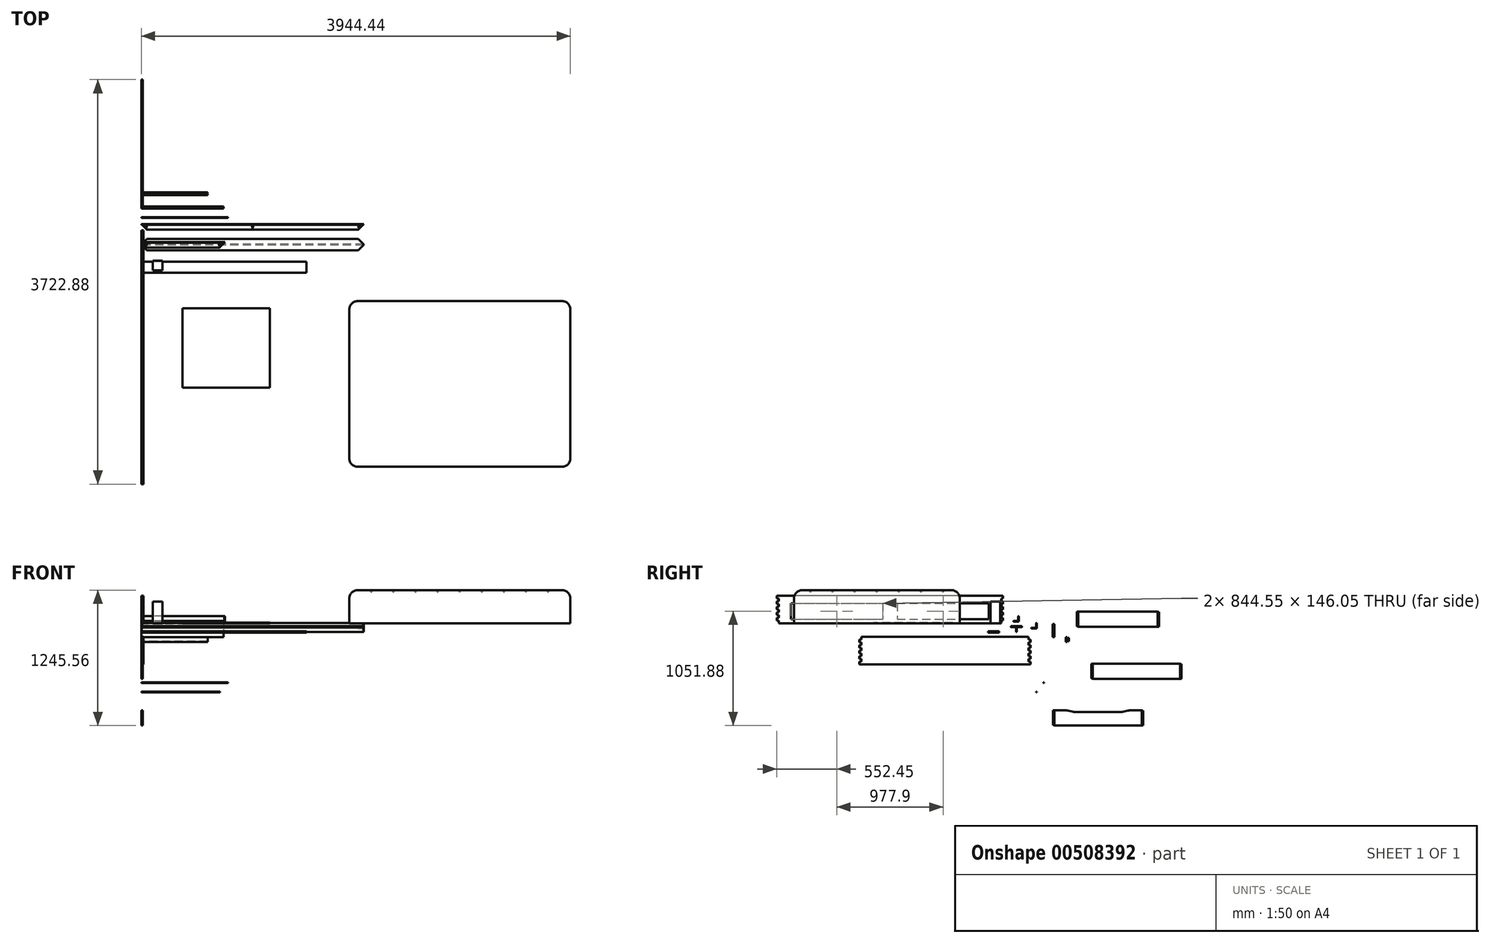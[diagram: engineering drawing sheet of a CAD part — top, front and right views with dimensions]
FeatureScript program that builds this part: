
annotation { "Feature Type Name" : "Feature", "Feature Type Description" : "" }
export const myFeature = defineFeature(function(context is Context, id is Id, definition is map)
    precondition{}
    {
        {
            var Q0;
            Q0=qCreatedBy(makeId("Right.planeOp"),FACE);
            var sketch = newSketch(context, id + "F0", { "sketchPlane" : qUnion([Q0])});
            skLineSegment(sketch, "E0.bottom", {"start": v(0, 0) * mm, "end": v(-2082.8, 0) * mm});
            skLineSegment(sketch, "E0.top", {"start": v(12.7, 254) * mm, "end": v(-2070.1, 254) * mm});
            skLineSegment(sketch, "E1", {"start": v(-2070.1, 254) * mm, "end": v(-2070.1, 228.6) * mm});
            skLineSegment(sketch, "E2", {"start": v(-2070.1, 228.6) * mm, "end": v(-2051.05, 228.6) * mm});
            skLineSegment(sketch, "E3", {"start": v(-2051.05, 228.6) * mm, "end": v(-2051.05, 203.2) * mm});
            skLineSegment(sketch, "E4", {"start": v(-2070.1, 254) * mm, "end": v(-2051.05, 254) * mm});
            skLineSegment(sketch, "E5.0.1.0", {"start": v(-2070.1, 203.2) * mm, "end": v(-2051.05, 203.2) * mm});
            skLineSegment(sketch, "E5.0.1.1", {"start": v(-2051.05, 177.8) * mm, "end": v(-2051.05, 152.4) * mm});
            skLineSegment(sketch, "E5.0.1.2", {"start": v(-2070.1, 177.8) * mm, "end": v(-2051.05, 177.8) * mm});
            skLineSegment(sketch, "E5.0.1.3", {"start": v(-2070.1, 203.2) * mm, "end": v(-2070.1, 177.8) * mm});
            skLineSegment(sketch, "E5.0.2.0", {"start": v(-2070.1, 152.4) * mm, "end": v(-2051.05, 152.4) * mm});
            skLineSegment(sketch, "E5.0.2.1", {"start": v(-2051.05, 127) * mm, "end": v(-2051.05, 101.6) * mm});
            skLineSegment(sketch, "E5.0.2.2", {"start": v(-2070.1, 127) * mm, "end": v(-2051.05, 127) * mm});
            skLineSegment(sketch, "E5.0.2.3", {"start": v(-2070.1, 152.4) * mm, "end": v(-2070.1, 127) * mm});
            skLineSegment(sketch, "E5.0.3.0", {"start": v(-2070.1, 101.6) * mm, "end": v(-2051.05, 101.6) * mm});
            skLineSegment(sketch, "E5.0.3.1", {"start": v(-2051.05, 76.2) * mm, "end": v(-2051.05, 50.8) * mm});
            skLineSegment(sketch, "E5.0.3.2", {"start": v(-2070.1, 76.2) * mm, "end": v(-2051.05, 76.2) * mm});
            skLineSegment(sketch, "E5.0.3.3", {"start": v(-2070.1, 101.6) * mm, "end": v(-2070.1, 76.2) * mm});
            skLineSegment(sketch, "E5.direction1", {"start": v(-2051.05, 203.2) * mm, "end": v(-1784.35, 203.2) * mm, "construction": true});
            skLineSegment(sketch, "E5.direction2", {"start": v(-2051.05, 203.2) * mm, "end": v(-2051.05, 152.4) * mm, "construction": true});
            skLineSegment(sketch, "E6.bottom", {"start": v(-1939.93, 184.15) * mm, "end": v(-1095.38, 184.15) * mm});
            skLineSegment(sketch, "E6.top", {"start": v(-1939.93, 38.1) * mm, "end": v(-1095.38, 38.1) * mm});
            skLineSegment(sketch, "E6.left", {"start": v(-1939.93, 184.15) * mm, "end": v(-1939.93, 38.1) * mm});
            skLineSegment(sketch, "E6.right", {"start": v(-1095.38, 184.15) * mm, "end": v(-1095.38, 38.1) * mm});
            skLineSegment(sketch, "E7.bottom", {"start": v(-962.02, 184.15) * mm, "end": v(-117.47, 184.15) * mm});
            skLineSegment(sketch, "E7.top", {"start": v(-962.02, 38.1) * mm, "end": v(-117.47, 38.1) * mm});
            skLineSegment(sketch, "E7.left", {"start": v(-962.02, 184.15) * mm, "end": v(-962.02, 38.1) * mm});
            skLineSegment(sketch, "E7.right", {"start": v(-117.47, 184.15) * mm, "end": v(-117.47, 38.1) * mm});
            skLineSegment(sketch, "E8.0.0.4", {"start": v(-2070.1, 50.8) * mm, "end": v(-2051.05, 50.8) * mm});
            skLineSegment(sketch, "E8.3.0.4", {"start": v(-2051.05, 25.4) * mm, "end": v(-2051.05, 0) * mm});
            skLineSegment(sketch, "E8.6.0.4", {"start": v(-2070.1, 25.4) * mm, "end": v(-2051.05, 25.4) * mm});
            skLineSegment(sketch, "E8.9.0.4", {"start": v(-2070.1, 50.8) * mm, "end": v(-2070.1, 25.4) * mm});
            skLineSegment(sketch, "E9", {"start": v(-6.35, 254) * mm, "end": v(12.7, 254) * mm});
            skLineSegment(sketch, "E10", {"start": v(12.7, 254) * mm, "end": v(12.7, 228.6) * mm});
            skLineSegment(sketch, "E11", {"start": v(12.7, 228.6) * mm, "end": v(-6.35, 228.6) * mm});
            skLineSegment(sketch, "E12", {"start": v(-6.35, 228.6) * mm, "end": v(-6.35, 203.2) * mm});
            skLineSegment(sketch, "E13.0.1.0", {"start": v(12.7, 177.8) * mm, "end": v(-6.35, 177.8) * mm});
            skLineSegment(sketch, "E13.0.1.1", {"start": v(-6.35, 177.8) * mm, "end": v(-6.35, 152.4) * mm});
            skLineSegment(sketch, "E13.0.1.2", {"start": v(12.7, 203.2) * mm, "end": v(12.7, 177.8) * mm});
            skLineSegment(sketch, "E13.0.1.3", {"start": v(-6.35, 203.2) * mm, "end": v(12.7, 203.2) * mm});
            skLineSegment(sketch, "E13.0.2.0", {"start": v(12.7, 127) * mm, "end": v(-6.35, 127) * mm});
            skLineSegment(sketch, "E13.0.2.1", {"start": v(-6.35, 127) * mm, "end": v(-6.35, 101.6) * mm});
            skLineSegment(sketch, "E13.0.2.2", {"start": v(12.7, 152.4) * mm, "end": v(12.7, 127) * mm});
            skLineSegment(sketch, "E13.0.2.3", {"start": v(-6.35, 152.4) * mm, "end": v(12.7, 152.4) * mm});
            skLineSegment(sketch, "E13.0.3.0", {"start": v(12.7, 76.2) * mm, "end": v(-6.35, 76.2) * mm});
            skLineSegment(sketch, "E13.0.3.1", {"start": v(-6.35, 76.2) * mm, "end": v(-6.35, 50.8) * mm});
            skLineSegment(sketch, "E13.0.3.2", {"start": v(12.7, 101.6) * mm, "end": v(12.7, 76.2) * mm});
            skLineSegment(sketch, "E13.0.3.3", {"start": v(-6.35, 101.6) * mm, "end": v(12.7, 101.6) * mm});
            skLineSegment(sketch, "E13.0.4.0", {"start": v(12.7, 25.4) * mm, "end": v(-6.35, 25.4) * mm});
            skLineSegment(sketch, "E13.0.4.1", {"start": v(-6.35, 25.4) * mm, "end": v(-6.35, 0) * mm});
            skLineSegment(sketch, "E13.0.4.2", {"start": v(12.7, 50.8) * mm, "end": v(12.7, 25.4) * mm});
            skLineSegment(sketch, "E13.0.4.3", {"start": v(-6.35, 50.8) * mm, "end": v(12.7, 50.8) * mm});
            skLineSegment(sketch, "E13.direction1", {"start": v(-6.35, 203.2) * mm, "end": v(6.35, 203.2) * mm, "construction": true});
            skLineSegment(sketch, "E13.direction2", {"start": v(-6.35, 203.2) * mm, "end": v(-6.35, 152.4) * mm, "construction": true});
            skSolve(sketch);
        }
        {
            var Q0;
            Q0 = qSketchRegion(id + "F0", true);
            extrude(context, id + "F1", {"entities" : qUnion([Q0]), "depth" : 19.05 * mm});
        }
        {
            var Q0;
            Q0=qCreatedBy(makeId("Right.planeOp"),FACE);
            var sketch = newSketch(context, id + "F2", { "sketchPlane" : qUnion([Q0])});
            skLineSegment(sketch, "E14.top", {"start": v(264.4, -378.2) * mm, "end": v(-1310.4, -378.2) * mm});
            skLineSegment(sketch, "E15", {"start": v(-1291.36, -378.2) * mm, "end": v(-1310.4, -378.2) * mm});
            skLineSegment(sketch, "E16", {"start": v(-1310.4, -352.8) * mm, "end": v(-1291.36, -352.8) * mm});
            skLineSegment(sketch, "E17", {"start": v(-1291.36, -352.8) * mm, "end": v(-1291.36, -327.4) * mm});
            skLineSegment(sketch, "E18", {"start": v(-1310.4, -378.2) * mm, "end": v(-1310.4, -352.8) * mm});
            skLineSegment(sketch, "E19.0.1.0", {"start": v(-1310.4, -302) * mm, "end": v(-1291.36, -302) * mm});
            skLineSegment(sketch, "E19.0.1.1", {"start": v(-1310.4, -327.4) * mm, "end": v(-1310.4, -302) * mm});
            skLineSegment(sketch, "E19.0.1.2", {"start": v(-1291.36, -327.4) * mm, "end": v(-1310.4, -327.4) * mm});
            skLineSegment(sketch, "E19.0.1.3", {"start": v(-1291.36, -302) * mm, "end": v(-1291.36, -276.6) * mm});
            skLineSegment(sketch, "E19.0.2.0", {"start": v(-1310.4, -251.2) * mm, "end": v(-1291.36, -251.2) * mm});
            skLineSegment(sketch, "E19.0.2.1", {"start": v(-1310.4, -276.6) * mm, "end": v(-1310.4, -251.2) * mm});
            skLineSegment(sketch, "E19.0.2.2", {"start": v(-1291.36, -276.6) * mm, "end": v(-1310.4, -276.6) * mm});
            skLineSegment(sketch, "E19.0.2.3", {"start": v(-1291.36, -251.2) * mm, "end": v(-1291.36, -225.8) * mm});
            skLineSegment(sketch, "E19.0.3.0", {"start": v(-1310.4, -200.4) * mm, "end": v(-1291.36, -200.4) * mm});
            skLineSegment(sketch, "E19.0.3.1", {"start": v(-1310.4, -225.8) * mm, "end": v(-1310.4, -200.4) * mm});
            skLineSegment(sketch, "E19.0.3.2", {"start": v(-1291.36, -225.8) * mm, "end": v(-1310.4, -225.8) * mm});
            skLineSegment(sketch, "E19.0.3.3", {"start": v(-1291.36, -200.4) * mm, "end": v(-1291.36, -175) * mm});
            skLineSegment(sketch, "E19.direction1", {"start": v(-1310.4, -378.2) * mm, "end": v(-1285, -378.2) * mm, "construction": true});
            skLineSegment(sketch, "E19.direction2", {"start": v(-1310.4, -378.2) * mm, "end": v(-1310.4, -327.4) * mm, "construction": true});
            skLineSegment(sketch, "E20", {"start": v(245.34, -378.2) * mm, "end": v(264.4, -378.2) * mm});
            skLineSegment(sketch, "E21", {"start": v(264.4, -352.8) * mm, "end": v(245.34, -352.8) * mm});
            skLineSegment(sketch, "E22", {"start": v(245.34, -352.8) * mm, "end": v(245.34, -327.4) * mm});
            skLineSegment(sketch, "E23", {"start": v(264.4, -352.8) * mm, "end": v(264.4, -378.2) * mm});
            skLineSegment(sketch, "E24.0.1.0", {"start": v(264.4, -302) * mm, "end": v(245.34, -302) * mm});
            skLineSegment(sketch, "E24.0.1.1", {"start": v(245.34, -302) * mm, "end": v(245.34, -276.6) * mm});
            skLineSegment(sketch, "E24.0.1.2", {"start": v(264.4, -302) * mm, "end": v(264.4, -327.4) * mm});
            skLineSegment(sketch, "E24.0.1.3", {"start": v(245.34, -327.4) * mm, "end": v(264.4, -327.4) * mm});
            skLineSegment(sketch, "E24.0.2.0", {"start": v(264.4, -251.2) * mm, "end": v(245.34, -251.2) * mm});
            skLineSegment(sketch, "E24.0.2.1", {"start": v(245.34, -251.2) * mm, "end": v(245.34, -225.8) * mm});
            skLineSegment(sketch, "E24.0.2.2", {"start": v(264.4, -251.2) * mm, "end": v(264.4, -276.6) * mm});
            skLineSegment(sketch, "E24.0.2.3", {"start": v(245.34, -276.6) * mm, "end": v(264.4, -276.6) * mm});
            skLineSegment(sketch, "E24.0.3.0", {"start": v(264.4, -200.4) * mm, "end": v(245.34, -200.4) * mm});
            skLineSegment(sketch, "E24.0.3.1", {"start": v(245.34, -200.4) * mm, "end": v(245.34, -175) * mm});
            skLineSegment(sketch, "E24.0.3.2", {"start": v(264.4, -200.4) * mm, "end": v(264.4, -225.8) * mm});
            skLineSegment(sketch, "E24.0.3.3", {"start": v(245.34, -225.8) * mm, "end": v(264.4, -225.8) * mm});
            skLineSegment(sketch, "E24.direction1", {"start": v(219.94, -378.2) * mm, "end": v(245.34, -378.2) * mm, "construction": true});
            skLineSegment(sketch, "E24.direction2", {"start": v(245.34, -378.2) * mm, "end": v(245.34, -327.4) * mm, "construction": true});
            skLineSegment(sketch, "E25.0.0.4", {"start": v(-1310.4, -149.6) * mm, "end": v(-1291.36, -149.6) * mm});
            skLineSegment(sketch, "E25.3.0.4", {"start": v(-1310.4, -175) * mm, "end": v(-1310.4, -149.6) * mm});
            skLineSegment(sketch, "E25.6.0.4", {"start": v(-1291.36, -175) * mm, "end": v(-1310.4, -175) * mm});
            skLineSegment(sketch, "E25.9.0.4", {"start": v(-1291.36, -149.6) * mm, "end": v(-1291.36, -124.2) * mm});
            skLineSegment(sketch, "E26.0.0.4", {"start": v(264.4, -149.6) * mm, "end": v(245.34, -149.6) * mm});
            skLineSegment(sketch, "E26.3.0.4", {"start": v(245.34, -149.6) * mm, "end": v(245.34, -124.2) * mm});
            skLineSegment(sketch, "E26.6.0.4", {"start": v(264.4, -149.6) * mm, "end": v(264.4, -175) * mm});
            skLineSegment(sketch, "E26.9.0.4", {"start": v(245.34, -175) * mm, "end": v(264.4, -175) * mm});
            skLineSegment(sketch, "E27", {"start": v(245.34, -124.2) * mm, "end": v(-1291.36, -124.2) * mm});
            skSolve(sketch);
        }
        {
            var Q0;
            Q0 = qSketchRegion(id + "F2", true);
            extrude(context, id + "F3", {"entities" : qUnion([Q0]), "depth" : 19.05 * mm});
        }
        {
            var Q0;
            Q0=qCreatedBy(makeId("Right.planeOp"),FACE);
            var sketch = newSketch(context, id + "F4", { "sketchPlane" : qUnion([Q0])});
            skLineSegment(sketch, "E28.bottom", {"start": v(702.37, 107.96) * mm, "end": v(1432.62, 107.96) * mm});
            skLineSegment(sketch, "E28.top", {"start": v(702.37, -31.74) * mm, "end": v(1445.32, -31.74) * mm});
            skLineSegment(sketch, "E29", {"start": v(1432.62, 104.78) * mm, "end": v(1445.32, 104.78) * mm});
            skLineSegment(sketch, "E30", {"start": v(1445.32, 101.6) * mm, "end": v(1432.62, 101.6) * mm});
            skLineSegment(sketch, "E31", {"start": v(1432.62, 101.6) * mm, "end": v(1432.62, 98.43) * mm});
            skLineSegment(sketch, "E32", {"start": v(1445.32, 104.78) * mm, "end": v(1445.32, 101.6) * mm});
            skLineSegment(sketch, "E33.0.1.0", {"start": v(1432.62, 98.43) * mm, "end": v(1445.32, 98.43) * mm});
            skLineSegment(sketch, "E33.0.1.1", {"start": v(1445.32, 95.26) * mm, "end": v(1432.62, 95.26) * mm});
            skLineSegment(sketch, "E33.0.1.2", {"start": v(1432.62, 95.26) * mm, "end": v(1432.62, 92.08) * mm});
            skLineSegment(sketch, "E33.0.1.3", {"start": v(1445.32, 98.43) * mm, "end": v(1445.32, 95.26) * mm});
            skLineSegment(sketch, "E33.0.2.0", {"start": v(1432.62, 92.08) * mm, "end": v(1445.32, 92.08) * mm});
            skLineSegment(sketch, "E33.0.2.1", {"start": v(1445.32, 88.9) * mm, "end": v(1432.62, 88.9) * mm});
            skLineSegment(sketch, "E33.0.2.2", {"start": v(1432.62, 88.9) * mm, "end": v(1432.62, 85.73) * mm});
            skLineSegment(sketch, "E33.0.2.3", {"start": v(1445.32, 92.08) * mm, "end": v(1445.32, 88.9) * mm});
            skLineSegment(sketch, "E33.0.3.0", {"start": v(1432.62, 85.73) * mm, "end": v(1445.32, 85.73) * mm});
            skLineSegment(sketch, "E33.0.3.1", {"start": v(1445.32, 82.56) * mm, "end": v(1432.62, 82.56) * mm});
            skLineSegment(sketch, "E33.0.3.2", {"start": v(1432.62, 82.56) * mm, "end": v(1432.62, 79.38) * mm});
            skLineSegment(sketch, "E33.0.3.3", {"start": v(1445.32, 85.73) * mm, "end": v(1445.32, 82.56) * mm});
            skLineSegment(sketch, "E33.0.4.0", {"start": v(1432.62, 79.38) * mm, "end": v(1445.32, 79.38) * mm});
            skLineSegment(sketch, "E33.0.4.1", {"start": v(1445.32, 76.2) * mm, "end": v(1432.62, 76.2) * mm});
            skLineSegment(sketch, "E33.0.4.2", {"start": v(1432.62, 76.2) * mm, "end": v(1432.62, 73.03) * mm});
            skLineSegment(sketch, "E33.0.4.3", {"start": v(1445.32, 79.38) * mm, "end": v(1445.32, 76.2) * mm});
            skLineSegment(sketch, "E33.0.5.0", {"start": v(1432.62, 73.03) * mm, "end": v(1445.32, 73.03) * mm});
            skLineSegment(sketch, "E33.0.5.1", {"start": v(1445.32, 69.86) * mm, "end": v(1432.62, 69.86) * mm});
            skLineSegment(sketch, "E33.0.5.2", {"start": v(1432.62, 69.86) * mm, "end": v(1432.62, 66.68) * mm});
            skLineSegment(sketch, "E33.0.5.3", {"start": v(1445.32, 73.03) * mm, "end": v(1445.32, 69.86) * mm});
            skLineSegment(sketch, "E33.0.6.0", {"start": v(1432.62, 66.68) * mm, "end": v(1445.32, 66.68) * mm});
            skLineSegment(sketch, "E33.0.6.1", {"start": v(1445.32, 63.5) * mm, "end": v(1432.62, 63.5) * mm});
            skLineSegment(sketch, "E33.0.6.2", {"start": v(1432.62, 63.5) * mm, "end": v(1432.62, 60.33) * mm});
            skLineSegment(sketch, "E33.0.6.3", {"start": v(1445.32, 66.68) * mm, "end": v(1445.32, 63.5) * mm});
            skLineSegment(sketch, "E33.0.7.0", {"start": v(1432.62, 60.33) * mm, "end": v(1445.32, 60.33) * mm});
            skLineSegment(sketch, "E33.0.7.1", {"start": v(1445.32, 57.16) * mm, "end": v(1432.62, 57.16) * mm});
            skLineSegment(sketch, "E33.0.7.2", {"start": v(1432.62, 57.16) * mm, "end": v(1432.62, 53.98) * mm});
            skLineSegment(sketch, "E33.0.7.3", {"start": v(1445.32, 60.33) * mm, "end": v(1445.32, 57.16) * mm});
            skLineSegment(sketch, "E33.0.8.0", {"start": v(1432.62, 53.98) * mm, "end": v(1445.32, 53.98) * mm});
            skLineSegment(sketch, "E33.0.8.1", {"start": v(1445.32, 50.8) * mm, "end": v(1432.62, 50.8) * mm});
            skLineSegment(sketch, "E33.0.8.2", {"start": v(1432.62, 50.8) * mm, "end": v(1432.62, 47.63) * mm});
            skLineSegment(sketch, "E33.0.8.3", {"start": v(1445.32, 53.98) * mm, "end": v(1445.32, 50.8) * mm});
            skLineSegment(sketch, "E33.0.9.0", {"start": v(1432.62, 47.63) * mm, "end": v(1445.32, 47.63) * mm});
            skLineSegment(sketch, "E33.0.9.1", {"start": v(1445.32, 44.46) * mm, "end": v(1432.62, 44.46) * mm});
            skLineSegment(sketch, "E33.0.9.2", {"start": v(1432.62, 44.46) * mm, "end": v(1432.62, 41.28) * mm});
            skLineSegment(sketch, "E33.0.9.3", {"start": v(1445.32, 47.63) * mm, "end": v(1445.32, 44.46) * mm});
            skLineSegment(sketch, "E33.0.10.0", {"start": v(1432.62, 41.28) * mm, "end": v(1445.32, 41.28) * mm});
            skLineSegment(sketch, "E33.0.10.1", {"start": v(1445.32, 38.1) * mm, "end": v(1432.62, 38.1) * mm});
            skLineSegment(sketch, "E33.0.10.2", {"start": v(1432.62, 38.1) * mm, "end": v(1432.62, 34.93) * mm});
            skLineSegment(sketch, "E33.0.10.3", {"start": v(1445.32, 41.28) * mm, "end": v(1445.32, 38.1) * mm});
            skLineSegment(sketch, "E33.0.11.0", {"start": v(1432.62, 34.93) * mm, "end": v(1445.32, 34.93) * mm});
            skLineSegment(sketch, "E33.0.11.1", {"start": v(1445.32, 31.76) * mm, "end": v(1432.62, 31.76) * mm});
            skLineSegment(sketch, "E33.0.11.2", {"start": v(1432.62, 31.76) * mm, "end": v(1432.62, 28.58) * mm});
            skLineSegment(sketch, "E33.0.11.3", {"start": v(1445.32, 34.93) * mm, "end": v(1445.32, 31.76) * mm});
            skLineSegment(sketch, "E33.0.12.0", {"start": v(1432.62, 28.58) * mm, "end": v(1445.32, 28.58) * mm});
            skLineSegment(sketch, "E33.0.12.1", {"start": v(1445.32, 25.4) * mm, "end": v(1432.62, 25.4) * mm});
            skLineSegment(sketch, "E33.0.12.2", {"start": v(1432.62, 25.4) * mm, "end": v(1432.62, 22.23) * mm});
            skLineSegment(sketch, "E33.0.12.3", {"start": v(1445.32, 28.58) * mm, "end": v(1445.32, 25.4) * mm});
            skLineSegment(sketch, "E33.0.13.0", {"start": v(1432.62, 22.23) * mm, "end": v(1445.32, 22.23) * mm});
            skLineSegment(sketch, "E33.0.13.1", {"start": v(1445.32, 19.06) * mm, "end": v(1432.62, 19.06) * mm});
            skLineSegment(sketch, "E33.0.13.2", {"start": v(1432.62, 19.06) * mm, "end": v(1432.62, 15.88) * mm});
            skLineSegment(sketch, "E33.0.13.3", {"start": v(1445.32, 22.23) * mm, "end": v(1445.32, 19.06) * mm});
            skLineSegment(sketch, "E33.0.14.0", {"start": v(1432.62, 15.88) * mm, "end": v(1445.32, 15.88) * mm});
            skLineSegment(sketch, "E33.0.14.1", {"start": v(1445.32, 12.7) * mm, "end": v(1432.62, 12.7) * mm});
            skLineSegment(sketch, "E33.0.14.2", {"start": v(1432.62, 12.7) * mm, "end": v(1432.62, 9.53) * mm});
            skLineSegment(sketch, "E33.0.14.3", {"start": v(1445.32, 15.88) * mm, "end": v(1445.32, 12.7) * mm});
            skLineSegment(sketch, "E33.0.15.0", {"start": v(1432.62, 9.53) * mm, "end": v(1445.32, 9.53) * mm});
            skLineSegment(sketch, "E33.0.15.1", {"start": v(1445.32, 6.36) * mm, "end": v(1432.62, 6.36) * mm});
            skLineSegment(sketch, "E33.0.15.2", {"start": v(1432.62, 6.36) * mm, "end": v(1432.62, 3.18) * mm});
            skLineSegment(sketch, "E33.0.15.3", {"start": v(1445.32, 9.53) * mm, "end": v(1445.32, 6.36) * mm});
            skLineSegment(sketch, "E33.0.16.0", {"start": v(1432.62, 3.18) * mm, "end": v(1445.32, 3.18) * mm});
            skLineSegment(sketch, "E33.0.16.1", {"start": v(1445.32, 0) * mm, "end": v(1432.62, 0) * mm});
            skLineSegment(sketch, "E33.0.16.2", {"start": v(1432.62, 0) * mm, "end": v(1432.62, -3.17) * mm});
            skLineSegment(sketch, "E33.0.16.3", {"start": v(1445.32, 3.18) * mm, "end": v(1445.32, 0) * mm});
            skLineSegment(sketch, "E33.0.17.0", {"start": v(1432.62, -3.17) * mm, "end": v(1445.32, -3.17) * mm});
            skLineSegment(sketch, "E33.0.17.1", {"start": v(1445.32, -6.34) * mm, "end": v(1432.62, -6.34) * mm});
            skLineSegment(sketch, "E33.0.17.2", {"start": v(1432.62, -6.34) * mm, "end": v(1432.62, -9.52) * mm});
            skLineSegment(sketch, "E33.0.17.3", {"start": v(1445.32, -3.17) * mm, "end": v(1445.32, -6.34) * mm});
            skLineSegment(sketch, "E33.0.18.0", {"start": v(1432.62, -9.52) * mm, "end": v(1445.32, -9.52) * mm});
            skLineSegment(sketch, "E33.0.18.1", {"start": v(1445.32, -12.7) * mm, "end": v(1432.62, -12.7) * mm});
            skLineSegment(sketch, "E33.0.18.2", {"start": v(1432.62, -12.7) * mm, "end": v(1432.62, -15.87) * mm});
            skLineSegment(sketch, "E33.0.18.3", {"start": v(1445.32, -9.52) * mm, "end": v(1445.32, -12.7) * mm});
            skLineSegment(sketch, "E33.0.19.0", {"start": v(1432.62, -15.87) * mm, "end": v(1445.32, -15.87) * mm});
            skLineSegment(sketch, "E33.0.19.1", {"start": v(1445.32, -19.04) * mm, "end": v(1432.62, -19.04) * mm});
            skLineSegment(sketch, "E33.0.19.2", {"start": v(1432.62, -19.04) * mm, "end": v(1432.62, -22.22) * mm});
            skLineSegment(sketch, "E33.0.19.3", {"start": v(1445.32, -15.87) * mm, "end": v(1445.32, -19.04) * mm});
            skLineSegment(sketch, "E33.0.20.0", {"start": v(1432.62, -22.22) * mm, "end": v(1445.32, -22.22) * mm});
            skLineSegment(sketch, "E33.0.20.1", {"start": v(1445.32, -25.4) * mm, "end": v(1432.62, -25.4) * mm});
            skLineSegment(sketch, "E33.0.20.2", {"start": v(1432.62, -25.4) * mm, "end": v(1432.62, -28.57) * mm});
            skLineSegment(sketch, "E33.0.20.3", {"start": v(1445.32, -22.22) * mm, "end": v(1445.32, -25.4) * mm});
            skLineSegment(sketch, "E33.0.21.0", {"start": v(1432.62, -28.57) * mm, "end": v(1445.32, -28.57) * mm});
            skLineSegment(sketch, "E33.0.21.1", {"start": v(1445.32, -31.74) * mm, "end": v(1432.62, -31.74) * mm});
            skLineSegment(sketch, "E33.0.21.3", {"start": v(1445.32, -28.57) * mm, "end": v(1445.32, -31.74) * mm});
            skLineSegment(sketch, "E33.direction1", {"start": v(1432.62, 98.43) * mm, "end": v(1458.02, 98.43) * mm, "construction": true});
            skLineSegment(sketch, "E33.direction2", {"start": v(1432.62, 98.43) * mm, "end": v(1432.62, 92.08) * mm, "construction": true});
            skLineSegment(sketch, "E34", {"start": v(1432.62, 104.78) * mm, "end": v(1432.62, 107.96) * mm});
            skLineSegment(sketch, "E35", {"start": v(702.37, -31.74) * mm, "end": v(702.37, -28.57) * mm});
            skLineSegment(sketch, "E36", {"start": v(702.37, -28.57) * mm, "end": v(689.67, -28.57) * mm});
            skLineSegment(sketch, "E37", {"start": v(689.67, -28.57) * mm, "end": v(689.67, -25.4) * mm});
            skLineSegment(sketch, "E38", {"start": v(689.67, -25.4) * mm, "end": v(702.37, -25.4) * mm});
            skLineSegment(sketch, "E39.0.1.0", {"start": v(702.37, -22.22) * mm, "end": v(689.67, -22.22) * mm});
            skLineSegment(sketch, "E39.0.1.1", {"start": v(689.67, -19.04) * mm, "end": v(702.37, -19.04) * mm});
            skLineSegment(sketch, "E39.0.1.2", {"start": v(702.37, -25.4) * mm, "end": v(702.37, -22.22) * mm});
            skLineSegment(sketch, "E39.0.1.3", {"start": v(689.67, -22.22) * mm, "end": v(689.67, -19.04) * mm});
            skLineSegment(sketch, "E39.0.2.0", {"start": v(702.37, -15.87) * mm, "end": v(689.67, -15.87) * mm});
            skLineSegment(sketch, "E39.0.2.1", {"start": v(689.67, -12.7) * mm, "end": v(702.37, -12.7) * mm});
            skLineSegment(sketch, "E39.0.2.2", {"start": v(702.37, -19.04) * mm, "end": v(702.37, -15.87) * mm});
            skLineSegment(sketch, "E39.0.2.3", {"start": v(689.67, -15.87) * mm, "end": v(689.67, -12.7) * mm});
            skLineSegment(sketch, "E39.0.3.0", {"start": v(702.37, -9.52) * mm, "end": v(689.67, -9.52) * mm});
            skLineSegment(sketch, "E39.0.3.1", {"start": v(689.67, -6.34) * mm, "end": v(702.37, -6.34) * mm});
            skLineSegment(sketch, "E39.0.3.2", {"start": v(702.37, -12.7) * mm, "end": v(702.37, -9.52) * mm});
            skLineSegment(sketch, "E39.0.3.3", {"start": v(689.67, -9.52) * mm, "end": v(689.67, -6.34) * mm});
            skLineSegment(sketch, "E39.0.4.0", {"start": v(702.37, -3.17) * mm, "end": v(689.67, -3.17) * mm});
            skLineSegment(sketch, "E39.0.4.1", {"start": v(689.67, 0) * mm, "end": v(702.37, 0) * mm});
            skLineSegment(sketch, "E39.0.4.2", {"start": v(702.37, -6.34) * mm, "end": v(702.37, -3.17) * mm});
            skLineSegment(sketch, "E39.0.4.3", {"start": v(689.67, -3.17) * mm, "end": v(689.67, 0) * mm});
            skLineSegment(sketch, "E39.0.5.0", {"start": v(702.37, 3.18) * mm, "end": v(689.67, 3.18) * mm});
            skLineSegment(sketch, "E39.0.5.1", {"start": v(689.67, 6.36) * mm, "end": v(702.37, 6.36) * mm});
            skLineSegment(sketch, "E39.0.5.2", {"start": v(702.37, 0) * mm, "end": v(702.37, 3.18) * mm});
            skLineSegment(sketch, "E39.0.5.3", {"start": v(689.67, 3.18) * mm, "end": v(689.67, 6.36) * mm});
            skLineSegment(sketch, "E39.0.6.0", {"start": v(702.37, 9.53) * mm, "end": v(689.67, 9.53) * mm});
            skLineSegment(sketch, "E39.0.6.1", {"start": v(689.67, 12.7) * mm, "end": v(702.37, 12.7) * mm});
            skLineSegment(sketch, "E39.0.6.2", {"start": v(702.37, 6.36) * mm, "end": v(702.37, 9.53) * mm});
            skLineSegment(sketch, "E39.0.6.3", {"start": v(689.67, 9.53) * mm, "end": v(689.67, 12.7) * mm});
            skLineSegment(sketch, "E39.0.7.0", {"start": v(702.37, 15.88) * mm, "end": v(689.67, 15.88) * mm});
            skLineSegment(sketch, "E39.0.7.1", {"start": v(689.67, 19.06) * mm, "end": v(702.37, 19.06) * mm});
            skLineSegment(sketch, "E39.0.7.2", {"start": v(702.37, 12.7) * mm, "end": v(702.37, 15.88) * mm});
            skLineSegment(sketch, "E39.0.7.3", {"start": v(689.67, 15.88) * mm, "end": v(689.67, 19.06) * mm});
            skLineSegment(sketch, "E39.0.8.0", {"start": v(702.37, 22.23) * mm, "end": v(689.67, 22.23) * mm});
            skLineSegment(sketch, "E39.0.8.1", {"start": v(689.67, 25.4) * mm, "end": v(702.37, 25.4) * mm});
            skLineSegment(sketch, "E39.0.8.2", {"start": v(702.37, 19.06) * mm, "end": v(702.37, 22.23) * mm});
            skLineSegment(sketch, "E39.0.8.3", {"start": v(689.67, 22.23) * mm, "end": v(689.67, 25.4) * mm});
            skLineSegment(sketch, "E39.0.9.0", {"start": v(702.37, 28.58) * mm, "end": v(689.67, 28.58) * mm});
            skLineSegment(sketch, "E39.0.9.1", {"start": v(689.67, 31.76) * mm, "end": v(702.37, 31.76) * mm});
            skLineSegment(sketch, "E39.0.9.2", {"start": v(702.37, 25.4) * mm, "end": v(702.37, 28.58) * mm});
            skLineSegment(sketch, "E39.0.9.3", {"start": v(689.67, 28.58) * mm, "end": v(689.67, 31.76) * mm});
            skLineSegment(sketch, "E39.0.10.0", {"start": v(702.37, 34.93) * mm, "end": v(689.67, 34.93) * mm});
            skLineSegment(sketch, "E39.0.10.1", {"start": v(689.67, 38.1) * mm, "end": v(702.37, 38.1) * mm});
            skLineSegment(sketch, "E39.0.10.2", {"start": v(702.37, 31.76) * mm, "end": v(702.37, 34.93) * mm});
            skLineSegment(sketch, "E39.0.10.3", {"start": v(689.67, 34.93) * mm, "end": v(689.67, 38.1) * mm});
            skLineSegment(sketch, "E39.0.11.0", {"start": v(702.37, 41.28) * mm, "end": v(689.67, 41.28) * mm});
            skLineSegment(sketch, "E39.0.11.1", {"start": v(689.67, 44.46) * mm, "end": v(702.37, 44.46) * mm});
            skLineSegment(sketch, "E39.0.11.2", {"start": v(702.37, 38.1) * mm, "end": v(702.37, 41.28) * mm});
            skLineSegment(sketch, "E39.0.11.3", {"start": v(689.67, 41.28) * mm, "end": v(689.67, 44.46) * mm});
            skLineSegment(sketch, "E39.0.12.0", {"start": v(702.37, 47.63) * mm, "end": v(689.67, 47.63) * mm});
            skLineSegment(sketch, "E39.0.12.1", {"start": v(689.67, 50.8) * mm, "end": v(702.37, 50.8) * mm});
            skLineSegment(sketch, "E39.0.12.2", {"start": v(702.37, 44.46) * mm, "end": v(702.37, 47.63) * mm});
            skLineSegment(sketch, "E39.0.12.3", {"start": v(689.67, 47.63) * mm, "end": v(689.67, 50.8) * mm});
            skLineSegment(sketch, "E39.0.13.0", {"start": v(702.37, 53.98) * mm, "end": v(689.67, 53.98) * mm});
            skLineSegment(sketch, "E39.0.13.1", {"start": v(689.67, 57.16) * mm, "end": v(702.37, 57.16) * mm});
            skLineSegment(sketch, "E39.0.13.2", {"start": v(702.37, 50.8) * mm, "end": v(702.37, 53.98) * mm});
            skLineSegment(sketch, "E39.0.13.3", {"start": v(689.67, 53.98) * mm, "end": v(689.67, 57.16) * mm});
            skLineSegment(sketch, "E39.0.14.0", {"start": v(702.37, 60.33) * mm, "end": v(689.67, 60.33) * mm});
            skLineSegment(sketch, "E39.0.14.1", {"start": v(689.67, 63.5) * mm, "end": v(702.37, 63.5) * mm});
            skLineSegment(sketch, "E39.0.14.2", {"start": v(702.37, 57.16) * mm, "end": v(702.37, 60.33) * mm});
            skLineSegment(sketch, "E39.0.14.3", {"start": v(689.67, 60.33) * mm, "end": v(689.67, 63.5) * mm});
            skLineSegment(sketch, "E39.0.15.0", {"start": v(702.37, 66.68) * mm, "end": v(689.67, 66.68) * mm});
            skLineSegment(sketch, "E39.0.15.1", {"start": v(689.67, 69.86) * mm, "end": v(702.37, 69.86) * mm});
            skLineSegment(sketch, "E39.0.15.2", {"start": v(702.37, 63.5) * mm, "end": v(702.37, 66.68) * mm});
            skLineSegment(sketch, "E39.0.15.3", {"start": v(689.67, 66.68) * mm, "end": v(689.67, 69.86) * mm});
            skLineSegment(sketch, "E39.0.16.0", {"start": v(702.37, 73.03) * mm, "end": v(689.67, 73.03) * mm});
            skLineSegment(sketch, "E39.0.16.1", {"start": v(689.67, 76.2) * mm, "end": v(702.37, 76.2) * mm});
            skLineSegment(sketch, "E39.0.16.2", {"start": v(702.37, 69.86) * mm, "end": v(702.37, 73.03) * mm});
            skLineSegment(sketch, "E39.0.16.3", {"start": v(689.67, 73.03) * mm, "end": v(689.67, 76.2) * mm});
            skLineSegment(sketch, "E39.0.17.0", {"start": v(702.37, 79.38) * mm, "end": v(689.67, 79.38) * mm});
            skLineSegment(sketch, "E39.0.17.1", {"start": v(689.67, 82.56) * mm, "end": v(702.37, 82.56) * mm});
            skLineSegment(sketch, "E39.0.17.2", {"start": v(702.37, 76.2) * mm, "end": v(702.37, 79.38) * mm});
            skLineSegment(sketch, "E39.0.17.3", {"start": v(689.67, 79.38) * mm, "end": v(689.67, 82.56) * mm});
            skLineSegment(sketch, "E39.0.18.0", {"start": v(702.37, 85.73) * mm, "end": v(689.67, 85.73) * mm});
            skLineSegment(sketch, "E39.0.18.1", {"start": v(689.67, 88.9) * mm, "end": v(702.37, 88.9) * mm});
            skLineSegment(sketch, "E39.0.18.2", {"start": v(702.37, 82.56) * mm, "end": v(702.37, 85.73) * mm});
            skLineSegment(sketch, "E39.0.18.3", {"start": v(689.67, 85.73) * mm, "end": v(689.67, 88.9) * mm});
            skLineSegment(sketch, "E39.0.19.0", {"start": v(702.37, 92.08) * mm, "end": v(689.67, 92.08) * mm});
            skLineSegment(sketch, "E39.0.19.1", {"start": v(689.67, 95.26) * mm, "end": v(702.37, 95.26) * mm});
            skLineSegment(sketch, "E39.0.19.2", {"start": v(702.37, 88.9) * mm, "end": v(702.37, 92.08) * mm});
            skLineSegment(sketch, "E39.0.19.3", {"start": v(689.67, 92.08) * mm, "end": v(689.67, 95.26) * mm});
            skLineSegment(sketch, "E39.0.20.0", {"start": v(702.37, 98.43) * mm, "end": v(689.67, 98.43) * mm});
            skLineSegment(sketch, "E39.0.20.1", {"start": v(689.67, 101.6) * mm, "end": v(702.37, 101.6) * mm});
            skLineSegment(sketch, "E39.0.20.2", {"start": v(702.37, 95.26) * mm, "end": v(702.37, 98.43) * mm});
            skLineSegment(sketch, "E39.0.20.3", {"start": v(689.67, 98.43) * mm, "end": v(689.67, 101.6) * mm});
            skLineSegment(sketch, "E39.0.21.0", {"start": v(702.37, 104.78) * mm, "end": v(689.67, 104.78) * mm});
            skLineSegment(sketch, "E39.0.21.1", {"start": v(689.67, 107.96) * mm, "end": v(702.37, 107.96) * mm});
            skLineSegment(sketch, "E39.0.21.2", {"start": v(702.37, 101.6) * mm, "end": v(702.37, 104.78) * mm});
            skLineSegment(sketch, "E39.0.21.3", {"start": v(689.67, 104.78) * mm, "end": v(689.67, 107.96) * mm});
            skLineSegment(sketch, "E39.direction1", {"start": v(689.67, -28.57) * mm, "end": v(715.07, -28.57) * mm, "construction": true});
            skLineSegment(sketch, "E39.direction2", {"start": v(689.67, -28.57) * mm, "end": v(689.67, -22.22) * mm, "construction": true});
            skSolve(sketch);
        }
        {
            var Q0;
            Q0=makeQuery(id+"F4.imprint","IMPRINT",FACE,{"disambiguationData":[TD([[makeQuery(id+"F4.imprint","IMPRINT",EDGE,{"derivedFrom":sQuery(id+"F4.wireOp",EDGE,"E28.bottom")}),-1.0]])]});
            extrude(context, id + "F5", {"entities" : qUnion([Q0]), "depth" : 12.7 * mm});
        }
        {
            var Q0;
            Q0=qCreatedBy(makeId("Right.planeOp"),FACE);
            var sketch = newSketch(context, id + "F6", { "sketchPlane" : qUnion([Q0])});
            skLineSegment(sketch, "E40.bottom", {"start": v(836.8, -371.44) * mm, "end": v(1640.08, -371.44) * mm});
            skLineSegment(sketch, "E40.top", {"start": v(836.8, -511.14) * mm, "end": v(1640.08, -511.14) * mm});
            skLineSegment(sketch, "E40.left", {"start": v(836.8, -371.44) * mm, "end": v(836.8, -511.14) * mm});
            skLineSegment(sketch, "E40.right", {"start": v(1640.08, -371.44) * mm, "end": v(1640.08, -511.14) * mm});
            skLineSegment(sketch, "E41", {"start": v(836.8, -371.44) * mm, "end": v(824.1, -371.44) * mm});
            skLineSegment(sketch, "E42", {"start": v(824.1, -371.44) * mm, "end": v(824.1, -374.62) * mm});
            skLineSegment(sketch, "E43", {"start": v(824.1, -374.62) * mm, "end": v(836.8, -374.62) * mm});
            skLineSegment(sketch, "E44", {"start": v(836.8, -374.62) * mm, "end": v(836.8, -377.8) * mm});
            skLineSegment(sketch, "E45", {"start": v(1640.08, -511.14) * mm, "end": v(1652.78, -511.14) * mm});
            skLineSegment(sketch, "E46", {"start": v(1652.78, -511.14) * mm, "end": v(1652.78, -507.97) * mm});
            skLineSegment(sketch, "E47", {"start": v(1652.78, -507.97) * mm, "end": v(1640.08, -507.97) * mm});
            skLineSegment(sketch, "E48", {"start": v(1640.08, -507.97) * mm, "end": v(1640.08, -504.8) * mm});
            skLineSegment(sketch, "E49.0.1.0", {"start": v(1652.78, -501.62) * mm, "end": v(1640.08, -501.62) * mm});
            skLineSegment(sketch, "E49.0.1.1", {"start": v(1640.08, -504.8) * mm, "end": v(1652.78, -504.8) * mm});
            skLineSegment(sketch, "E49.0.1.2", {"start": v(1652.78, -504.8) * mm, "end": v(1652.78, -501.62) * mm});
            skLineSegment(sketch, "E49.0.1.3", {"start": v(1640.08, -501.62) * mm, "end": v(1640.08, -498.44) * mm});
            skLineSegment(sketch, "E49.0.2.0", {"start": v(1652.78, -495.27) * mm, "end": v(1640.08, -495.27) * mm});
            skLineSegment(sketch, "E49.0.2.1", {"start": v(1640.08, -498.44) * mm, "end": v(1652.78, -498.44) * mm});
            skLineSegment(sketch, "E49.0.2.2", {"start": v(1652.78, -498.44) * mm, "end": v(1652.78, -495.27) * mm});
            skLineSegment(sketch, "E49.0.2.3", {"start": v(1640.08, -495.27) * mm, "end": v(1640.08, -492.1) * mm});
            skLineSegment(sketch, "E49.0.3.0", {"start": v(1652.78, -488.92) * mm, "end": v(1640.08, -488.92) * mm});
            skLineSegment(sketch, "E49.0.3.1", {"start": v(1640.08, -492.1) * mm, "end": v(1652.78, -492.1) * mm});
            skLineSegment(sketch, "E49.0.3.2", {"start": v(1652.78, -492.1) * mm, "end": v(1652.78, -488.92) * mm});
            skLineSegment(sketch, "E49.0.3.3", {"start": v(1640.08, -488.92) * mm, "end": v(1640.08, -485.74) * mm});
            skLineSegment(sketch, "E49.0.4.0", {"start": v(1652.78, -482.57) * mm, "end": v(1640.08, -482.57) * mm});
            skLineSegment(sketch, "E49.0.4.1", {"start": v(1640.08, -485.74) * mm, "end": v(1652.78, -485.74) * mm});
            skLineSegment(sketch, "E49.0.4.2", {"start": v(1652.78, -485.74) * mm, "end": v(1652.78, -482.57) * mm});
            skLineSegment(sketch, "E49.0.4.3", {"start": v(1640.08, -482.57) * mm, "end": v(1640.08, -479.4) * mm});
            skLineSegment(sketch, "E49.0.5.0", {"start": v(1652.78, -476.22) * mm, "end": v(1640.08, -476.22) * mm});
            skLineSegment(sketch, "E49.0.5.1", {"start": v(1640.08, -479.4) * mm, "end": v(1652.78, -479.4) * mm});
            skLineSegment(sketch, "E49.0.5.2", {"start": v(1652.78, -479.4) * mm, "end": v(1652.78, -476.22) * mm});
            skLineSegment(sketch, "E49.0.5.3", {"start": v(1640.08, -476.22) * mm, "end": v(1640.08, -473.04) * mm});
            skLineSegment(sketch, "E49.0.6.0", {"start": v(1652.78, -469.87) * mm, "end": v(1640.08, -469.87) * mm});
            skLineSegment(sketch, "E49.0.6.1", {"start": v(1640.08, -473.04) * mm, "end": v(1652.78, -473.04) * mm});
            skLineSegment(sketch, "E49.0.6.2", {"start": v(1652.78, -473.04) * mm, "end": v(1652.78, -469.87) * mm});
            skLineSegment(sketch, "E49.0.6.3", {"start": v(1640.08, -469.87) * mm, "end": v(1640.08, -466.7) * mm});
            skLineSegment(sketch, "E49.0.7.0", {"start": v(1652.78, -463.52) * mm, "end": v(1640.08, -463.52) * mm});
            skLineSegment(sketch, "E49.0.7.1", {"start": v(1640.08, -466.7) * mm, "end": v(1652.78, -466.7) * mm});
            skLineSegment(sketch, "E49.0.7.2", {"start": v(1652.78, -466.7) * mm, "end": v(1652.78, -463.52) * mm});
            skLineSegment(sketch, "E49.0.7.3", {"start": v(1640.08, -463.52) * mm, "end": v(1640.08, -460.34) * mm});
            skLineSegment(sketch, "E49.0.8.0", {"start": v(1652.78, -457.17) * mm, "end": v(1640.08, -457.17) * mm});
            skLineSegment(sketch, "E49.0.8.1", {"start": v(1640.08, -460.34) * mm, "end": v(1652.78, -460.34) * mm});
            skLineSegment(sketch, "E49.0.8.2", {"start": v(1652.78, -460.34) * mm, "end": v(1652.78, -457.17) * mm});
            skLineSegment(sketch, "E49.0.8.3", {"start": v(1640.08, -457.17) * mm, "end": v(1640.08, -454) * mm});
            skLineSegment(sketch, "E49.0.9.0", {"start": v(1652.78, -450.82) * mm, "end": v(1640.08, -450.82) * mm});
            skLineSegment(sketch, "E49.0.9.1", {"start": v(1640.08, -454) * mm, "end": v(1652.78, -454) * mm});
            skLineSegment(sketch, "E49.0.9.2", {"start": v(1652.78, -454) * mm, "end": v(1652.78, -450.82) * mm});
            skLineSegment(sketch, "E49.0.9.3", {"start": v(1640.08, -450.82) * mm, "end": v(1640.08, -447.64) * mm});
            skLineSegment(sketch, "E49.0.10.0", {"start": v(1652.78, -444.47) * mm, "end": v(1640.08, -444.47) * mm});
            skLineSegment(sketch, "E49.0.10.1", {"start": v(1640.08, -447.64) * mm, "end": v(1652.78, -447.64) * mm});
            skLineSegment(sketch, "E49.0.10.2", {"start": v(1652.78, -447.64) * mm, "end": v(1652.78, -444.47) * mm});
            skLineSegment(sketch, "E49.0.10.3", {"start": v(1640.08, -444.47) * mm, "end": v(1640.08, -441.3) * mm});
            skLineSegment(sketch, "E49.0.11.0", {"start": v(1652.78, -438.12) * mm, "end": v(1640.08, -438.12) * mm});
            skLineSegment(sketch, "E49.0.11.1", {"start": v(1640.08, -441.3) * mm, "end": v(1652.78, -441.3) * mm});
            skLineSegment(sketch, "E49.0.11.2", {"start": v(1652.78, -441.3) * mm, "end": v(1652.78, -438.12) * mm});
            skLineSegment(sketch, "E49.0.11.3", {"start": v(1640.08, -438.12) * mm, "end": v(1640.08, -434.94) * mm});
            skLineSegment(sketch, "E49.0.12.0", {"start": v(1652.78, -431.77) * mm, "end": v(1640.08, -431.77) * mm});
            skLineSegment(sketch, "E49.0.12.1", {"start": v(1640.08, -434.94) * mm, "end": v(1652.78, -434.94) * mm});
            skLineSegment(sketch, "E49.0.12.2", {"start": v(1652.78, -434.94) * mm, "end": v(1652.78, -431.77) * mm});
            skLineSegment(sketch, "E49.0.12.3", {"start": v(1640.08, -431.77) * mm, "end": v(1640.08, -428.6) * mm});
            skLineSegment(sketch, "E49.0.13.0", {"start": v(1652.78, -425.42) * mm, "end": v(1640.08, -425.42) * mm});
            skLineSegment(sketch, "E49.0.13.1", {"start": v(1640.08, -428.6) * mm, "end": v(1652.78, -428.6) * mm});
            skLineSegment(sketch, "E49.0.13.2", {"start": v(1652.78, -428.6) * mm, "end": v(1652.78, -425.42) * mm});
            skLineSegment(sketch, "E49.0.13.3", {"start": v(1640.08, -425.42) * mm, "end": v(1640.08, -422.24) * mm});
            skLineSegment(sketch, "E49.0.14.0", {"start": v(1652.78, -419.07) * mm, "end": v(1640.08, -419.07) * mm});
            skLineSegment(sketch, "E49.0.14.1", {"start": v(1640.08, -422.24) * mm, "end": v(1652.78, -422.24) * mm});
            skLineSegment(sketch, "E49.0.14.2", {"start": v(1652.78, -422.24) * mm, "end": v(1652.78, -419.07) * mm});
            skLineSegment(sketch, "E49.0.14.3", {"start": v(1640.08, -419.07) * mm, "end": v(1640.08, -415.9) * mm});
            skLineSegment(sketch, "E49.0.15.0", {"start": v(1652.78, -412.72) * mm, "end": v(1640.08, -412.72) * mm});
            skLineSegment(sketch, "E49.0.15.1", {"start": v(1640.08, -415.9) * mm, "end": v(1652.78, -415.9) * mm});
            skLineSegment(sketch, "E49.0.15.2", {"start": v(1652.78, -415.9) * mm, "end": v(1652.78, -412.72) * mm});
            skLineSegment(sketch, "E49.0.15.3", {"start": v(1640.08, -412.72) * mm, "end": v(1640.08, -409.54) * mm});
            skLineSegment(sketch, "E49.0.16.0", {"start": v(1652.78, -406.37) * mm, "end": v(1640.08, -406.37) * mm});
            skLineSegment(sketch, "E49.0.16.1", {"start": v(1640.08, -409.54) * mm, "end": v(1652.78, -409.54) * mm});
            skLineSegment(sketch, "E49.0.16.2", {"start": v(1652.78, -409.54) * mm, "end": v(1652.78, -406.37) * mm});
            skLineSegment(sketch, "E49.0.16.3", {"start": v(1640.08, -406.37) * mm, "end": v(1640.08, -403.2) * mm});
            skLineSegment(sketch, "E49.0.17.0", {"start": v(1652.78, -400.02) * mm, "end": v(1640.08, -400.02) * mm});
            skLineSegment(sketch, "E49.0.17.1", {"start": v(1640.08, -403.2) * mm, "end": v(1652.78, -403.2) * mm});
            skLineSegment(sketch, "E49.0.17.2", {"start": v(1652.78, -403.2) * mm, "end": v(1652.78, -400.02) * mm});
            skLineSegment(sketch, "E49.0.17.3", {"start": v(1640.08, -400.02) * mm, "end": v(1640.08, -396.84) * mm});
            skLineSegment(sketch, "E49.0.18.0", {"start": v(1652.78, -393.67) * mm, "end": v(1640.08, -393.67) * mm});
            skLineSegment(sketch, "E49.0.18.1", {"start": v(1640.08, -396.84) * mm, "end": v(1652.78, -396.84) * mm});
            skLineSegment(sketch, "E49.0.18.2", {"start": v(1652.78, -396.84) * mm, "end": v(1652.78, -393.67) * mm});
            skLineSegment(sketch, "E49.0.18.3", {"start": v(1640.08, -393.67) * mm, "end": v(1640.08, -390.5) * mm});
            skLineSegment(sketch, "E49.0.19.0", {"start": v(1652.78, -387.32) * mm, "end": v(1640.08, -387.32) * mm});
            skLineSegment(sketch, "E49.0.19.1", {"start": v(1640.08, -390.5) * mm, "end": v(1652.78, -390.5) * mm});
            skLineSegment(sketch, "E49.0.19.2", {"start": v(1652.78, -390.5) * mm, "end": v(1652.78, -387.32) * mm});
            skLineSegment(sketch, "E49.0.19.3", {"start": v(1640.08, -387.32) * mm, "end": v(1640.08, -384.14) * mm});
            skLineSegment(sketch, "E49.0.20.0", {"start": v(1652.78, -380.97) * mm, "end": v(1640.08, -380.97) * mm});
            skLineSegment(sketch, "E49.0.20.1", {"start": v(1640.08, -384.14) * mm, "end": v(1652.78, -384.14) * mm});
            skLineSegment(sketch, "E49.0.20.2", {"start": v(1652.78, -384.14) * mm, "end": v(1652.78, -380.97) * mm});
            skLineSegment(sketch, "E49.0.20.3", {"start": v(1640.08, -380.97) * mm, "end": v(1640.08, -377.8) * mm});
            skLineSegment(sketch, "E49.0.21.0", {"start": v(1652.78, -374.62) * mm, "end": v(1640.08, -374.62) * mm});
            skLineSegment(sketch, "E49.0.21.1", {"start": v(1640.08, -377.8) * mm, "end": v(1652.78, -377.8) * mm});
            skLineSegment(sketch, "E49.0.21.2", {"start": v(1652.78, -377.8) * mm, "end": v(1652.78, -374.62) * mm});
            skLineSegment(sketch, "E49.0.21.3", {"start": v(1640.08, -374.62) * mm, "end": v(1640.08, -371.44) * mm});
            skLineSegment(sketch, "E49.direction1", {"start": v(1640.08, -511.14) * mm, "end": v(1665.48, -511.14) * mm, "construction": true});
            skLineSegment(sketch, "E49.direction2", {"start": v(1640.08, -511.14) * mm, "end": v(1640.08, -504.8) * mm, "construction": true});
            skLineSegment(sketch, "E50.0.1.0", {"start": v(836.8, -377.8) * mm, "end": v(824.1, -377.8) * mm});
            skLineSegment(sketch, "E50.0.1.1", {"start": v(824.1, -380.97) * mm, "end": v(836.8, -380.97) * mm});
            skLineSegment(sketch, "E50.0.1.2", {"start": v(836.8, -380.97) * mm, "end": v(836.8, -384.14) * mm});
            skLineSegment(sketch, "E50.0.1.3", {"start": v(824.1, -377.8) * mm, "end": v(824.1, -380.97) * mm});
            skLineSegment(sketch, "E50.0.2.0", {"start": v(836.8, -384.14) * mm, "end": v(824.1, -384.14) * mm});
            skLineSegment(sketch, "E50.0.2.1", {"start": v(824.1, -387.32) * mm, "end": v(836.8, -387.32) * mm});
            skLineSegment(sketch, "E50.0.2.2", {"start": v(836.8, -387.32) * mm, "end": v(836.8, -390.5) * mm});
            skLineSegment(sketch, "E50.0.2.3", {"start": v(824.1, -384.14) * mm, "end": v(824.1, -387.32) * mm});
            skLineSegment(sketch, "E50.0.3.0", {"start": v(836.8, -390.5) * mm, "end": v(824.1, -390.5) * mm});
            skLineSegment(sketch, "E50.0.3.1", {"start": v(824.1, -393.67) * mm, "end": v(836.8, -393.67) * mm});
            skLineSegment(sketch, "E50.0.3.2", {"start": v(836.8, -393.67) * mm, "end": v(836.8, -396.84) * mm});
            skLineSegment(sketch, "E50.0.3.3", {"start": v(824.1, -390.5) * mm, "end": v(824.1, -393.67) * mm});
            skLineSegment(sketch, "E50.0.4.0", {"start": v(836.8, -396.84) * mm, "end": v(824.1, -396.84) * mm});
            skLineSegment(sketch, "E50.0.4.1", {"start": v(824.1, -400.02) * mm, "end": v(836.8, -400.02) * mm});
            skLineSegment(sketch, "E50.0.4.2", {"start": v(836.8, -400.02) * mm, "end": v(836.8, -403.2) * mm});
            skLineSegment(sketch, "E50.0.4.3", {"start": v(824.1, -396.84) * mm, "end": v(824.1, -400.02) * mm});
            skLineSegment(sketch, "E50.0.5.0", {"start": v(836.8, -403.2) * mm, "end": v(824.1, -403.2) * mm});
            skLineSegment(sketch, "E50.0.5.1", {"start": v(824.1, -406.37) * mm, "end": v(836.8, -406.37) * mm});
            skLineSegment(sketch, "E50.0.5.2", {"start": v(836.8, -406.37) * mm, "end": v(836.8, -409.54) * mm});
            skLineSegment(sketch, "E50.0.5.3", {"start": v(824.1, -403.2) * mm, "end": v(824.1, -406.37) * mm});
            skLineSegment(sketch, "E50.0.6.0", {"start": v(836.8, -409.54) * mm, "end": v(824.1, -409.54) * mm});
            skLineSegment(sketch, "E50.0.6.1", {"start": v(824.1, -412.72) * mm, "end": v(836.8, -412.72) * mm});
            skLineSegment(sketch, "E50.0.6.2", {"start": v(836.8, -412.72) * mm, "end": v(836.8, -415.9) * mm});
            skLineSegment(sketch, "E50.0.6.3", {"start": v(824.1, -409.54) * mm, "end": v(824.1, -412.72) * mm});
            skLineSegment(sketch, "E50.0.7.0", {"start": v(836.8, -415.9) * mm, "end": v(824.1, -415.9) * mm});
            skLineSegment(sketch, "E50.0.7.1", {"start": v(824.1, -419.07) * mm, "end": v(836.8, -419.07) * mm});
            skLineSegment(sketch, "E50.0.7.2", {"start": v(836.8, -419.07) * mm, "end": v(836.8, -422.24) * mm});
            skLineSegment(sketch, "E50.0.7.3", {"start": v(824.1, -415.9) * mm, "end": v(824.1, -419.07) * mm});
            skLineSegment(sketch, "E50.0.8.0", {"start": v(836.8, -422.24) * mm, "end": v(824.1, -422.24) * mm});
            skLineSegment(sketch, "E50.0.8.1", {"start": v(824.1, -425.42) * mm, "end": v(836.8, -425.42) * mm});
            skLineSegment(sketch, "E50.0.8.2", {"start": v(836.8, -425.42) * mm, "end": v(836.8, -428.6) * mm});
            skLineSegment(sketch, "E50.0.8.3", {"start": v(824.1, -422.24) * mm, "end": v(824.1, -425.42) * mm});
            skLineSegment(sketch, "E50.0.9.0", {"start": v(836.8, -428.6) * mm, "end": v(824.1, -428.6) * mm});
            skLineSegment(sketch, "E50.0.9.1", {"start": v(824.1, -431.77) * mm, "end": v(836.8, -431.77) * mm});
            skLineSegment(sketch, "E50.0.9.2", {"start": v(836.8, -431.77) * mm, "end": v(836.8, -434.94) * mm});
            skLineSegment(sketch, "E50.0.9.3", {"start": v(824.1, -428.6) * mm, "end": v(824.1, -431.77) * mm});
            skLineSegment(sketch, "E50.0.10.0", {"start": v(836.8, -434.94) * mm, "end": v(824.1, -434.94) * mm});
            skLineSegment(sketch, "E50.0.10.1", {"start": v(824.1, -438.12) * mm, "end": v(836.8, -438.12) * mm});
            skLineSegment(sketch, "E50.0.10.2", {"start": v(836.8, -438.12) * mm, "end": v(836.8, -441.3) * mm});
            skLineSegment(sketch, "E50.0.10.3", {"start": v(824.1, -434.94) * mm, "end": v(824.1, -438.12) * mm});
            skLineSegment(sketch, "E50.0.11.0", {"start": v(836.8, -441.3) * mm, "end": v(824.1, -441.3) * mm});
            skLineSegment(sketch, "E50.0.11.1", {"start": v(824.1, -444.47) * mm, "end": v(836.8, -444.47) * mm});
            skLineSegment(sketch, "E50.0.11.2", {"start": v(836.8, -444.47) * mm, "end": v(836.8, -447.64) * mm});
            skLineSegment(sketch, "E50.0.11.3", {"start": v(824.1, -441.3) * mm, "end": v(824.1, -444.47) * mm});
            skLineSegment(sketch, "E50.0.12.0", {"start": v(836.8, -447.64) * mm, "end": v(824.1, -447.64) * mm});
            skLineSegment(sketch, "E50.0.12.1", {"start": v(824.1, -450.82) * mm, "end": v(836.8, -450.82) * mm});
            skLineSegment(sketch, "E50.0.12.2", {"start": v(836.8, -450.82) * mm, "end": v(836.8, -454) * mm});
            skLineSegment(sketch, "E50.0.12.3", {"start": v(824.1, -447.64) * mm, "end": v(824.1, -450.82) * mm});
            skLineSegment(sketch, "E50.0.13.0", {"start": v(836.8, -454) * mm, "end": v(824.1, -454) * mm});
            skLineSegment(sketch, "E50.0.13.1", {"start": v(824.1, -457.17) * mm, "end": v(836.8, -457.17) * mm});
            skLineSegment(sketch, "E50.0.13.2", {"start": v(836.8, -457.17) * mm, "end": v(836.8, -460.34) * mm});
            skLineSegment(sketch, "E50.0.13.3", {"start": v(824.1, -454) * mm, "end": v(824.1, -457.17) * mm});
            skLineSegment(sketch, "E50.0.14.0", {"start": v(836.8, -460.34) * mm, "end": v(824.1, -460.34) * mm});
            skLineSegment(sketch, "E50.0.14.1", {"start": v(824.1, -463.52) * mm, "end": v(836.8, -463.52) * mm});
            skLineSegment(sketch, "E50.0.14.2", {"start": v(836.8, -463.52) * mm, "end": v(836.8, -466.7) * mm});
            skLineSegment(sketch, "E50.0.14.3", {"start": v(824.1, -460.34) * mm, "end": v(824.1, -463.52) * mm});
            skLineSegment(sketch, "E50.0.15.0", {"start": v(836.8, -466.7) * mm, "end": v(824.1, -466.7) * mm});
            skLineSegment(sketch, "E50.0.15.1", {"start": v(824.1, -469.87) * mm, "end": v(836.8, -469.87) * mm});
            skLineSegment(sketch, "E50.0.15.2", {"start": v(836.8, -469.87) * mm, "end": v(836.8, -473.04) * mm});
            skLineSegment(sketch, "E50.0.15.3", {"start": v(824.1, -466.7) * mm, "end": v(824.1, -469.87) * mm});
            skLineSegment(sketch, "E50.0.16.0", {"start": v(836.8, -473.04) * mm, "end": v(824.1, -473.04) * mm});
            skLineSegment(sketch, "E50.0.16.1", {"start": v(824.1, -476.22) * mm, "end": v(836.8, -476.22) * mm});
            skLineSegment(sketch, "E50.0.16.2", {"start": v(836.8, -476.22) * mm, "end": v(836.8, -479.4) * mm});
            skLineSegment(sketch, "E50.0.16.3", {"start": v(824.1, -473.04) * mm, "end": v(824.1, -476.22) * mm});
            skLineSegment(sketch, "E50.0.17.0", {"start": v(836.8, -479.4) * mm, "end": v(824.1, -479.4) * mm});
            skLineSegment(sketch, "E50.0.17.1", {"start": v(824.1, -482.57) * mm, "end": v(836.8, -482.57) * mm});
            skLineSegment(sketch, "E50.0.17.2", {"start": v(836.8, -482.57) * mm, "end": v(836.8, -485.74) * mm});
            skLineSegment(sketch, "E50.0.17.3", {"start": v(824.1, -479.4) * mm, "end": v(824.1, -482.57) * mm});
            skLineSegment(sketch, "E50.0.18.0", {"start": v(836.8, -485.74) * mm, "end": v(824.1, -485.74) * mm});
            skLineSegment(sketch, "E50.0.18.1", {"start": v(824.1, -488.92) * mm, "end": v(836.8, -488.92) * mm});
            skLineSegment(sketch, "E50.0.18.2", {"start": v(836.8, -488.92) * mm, "end": v(836.8, -492.1) * mm});
            skLineSegment(sketch, "E50.0.18.3", {"start": v(824.1, -485.74) * mm, "end": v(824.1, -488.92) * mm});
            skLineSegment(sketch, "E50.0.19.0", {"start": v(836.8, -492.1) * mm, "end": v(824.1, -492.1) * mm});
            skLineSegment(sketch, "E50.0.19.1", {"start": v(824.1, -495.27) * mm, "end": v(836.8, -495.27) * mm});
            skLineSegment(sketch, "E50.0.19.2", {"start": v(836.8, -495.27) * mm, "end": v(836.8, -498.44) * mm});
            skLineSegment(sketch, "E50.0.19.3", {"start": v(824.1, -492.1) * mm, "end": v(824.1, -495.27) * mm});
            skLineSegment(sketch, "E50.0.20.0", {"start": v(836.8, -498.44) * mm, "end": v(824.1, -498.44) * mm});
            skLineSegment(sketch, "E50.0.20.1", {"start": v(824.1, -501.62) * mm, "end": v(836.8, -501.62) * mm});
            skLineSegment(sketch, "E50.0.20.2", {"start": v(836.8, -501.62) * mm, "end": v(836.8, -504.8) * mm});
            skLineSegment(sketch, "E50.0.20.3", {"start": v(824.1, -498.44) * mm, "end": v(824.1, -501.62) * mm});
            skLineSegment(sketch, "E50.0.21.0", {"start": v(836.8, -504.8) * mm, "end": v(824.1, -504.8) * mm});
            skLineSegment(sketch, "E50.0.21.1", {"start": v(824.1, -507.97) * mm, "end": v(836.8, -507.97) * mm});
            skLineSegment(sketch, "E50.0.21.2", {"start": v(836.8, -507.97) * mm, "end": v(836.8, -511.14) * mm});
            skLineSegment(sketch, "E50.0.21.3", {"start": v(824.1, -504.8) * mm, "end": v(824.1, -507.97) * mm});
            skLineSegment(sketch, "E50.direction1", {"start": v(824.1, -374.62) * mm, "end": v(849.5, -374.62) * mm, "construction": true});
            skLineSegment(sketch, "E50.direction2", {"start": v(824.1, -374.62) * mm, "end": v(824.1, -380.97) * mm, "construction": true});
            skSolve(sketch);
        }
        {
            var Q0;
            Q0 = qSketchRegion(id + "F6", true);
            extrude(context, id + "F7", {"entities" : qUnion([Q0]), "depth" : 12.7 * mm});
        }
        {
            var Q0;
            Q0=qCreatedBy(makeId("Right.planeOp"),FACE);
            var sketch = newSketch(context, id + "F8", { "sketchPlane" : qUnion([Q0])});
            skLineSegment(sketch, "E51.top", {"start": v(483.61, -940.76) * mm, "end": v(1286.89, -940.76) * mm});
            skLineSegment(sketch, "E51.left", {"start": v(483.61, -801.06) * mm, "end": v(483.61, -940.76) * mm});
            skLineSegment(sketch, "E51.right", {"start": v(1286.89, -801.06) * mm, "end": v(1286.89, -940.76) * mm});
            skLineSegment(sketch, "E52", {"start": v(483.61, -801.06) * mm, "end": v(470.91, -801.06) * mm});
            skLineSegment(sketch, "E53", {"start": v(470.91, -801.06) * mm, "end": v(470.91, -804.24) * mm});
            skLineSegment(sketch, "E54", {"start": v(470.91, -804.24) * mm, "end": v(483.61, -804.24) * mm});
            skLineSegment(sketch, "E55", {"start": v(483.61, -804.24) * mm, "end": v(483.61, -807.41) * mm});
            skLineSegment(sketch, "E56", {"start": v(1286.89, -940.76) * mm, "end": v(1299.59, -940.76) * mm});
            skLineSegment(sketch, "E57", {"start": v(1299.59, -940.76) * mm, "end": v(1299.59, -937.59) * mm});
            skLineSegment(sketch, "E58", {"start": v(1299.59, -937.59) * mm, "end": v(1286.89, -937.59) * mm});
            skLineSegment(sketch, "E59", {"start": v(1286.89, -937.59) * mm, "end": v(1286.89, -934.41) * mm});
            skLineSegment(sketch, "E60.0.1.0", {"start": v(1299.59, -931.24) * mm, "end": v(1286.89, -931.24) * mm});
            skLineSegment(sketch, "E60.0.1.1", {"start": v(1286.89, -934.41) * mm, "end": v(1299.59, -934.41) * mm});
            skLineSegment(sketch, "E60.0.1.2", {"start": v(1299.59, -934.41) * mm, "end": v(1299.59, -931.24) * mm});
            skLineSegment(sketch, "E60.0.1.3", {"start": v(1286.89, -931.24) * mm, "end": v(1286.89, -928.06) * mm});
            skLineSegment(sketch, "E60.0.2.0", {"start": v(1299.59, -924.89) * mm, "end": v(1286.89, -924.89) * mm});
            skLineSegment(sketch, "E60.0.2.1", {"start": v(1286.89, -928.06) * mm, "end": v(1299.59, -928.06) * mm});
            skLineSegment(sketch, "E60.0.2.2", {"start": v(1299.59, -928.06) * mm, "end": v(1299.59, -924.89) * mm});
            skLineSegment(sketch, "E60.0.2.3", {"start": v(1286.89, -924.89) * mm, "end": v(1286.89, -921.71) * mm});
            skLineSegment(sketch, "E60.0.3.0", {"start": v(1299.59, -918.54) * mm, "end": v(1286.89, -918.54) * mm});
            skLineSegment(sketch, "E60.0.3.1", {"start": v(1286.89, -921.71) * mm, "end": v(1299.59, -921.71) * mm});
            skLineSegment(sketch, "E60.0.3.2", {"start": v(1299.59, -921.71) * mm, "end": v(1299.59, -918.54) * mm});
            skLineSegment(sketch, "E60.0.3.3", {"start": v(1286.89, -918.54) * mm, "end": v(1286.89, -915.36) * mm});
            skLineSegment(sketch, "E60.0.4.0", {"start": v(1299.59, -912.19) * mm, "end": v(1286.89, -912.19) * mm});
            skLineSegment(sketch, "E60.0.4.1", {"start": v(1286.89, -915.36) * mm, "end": v(1299.59, -915.36) * mm});
            skLineSegment(sketch, "E60.0.4.2", {"start": v(1299.59, -915.36) * mm, "end": v(1299.59, -912.19) * mm});
            skLineSegment(sketch, "E60.0.4.3", {"start": v(1286.89, -912.19) * mm, "end": v(1286.89, -909.01) * mm});
            skLineSegment(sketch, "E60.0.5.0", {"start": v(1299.59, -905.84) * mm, "end": v(1286.89, -905.84) * mm});
            skLineSegment(sketch, "E60.0.5.1", {"start": v(1286.89, -909.01) * mm, "end": v(1299.59, -909.01) * mm});
            skLineSegment(sketch, "E60.0.5.2", {"start": v(1299.59, -909.01) * mm, "end": v(1299.59, -905.84) * mm});
            skLineSegment(sketch, "E60.0.5.3", {"start": v(1286.89, -905.84) * mm, "end": v(1286.89, -902.66) * mm});
            skLineSegment(sketch, "E60.0.6.0", {"start": v(1299.59, -899.49) * mm, "end": v(1286.89, -899.49) * mm});
            skLineSegment(sketch, "E60.0.6.1", {"start": v(1286.89, -902.66) * mm, "end": v(1299.59, -902.66) * mm});
            skLineSegment(sketch, "E60.0.6.2", {"start": v(1299.59, -902.66) * mm, "end": v(1299.59, -899.49) * mm});
            skLineSegment(sketch, "E60.0.6.3", {"start": v(1286.89, -899.49) * mm, "end": v(1286.89, -896.31) * mm});
            skLineSegment(sketch, "E60.0.7.0", {"start": v(1299.59, -893.14) * mm, "end": v(1286.89, -893.14) * mm});
            skLineSegment(sketch, "E60.0.7.1", {"start": v(1286.89, -896.31) * mm, "end": v(1299.59, -896.31) * mm});
            skLineSegment(sketch, "E60.0.7.2", {"start": v(1299.59, -896.31) * mm, "end": v(1299.59, -893.14) * mm});
            skLineSegment(sketch, "E60.0.7.3", {"start": v(1286.89, -893.14) * mm, "end": v(1286.89, -889.96) * mm});
            skLineSegment(sketch, "E60.0.8.0", {"start": v(1299.59, -886.79) * mm, "end": v(1286.89, -886.79) * mm});
            skLineSegment(sketch, "E60.0.8.1", {"start": v(1286.89, -889.96) * mm, "end": v(1299.59, -889.96) * mm});
            skLineSegment(sketch, "E60.0.8.2", {"start": v(1299.59, -889.96) * mm, "end": v(1299.59, -886.79) * mm});
            skLineSegment(sketch, "E60.0.8.3", {"start": v(1286.89, -886.79) * mm, "end": v(1286.89, -883.61) * mm});
            skLineSegment(sketch, "E60.0.9.0", {"start": v(1299.59, -880.44) * mm, "end": v(1286.89, -880.44) * mm});
            skLineSegment(sketch, "E60.0.9.1", {"start": v(1286.89, -883.61) * mm, "end": v(1299.59, -883.61) * mm});
            skLineSegment(sketch, "E60.0.9.2", {"start": v(1299.59, -883.61) * mm, "end": v(1299.59, -880.44) * mm});
            skLineSegment(sketch, "E60.0.9.3", {"start": v(1286.89, -880.44) * mm, "end": v(1286.89, -877.26) * mm});
            skLineSegment(sketch, "E60.0.10.0", {"start": v(1299.59, -874.09) * mm, "end": v(1286.89, -874.09) * mm});
            skLineSegment(sketch, "E60.0.10.1", {"start": v(1286.89, -877.26) * mm, "end": v(1299.59, -877.26) * mm});
            skLineSegment(sketch, "E60.0.10.2", {"start": v(1299.59, -877.26) * mm, "end": v(1299.59, -874.09) * mm});
            skLineSegment(sketch, "E60.0.10.3", {"start": v(1286.89, -874.09) * mm, "end": v(1286.89, -870.91) * mm});
            skLineSegment(sketch, "E60.0.11.0", {"start": v(1299.59, -867.74) * mm, "end": v(1286.89, -867.74) * mm});
            skLineSegment(sketch, "E60.0.11.1", {"start": v(1286.89, -870.91) * mm, "end": v(1299.59, -870.91) * mm});
            skLineSegment(sketch, "E60.0.11.2", {"start": v(1299.59, -870.91) * mm, "end": v(1299.59, -867.74) * mm});
            skLineSegment(sketch, "E60.0.11.3", {"start": v(1286.89, -867.74) * mm, "end": v(1286.89, -864.56) * mm});
            skLineSegment(sketch, "E60.0.12.0", {"start": v(1299.59, -861.39) * mm, "end": v(1286.89, -861.39) * mm});
            skLineSegment(sketch, "E60.0.12.1", {"start": v(1286.89, -864.56) * mm, "end": v(1299.59, -864.56) * mm});
            skLineSegment(sketch, "E60.0.12.2", {"start": v(1299.59, -864.56) * mm, "end": v(1299.59, -861.39) * mm});
            skLineSegment(sketch, "E60.0.12.3", {"start": v(1286.89, -861.39) * mm, "end": v(1286.89, -858.21) * mm});
            skLineSegment(sketch, "E60.0.13.0", {"start": v(1299.59, -855.04) * mm, "end": v(1286.89, -855.04) * mm});
            skLineSegment(sketch, "E60.0.13.1", {"start": v(1286.89, -858.21) * mm, "end": v(1299.59, -858.21) * mm});
            skLineSegment(sketch, "E60.0.13.2", {"start": v(1299.59, -858.21) * mm, "end": v(1299.59, -855.04) * mm});
            skLineSegment(sketch, "E60.0.13.3", {"start": v(1286.89, -855.04) * mm, "end": v(1286.89, -851.86) * mm});
            skLineSegment(sketch, "E60.0.14.0", {"start": v(1299.59, -848.69) * mm, "end": v(1286.89, -848.69) * mm});
            skLineSegment(sketch, "E60.0.14.1", {"start": v(1286.89, -851.86) * mm, "end": v(1299.59, -851.86) * mm});
            skLineSegment(sketch, "E60.0.14.2", {"start": v(1299.59, -851.86) * mm, "end": v(1299.59, -848.69) * mm});
            skLineSegment(sketch, "E60.0.14.3", {"start": v(1286.89, -848.69) * mm, "end": v(1286.89, -845.51) * mm});
            skLineSegment(sketch, "E60.0.15.0", {"start": v(1299.59, -842.34) * mm, "end": v(1286.89, -842.34) * mm});
            skLineSegment(sketch, "E60.0.15.1", {"start": v(1286.89, -845.51) * mm, "end": v(1299.59, -845.51) * mm});
            skLineSegment(sketch, "E60.0.15.2", {"start": v(1299.59, -845.51) * mm, "end": v(1299.59, -842.34) * mm});
            skLineSegment(sketch, "E60.0.15.3", {"start": v(1286.89, -842.34) * mm, "end": v(1286.89, -839.16) * mm});
            skLineSegment(sketch, "E60.0.16.0", {"start": v(1299.59, -835.99) * mm, "end": v(1286.89, -835.99) * mm});
            skLineSegment(sketch, "E60.0.16.1", {"start": v(1286.89, -839.16) * mm, "end": v(1299.59, -839.16) * mm});
            skLineSegment(sketch, "E60.0.16.2", {"start": v(1299.59, -839.16) * mm, "end": v(1299.59, -835.99) * mm});
            skLineSegment(sketch, "E60.0.16.3", {"start": v(1286.89, -835.99) * mm, "end": v(1286.89, -832.81) * mm});
            skLineSegment(sketch, "E60.0.17.0", {"start": v(1299.59, -829.64) * mm, "end": v(1286.89, -829.64) * mm});
            skLineSegment(sketch, "E60.0.17.1", {"start": v(1286.89, -832.81) * mm, "end": v(1299.59, -832.81) * mm});
            skLineSegment(sketch, "E60.0.17.2", {"start": v(1299.59, -832.81) * mm, "end": v(1299.59, -829.64) * mm});
            skLineSegment(sketch, "E60.0.17.3", {"start": v(1286.89, -829.64) * mm, "end": v(1286.89, -826.46) * mm});
            skLineSegment(sketch, "E60.0.18.0", {"start": v(1299.59, -823.29) * mm, "end": v(1286.89, -823.29) * mm});
            skLineSegment(sketch, "E60.0.18.1", {"start": v(1286.89, -826.46) * mm, "end": v(1299.59, -826.46) * mm});
            skLineSegment(sketch, "E60.0.18.2", {"start": v(1299.59, -826.46) * mm, "end": v(1299.59, -823.29) * mm});
            skLineSegment(sketch, "E60.0.18.3", {"start": v(1286.89, -823.29) * mm, "end": v(1286.89, -820.11) * mm});
            skLineSegment(sketch, "E60.0.19.0", {"start": v(1299.59, -816.94) * mm, "end": v(1286.89, -816.94) * mm});
            skLineSegment(sketch, "E60.0.19.1", {"start": v(1286.89, -820.11) * mm, "end": v(1299.59, -820.11) * mm});
            skLineSegment(sketch, "E60.0.19.2", {"start": v(1299.59, -820.11) * mm, "end": v(1299.59, -816.94) * mm});
            skLineSegment(sketch, "E60.0.19.3", {"start": v(1286.89, -816.94) * mm, "end": v(1286.89, -813.76) * mm});
            skLineSegment(sketch, "E60.0.20.0", {"start": v(1299.59, -810.59) * mm, "end": v(1286.89, -810.59) * mm});
            skLineSegment(sketch, "E60.0.20.1", {"start": v(1286.89, -813.76) * mm, "end": v(1299.59, -813.76) * mm});
            skLineSegment(sketch, "E60.0.20.2", {"start": v(1299.59, -813.76) * mm, "end": v(1299.59, -810.59) * mm});
            skLineSegment(sketch, "E60.0.20.3", {"start": v(1286.89, -810.59) * mm, "end": v(1286.89, -807.41) * mm});
            skLineSegment(sketch, "E60.0.21.0", {"start": v(1299.59, -804.24) * mm, "end": v(1286.89, -804.24) * mm});
            skLineSegment(sketch, "E60.0.21.1", {"start": v(1286.89, -807.41) * mm, "end": v(1299.59, -807.41) * mm});
            skLineSegment(sketch, "E60.0.21.2", {"start": v(1299.59, -807.41) * mm, "end": v(1299.59, -804.24) * mm});
            skLineSegment(sketch, "E60.0.21.3", {"start": v(1286.89, -804.24) * mm, "end": v(1286.89, -801.06) * mm});
            skLineSegment(sketch, "E60.direction1", {"start": v(1286.89, -940.76) * mm, "end": v(1312.29, -940.76) * mm, "construction": true});
            skLineSegment(sketch, "E60.direction2", {"start": v(1286.89, -940.76) * mm, "end": v(1286.89, -934.41) * mm, "construction": true});
            skLineSegment(sketch, "E61.0.1.0", {"start": v(483.61, -807.41) * mm, "end": v(470.91, -807.41) * mm});
            skLineSegment(sketch, "E61.0.1.1", {"start": v(470.91, -810.59) * mm, "end": v(483.61, -810.59) * mm});
            skLineSegment(sketch, "E61.0.1.2", {"start": v(483.61, -810.59) * mm, "end": v(483.61, -813.76) * mm});
            skLineSegment(sketch, "E61.0.1.3", {"start": v(470.91, -807.41) * mm, "end": v(470.91, -810.59) * mm});
            skLineSegment(sketch, "E61.0.2.0", {"start": v(483.61, -813.76) * mm, "end": v(470.91, -813.76) * mm});
            skLineSegment(sketch, "E61.0.2.1", {"start": v(470.91, -816.94) * mm, "end": v(483.61, -816.94) * mm});
            skLineSegment(sketch, "E61.0.2.2", {"start": v(483.61, -816.94) * mm, "end": v(483.61, -820.11) * mm});
            skLineSegment(sketch, "E61.0.2.3", {"start": v(470.91, -813.76) * mm, "end": v(470.91, -816.94) * mm});
            skLineSegment(sketch, "E61.0.3.0", {"start": v(483.61, -820.11) * mm, "end": v(470.91, -820.11) * mm});
            skLineSegment(sketch, "E61.0.3.1", {"start": v(470.91, -823.29) * mm, "end": v(483.61, -823.29) * mm});
            skLineSegment(sketch, "E61.0.3.2", {"start": v(483.61, -823.29) * mm, "end": v(483.61, -826.46) * mm});
            skLineSegment(sketch, "E61.0.3.3", {"start": v(470.91, -820.11) * mm, "end": v(470.91, -823.29) * mm});
            skLineSegment(sketch, "E61.0.4.0", {"start": v(483.61, -826.46) * mm, "end": v(470.91, -826.46) * mm});
            skLineSegment(sketch, "E61.0.4.1", {"start": v(470.91, -829.64) * mm, "end": v(483.61, -829.64) * mm});
            skLineSegment(sketch, "E61.0.4.2", {"start": v(483.61, -829.64) * mm, "end": v(483.61, -832.81) * mm});
            skLineSegment(sketch, "E61.0.4.3", {"start": v(470.91, -826.46) * mm, "end": v(470.91, -829.64) * mm});
            skLineSegment(sketch, "E61.0.5.0", {"start": v(483.61, -832.81) * mm, "end": v(470.91, -832.81) * mm});
            skLineSegment(sketch, "E61.0.5.1", {"start": v(470.91, -835.99) * mm, "end": v(483.61, -835.99) * mm});
            skLineSegment(sketch, "E61.0.5.2", {"start": v(483.61, -835.99) * mm, "end": v(483.61, -839.16) * mm});
            skLineSegment(sketch, "E61.0.5.3", {"start": v(470.91, -832.81) * mm, "end": v(470.91, -835.99) * mm});
            skLineSegment(sketch, "E61.0.6.0", {"start": v(483.61, -839.16) * mm, "end": v(470.91, -839.16) * mm});
            skLineSegment(sketch, "E61.0.6.1", {"start": v(470.91, -842.34) * mm, "end": v(483.61, -842.34) * mm});
            skLineSegment(sketch, "E61.0.6.2", {"start": v(483.61, -842.34) * mm, "end": v(483.61, -845.51) * mm});
            skLineSegment(sketch, "E61.0.6.3", {"start": v(470.91, -839.16) * mm, "end": v(470.91, -842.34) * mm});
            skLineSegment(sketch, "E61.0.7.0", {"start": v(483.61, -845.51) * mm, "end": v(470.91, -845.51) * mm});
            skLineSegment(sketch, "E61.0.7.1", {"start": v(470.91, -848.69) * mm, "end": v(483.61, -848.69) * mm});
            skLineSegment(sketch, "E61.0.7.2", {"start": v(483.61, -848.69) * mm, "end": v(483.61, -851.86) * mm});
            skLineSegment(sketch, "E61.0.7.3", {"start": v(470.91, -845.51) * mm, "end": v(470.91, -848.69) * mm});
            skLineSegment(sketch, "E61.0.8.0", {"start": v(483.61, -851.86) * mm, "end": v(470.91, -851.86) * mm});
            skLineSegment(sketch, "E61.0.8.1", {"start": v(470.91, -855.04) * mm, "end": v(483.61, -855.04) * mm});
            skLineSegment(sketch, "E61.0.8.2", {"start": v(483.61, -855.04) * mm, "end": v(483.61, -858.21) * mm});
            skLineSegment(sketch, "E61.0.8.3", {"start": v(470.91, -851.86) * mm, "end": v(470.91, -855.04) * mm});
            skLineSegment(sketch, "E61.0.9.0", {"start": v(483.61, -858.21) * mm, "end": v(470.91, -858.21) * mm});
            skLineSegment(sketch, "E61.0.9.1", {"start": v(470.91, -861.39) * mm, "end": v(483.61, -861.39) * mm});
            skLineSegment(sketch, "E61.0.9.2", {"start": v(483.61, -861.39) * mm, "end": v(483.61, -864.56) * mm});
            skLineSegment(sketch, "E61.0.9.3", {"start": v(470.91, -858.21) * mm, "end": v(470.91, -861.39) * mm});
            skLineSegment(sketch, "E61.0.10.0", {"start": v(483.61, -864.56) * mm, "end": v(470.91, -864.56) * mm});
            skLineSegment(sketch, "E61.0.10.1", {"start": v(470.91, -867.74) * mm, "end": v(483.61, -867.74) * mm});
            skLineSegment(sketch, "E61.0.10.2", {"start": v(483.61, -867.74) * mm, "end": v(483.61, -870.91) * mm});
            skLineSegment(sketch, "E61.0.10.3", {"start": v(470.91, -864.56) * mm, "end": v(470.91, -867.74) * mm});
            skLineSegment(sketch, "E61.0.11.0", {"start": v(483.61, -870.91) * mm, "end": v(470.91, -870.91) * mm});
            skLineSegment(sketch, "E61.0.11.1", {"start": v(470.91, -874.09) * mm, "end": v(483.61, -874.09) * mm});
            skLineSegment(sketch, "E61.0.11.2", {"start": v(483.61, -874.09) * mm, "end": v(483.61, -877.26) * mm});
            skLineSegment(sketch, "E61.0.11.3", {"start": v(470.91, -870.91) * mm, "end": v(470.91, -874.09) * mm});
            skLineSegment(sketch, "E61.0.12.0", {"start": v(483.61, -877.26) * mm, "end": v(470.91, -877.26) * mm});
            skLineSegment(sketch, "E61.0.12.1", {"start": v(470.91, -880.44) * mm, "end": v(483.61, -880.44) * mm});
            skLineSegment(sketch, "E61.0.12.2", {"start": v(483.61, -880.44) * mm, "end": v(483.61, -883.61) * mm});
            skLineSegment(sketch, "E61.0.12.3", {"start": v(470.91, -877.26) * mm, "end": v(470.91, -880.44) * mm});
            skLineSegment(sketch, "E61.0.13.0", {"start": v(483.61, -883.61) * mm, "end": v(470.91, -883.61) * mm});
            skLineSegment(sketch, "E61.0.13.1", {"start": v(470.91, -886.79) * mm, "end": v(483.61, -886.79) * mm});
            skLineSegment(sketch, "E61.0.13.2", {"start": v(483.61, -886.79) * mm, "end": v(483.61, -889.96) * mm});
            skLineSegment(sketch, "E61.0.13.3", {"start": v(470.91, -883.61) * mm, "end": v(470.91, -886.79) * mm});
            skLineSegment(sketch, "E61.0.14.0", {"start": v(483.61, -889.96) * mm, "end": v(470.91, -889.96) * mm});
            skLineSegment(sketch, "E61.0.14.1", {"start": v(470.91, -893.14) * mm, "end": v(483.61, -893.14) * mm});
            skLineSegment(sketch, "E61.0.14.2", {"start": v(483.61, -893.14) * mm, "end": v(483.61, -896.31) * mm});
            skLineSegment(sketch, "E61.0.14.3", {"start": v(470.91, -889.96) * mm, "end": v(470.91, -893.14) * mm});
            skLineSegment(sketch, "E61.0.15.0", {"start": v(483.61, -896.31) * mm, "end": v(470.91, -896.31) * mm});
            skLineSegment(sketch, "E61.0.15.1", {"start": v(470.91, -899.49) * mm, "end": v(483.61, -899.49) * mm});
            skLineSegment(sketch, "E61.0.15.2", {"start": v(483.61, -899.49) * mm, "end": v(483.61, -902.66) * mm});
            skLineSegment(sketch, "E61.0.15.3", {"start": v(470.91, -896.31) * mm, "end": v(470.91, -899.49) * mm});
            skLineSegment(sketch, "E61.0.16.0", {"start": v(483.61, -902.66) * mm, "end": v(470.91, -902.66) * mm});
            skLineSegment(sketch, "E61.0.16.1", {"start": v(470.91, -905.84) * mm, "end": v(483.61, -905.84) * mm});
            skLineSegment(sketch, "E61.0.16.2", {"start": v(483.61, -905.84) * mm, "end": v(483.61, -909.01) * mm});
            skLineSegment(sketch, "E61.0.16.3", {"start": v(470.91, -902.66) * mm, "end": v(470.91, -905.84) * mm});
            skLineSegment(sketch, "E61.0.17.0", {"start": v(483.61, -909.01) * mm, "end": v(470.91, -909.01) * mm});
            skLineSegment(sketch, "E61.0.17.1", {"start": v(470.91, -912.19) * mm, "end": v(483.61, -912.19) * mm});
            skLineSegment(sketch, "E61.0.17.2", {"start": v(483.61, -912.19) * mm, "end": v(483.61, -915.36) * mm});
            skLineSegment(sketch, "E61.0.17.3", {"start": v(470.91, -909.01) * mm, "end": v(470.91, -912.19) * mm});
            skLineSegment(sketch, "E61.0.18.0", {"start": v(483.61, -915.36) * mm, "end": v(470.91, -915.36) * mm});
            skLineSegment(sketch, "E61.0.18.1", {"start": v(470.91, -918.54) * mm, "end": v(483.61, -918.54) * mm});
            skLineSegment(sketch, "E61.0.18.2", {"start": v(483.61, -918.54) * mm, "end": v(483.61, -921.71) * mm});
            skLineSegment(sketch, "E61.0.18.3", {"start": v(470.91, -915.36) * mm, "end": v(470.91, -918.54) * mm});
            skLineSegment(sketch, "E61.0.19.0", {"start": v(483.61, -921.71) * mm, "end": v(470.91, -921.71) * mm});
            skLineSegment(sketch, "E61.0.19.1", {"start": v(470.91, -924.89) * mm, "end": v(483.61, -924.89) * mm});
            skLineSegment(sketch, "E61.0.19.2", {"start": v(483.61, -924.89) * mm, "end": v(483.61, -928.06) * mm});
            skLineSegment(sketch, "E61.0.19.3", {"start": v(470.91, -921.71) * mm, "end": v(470.91, -924.89) * mm});
            skLineSegment(sketch, "E61.0.20.0", {"start": v(483.61, -928.06) * mm, "end": v(470.91, -928.06) * mm});
            skLineSegment(sketch, "E61.0.20.1", {"start": v(470.91, -931.24) * mm, "end": v(483.61, -931.24) * mm});
            skLineSegment(sketch, "E61.0.20.2", {"start": v(483.61, -931.24) * mm, "end": v(483.61, -934.41) * mm});
            skLineSegment(sketch, "E61.0.20.3", {"start": v(470.91, -928.06) * mm, "end": v(470.91, -931.24) * mm});
            skLineSegment(sketch, "E61.0.21.0", {"start": v(483.61, -934.41) * mm, "end": v(470.91, -934.41) * mm});
            skLineSegment(sketch, "E61.0.21.1", {"start": v(470.91, -937.59) * mm, "end": v(483.61, -937.59) * mm});
            skLineSegment(sketch, "E61.0.21.2", {"start": v(483.61, -937.59) * mm, "end": v(483.61, -940.76) * mm});
            skLineSegment(sketch, "E61.0.21.3", {"start": v(470.91, -934.41) * mm, "end": v(470.91, -937.59) * mm});
            skLineSegment(sketch, "E61.direction1", {"start": v(470.91, -804.24) * mm, "end": v(499.49, -804.24) * mm, "construction": true});
            skLineSegment(sketch, "E61.direction2", {"start": v(470.91, -804.24) * mm, "end": v(470.91, -810.59) * mm, "construction": true});
            skLineSegment(sketch, "E62", {"start": v(483.61, -801.06) * mm, "end": v(583.46, -801.06) * mm});
            skLineSegment(sketch, "E63", {"start": v(612, -804.3) * mm, "end": v(652.68, -813.69) * mm});
            skLineSegment(sketch, "E64", {"start": v(681.22, -816.94) * mm, "end": v(1089.28, -816.94) * mm});
            skLineSegment(sketch, "E65", {"start": v(1117.82, -813.69) * mm, "end": v(1158.5, -804.3) * mm});
            skLineSegment(sketch, "E66", {"start": v(1187.04, -801.06) * mm, "end": v(1286.89, -801.06) * mm});
            skPoint(sketch, "E67.visualSharp", {"position": v(597.91, -801.06) * mm});
            skArc(sketch, "E67.filletArc", {"start": v(612, -804.3) * mm, "mid": v(597.82, -801.88) * mm, "end": v(583.46, -801.06) * mm});
            skPoint(sketch, "E68.visualSharp", {"position": v(666.76, -816.94) * mm});
            skArc(sketch, "E68.filletArc", {"start": v(652.68, -813.69) * mm, "mid": v(666.86, -816.12) * mm, "end": v(681.22, -816.94) * mm});
            skPoint(sketch, "E69.visualSharp", {"position": v(1103.73, -816.94) * mm});
            skArc(sketch, "E69.filletArc", {"start": v(1089.28, -816.94) * mm, "mid": v(1103.64, -816.12) * mm, "end": v(1117.82, -813.69) * mm});
            skPoint(sketch, "E70.visualSharp", {"position": v(1172.59, -801.06) * mm});
            skArc(sketch, "E70.filletArc", {"start": v(1187.04, -801.06) * mm, "mid": v(1172.68, -801.88) * mm, "end": v(1158.5, -804.3) * mm});
            skSolve(sketch);
        }
        {
            var Q0;
            Q0 = qSketchRegion(id + "F8", true);
            extrude(context, id + "F9", {"entities" : qUnion([Q0]), "depth" : 12.7 * mm});
        }
        {
            var Q0;
            Q0=qCreatedBy(makeId("Right.planeOp"),FACE);
            var sketch = newSketch(context, id + "F10", { "sketchPlane" : qUnion([Q0])});
            skLineSegment(sketch, "E71.bottom", {"start": v(315.23, -630.1) * mm, "end": v(321.58, -630.1) * mm});
            skLineSegment(sketch, "E71.top", {"start": v(315.23, -636.45) * mm, "end": v(321.58, -636.45) * mm});
            skLineSegment(sketch, "E71.left", {"start": v(315.23, -630.1) * mm, "end": v(315.23, -636.45) * mm});
            skLineSegment(sketch, "E71.right", {"start": v(321.58, -630.1) * mm, "end": v(321.58, -636.45) * mm});
            skSolve(sketch);
        }
        {
            var Q0;
            Q0 = qSketchRegion(id + "F10", true);
            extrude(context, id + "F11", {"entities" : qUnion([Q0]), "depth" : 723.9 * mm});
        }
        {
            var Q0;
            Q0=qCreatedBy(makeId("Right.planeOp"),FACE);
            var sketch = newSketch(context, id + "F12", { "sketchPlane" : qUnion([Q0])});
            skLineSegment(sketch, "E72.bottom", {"start": v(381.77, -543.52) * mm, "end": v(388.12, -543.52) * mm});
            skLineSegment(sketch, "E72.top", {"start": v(381.77, -549.87) * mm, "end": v(388.12, -549.87) * mm});
            skLineSegment(sketch, "E72.left", {"start": v(381.77, -543.52) * mm, "end": v(381.77, -549.87) * mm});
            skLineSegment(sketch, "E72.right", {"start": v(388.12, -543.52) * mm, "end": v(388.12, -549.87) * mm});
            skSolve(sketch);
        }
        {
            var Q0;
            Q0 = qSketchRegion(id + "F12", true);
            extrude(context, id + "F13", {"entities" : qUnion([Q0]), "depth" : 796.92 * mm});
        }
        {
            var Q0;
            Q0=qCreatedBy(makeId("Right.planeOp"),FACE);
            var sketch = newSketch(context, id + "F14", { "sketchPlane" : qUnion([Q0])});
            skLineSegment(sketch, "E73", {"start": v(271.9, -48.88) * mm, "end": v(322.7, -48.88) * mm});
            skLineSegment(sketch, "E74", {"start": v(322.7, -48.88) * mm, "end": v(322.7, 1.92) * mm});
            skLineSegment(sketch, "E75", {"start": v(271.9, -48.88) * mm, "end": v(271.9, -42.53) * mm});
            skLineSegment(sketch, "E76", {"start": v(271.9, -42.53) * mm, "end": v(316.35, -42.53) * mm});
            skLineSegment(sketch, "E77", {"start": v(316.35, -42.53) * mm, "end": v(316.35, 1.92) * mm});
            skLineSegment(sketch, "E78", {"start": v(316.35, 1.92) * mm, "end": v(322.7, 1.92) * mm});
            skSolve(sketch);
        }
        {
            var Q0;
            Q0 = qSketchRegion(id + "F14", true);
            extrude(context, id + "F15", {"entities" : qUnion([Q0]), "depth" : 2044.7 * mm});
        }
        {
            var Q0;
            Q0=qCreatedBy(makeId("Right.planeOp"),FACE);
            var sketch = newSketch(context, id + "F16", { "sketchPlane" : qUnion([Q0])});
            skLineSegment(sketch, "E79", {"start": v(106.9, 13.81) * mm, "end": v(157.7, 13.81) * mm});
            skLineSegment(sketch, "E80", {"start": v(157.7, 13.81) * mm, "end": v(157.7, 64.61) * mm});
            skLineSegment(sketch, "E81", {"start": v(106.9, 13.81) * mm, "end": v(106.9, 20.16) * mm});
            skLineSegment(sketch, "E82", {"start": v(106.9, 20.16) * mm, "end": v(151.36, 20.16) * mm});
            skLineSegment(sketch, "E83", {"start": v(151.36, 20.16) * mm, "end": v(151.36, 64.61) * mm});
            skLineSegment(sketch, "E84", {"start": v(151.36, 64.61) * mm, "end": v(157.7, 64.61) * mm});
            skSolve(sketch);
        }
        {
            var Q0;
            Q0 = qSketchRegion(id + "F16", true);
            extrude(context, id + "F17", {"entities" : qUnion([Q0]), "depth" : 768.35 * mm});
        }
        {
            var Q0;
            Q0=qCreatedBy(makeId("Top.planeOp"),FACE);
            var sketch = newSketch(context, id + "F18", { "sketchPlane" : qUnion([Q0])});
            skLineSegment(sketch, "E85.bottom", {"start": v(105.14, -13.36) * mm, "end": v(194.04, -13.36) * mm});
            skLineSegment(sketch, "E85.top", {"start": v(105.14, -102.26) * mm, "end": v(194.04, -102.26) * mm});
            skLineSegment(sketch, "E85.left", {"start": v(105.14, -13.36) * mm, "end": v(105.14, -102.26) * mm});
            skLineSegment(sketch, "E85.right", {"start": v(194.04, -13.36) * mm, "end": v(194.04, -102.26) * mm});
            skSolve(sketch);
        }
        {
            var Q0;
            Q0 = qSketchRegion(id + "F18", true);
            extrude(context, id + "F19", {"entities" : qUnion([Q0]), "depth" : 200.02 * mm});
        }
        {
            var Q0;
            Q0=qCreatedBy(makeId("Right.planeOp"),FACE);
            var sketch = newSketch(context, id + "F20", { "sketchPlane" : qUnion([Q0])});
            skLineSegment(sketch, "E86", {"start": v(82.84, -26.77) * mm, "end": v(185.97, -26.77) * mm});
            skLineSegment(sketch, "E87", {"start": v(185.97, -26.77) * mm, "end": v(185.97, -35.54) * mm});
            skLineSegment(sketch, "E88", {"start": v(185.97, -35.54) * mm, "end": v(137.96, -35.54) * mm});
            skLineSegment(sketch, "E89", {"start": v(137.96, -35.54) * mm, "end": v(137.96, -79.6) * mm});
            skLineSegment(sketch, "E90", {"start": v(137.96, -79.6) * mm, "end": v(130.85, -79.6) * mm});
            skLineSegment(sketch, "E91", {"start": v(130.85, -79.6) * mm, "end": v(130.85, -35.54) * mm});
            skLineSegment(sketch, "E92", {"start": v(130.85, -35.54) * mm, "end": v(82.84, -35.54) * mm});
            skLineSegment(sketch, "E93", {"start": v(82.84, -35.54) * mm, "end": v(82.84, -26.77) * mm});
            skSolve(sketch);
        }
        {
            var Q0;
            Q0 = qSketchRegion(id + "F20", true);
            extrude(context, id + "F21", {"entities" : qUnion([Q0]), "depth" : 2044.7 * mm});
        }
        {
            var Q0;
            Q0=makeQuery(id+"F15.opExtrude","CAP_EDGE",EDGE,{"disambiguationData":[OSD([sQuery(id+"F14.wireOp",EDGE,"E75")])],"isStart":false});
            var Q1;
            Q1=makeQuery(id+"F15.opExtrude","CAP_EDGE",EDGE,{"disambiguationData":[OSD([sQuery(id+"F14.wireOp",EDGE,"E75")])],"isStart":true});
            var Q2;
            Q2=makeQuery(id+"F17.opExtrude","CAP_EDGE",EDGE,{"disambiguationData":[OSD([sQuery(id+"F16.wireOp",EDGE,"E81")])],"isStart":false});
            var Q3;
            Q3=makeQuery(id+"F17.opExtrude","CAP_EDGE",EDGE,{"disambiguationData":[OSD([sQuery(id+"F16.wireOp",EDGE,"E81")])],"isStart":true});
            var Q4;
            Q4=makeQuery(id+"F21.opExtrude","CAP_EDGE",EDGE,{"disambiguationData":[OSD([sQuery(id+"F20.wireOp",EDGE,"E93")])],"isStart":false});
            var Q5;
            Q5=makeQuery(id+"F21.opExtrude","CAP_EDGE",EDGE,{"disambiguationData":[OSD([sQuery(id+"F20.wireOp",EDGE,"E87")])],"isStart":false});
            var Q6;
            Q6=makeQuery(id+"F21.opExtrude","CAP_EDGE",EDGE,{"disambiguationData":[OSD([sQuery(id+"F20.wireOp",EDGE,"E93")])],"isStart":true});
            var Q7;
            Q7=makeQuery(id+"F21.opExtrude","CAP_EDGE",EDGE,{"disambiguationData":[OSD([sQuery(id+"F20.wireOp",EDGE,"E87")])],"isStart":true});
            chamfer(context, id + "F22", {"entities" : qUnion([Q0, Q1, Q2, Q3, Q4, Q5, Q6, Q7]), "width" : 50.8 * mm, "tangentPropagation" : true});
        }
        {
            var Q0;
            Q0=makeQuery(id+"F15.opExtrude","SWEPT_EDGE",EDGE,{"disambiguationData":[OSD([sQuery(id+"F14.wireOp",EDGE,"E75"),sQuery(id+"F14.wireOp",EDGE,"E76")])]});
            var Q1;
            Q1=makeQuery(id+"F15.opExtrude","SWEPT_EDGE",EDGE,{"disambiguationData":[OSD([sQuery(id+"F14.wireOp",EDGE,"E77"),sQuery(id+"F14.wireOp",EDGE,"E78")])]});
            var Q2;
            Q2=makeQuery(id+"F15.opExtrude","SWEPT_EDGE",EDGE,{"disambiguationData":[OSD([sQuery(id+"F14.wireOp",EDGE,"E76"),sQuery(id+"F14.wireOp",EDGE,"E77")])]});
            var Q3;
            Q3=makeQuery(id+"F17.opExtrude","SWEPT_EDGE",EDGE,{"disambiguationData":[OSD([sQuery(id+"F16.wireOp",EDGE,"E81"),sQuery(id+"F16.wireOp",EDGE,"E82")])]});
            var Q4;
            Q4=makeQuery(id+"F17.opExtrude","SWEPT_EDGE",EDGE,{"disambiguationData":[OSD([sQuery(id+"F16.wireOp",EDGE,"E82"),sQuery(id+"F16.wireOp",EDGE,"E83")])]});
            var Q5;
            Q5=makeQuery(id+"F17.opExtrude","SWEPT_EDGE",EDGE,{"disambiguationData":[OSD([sQuery(id+"F16.wireOp",EDGE,"E83"),sQuery(id+"F16.wireOp",EDGE,"E84")])]});
            var Q6;
            Q6=makeQuery(id+"F21.opExtrude","SWEPT_EDGE",EDGE,{"disambiguationData":[OSD([sQuery(id+"F20.wireOp",EDGE,"E91"),sQuery(id+"F20.wireOp",EDGE,"E92")])]});
            var Q7;
            Q7=makeQuery(id+"F21.opExtrude","SWEPT_EDGE",EDGE,{"disambiguationData":[OSD([sQuery(id+"F20.wireOp",EDGE,"E92"),sQuery(id+"F20.wireOp",EDGE,"E93")])]});
            var Q8;
            Q8=makeQuery(id+"F21.opExtrude","SWEPT_EDGE",EDGE,{"disambiguationData":[OSD([sQuery(id+"F20.wireOp",EDGE,"E88"),sQuery(id+"F20.wireOp",EDGE,"E89")])]});
            var Q9;
            Q9=makeQuery(id+"F21.opExtrude","SWEPT_EDGE",EDGE,{"disambiguationData":[OSD([sQuery(id+"F20.wireOp",EDGE,"E87"),sQuery(id+"F20.wireOp",EDGE,"E88")])]});
            fillet(context, id + "F23", {"entities" : qUnion([Q0, Q1, Q2, Q3, Q4, Q5, Q6, Q7, Q8, Q9]), "radius" : 3.17 * mm, "tangentPropagation" : true, "allowEdgeOverflow" : false});
        }
        {
            var Q0;
            Q0=qCreatedBy(makeId("Right.planeOp"),FACE);
            var sketch = newSketch(context, id + "F24", { "sketchPlane" : qUnion([Q0])});
            skLineSegment(sketch, "E94.bottom", {"start": v(-124.13, -74.11) * mm, "end": v(-22.53, -74.11) * mm});
            skLineSegment(sketch, "E94.top", {"start": v(-124.13, -86.81) * mm, "end": v(-22.53, -86.81) * mm});
            skLineSegment(sketch, "E94.left", {"start": v(-124.13, -74.11) * mm, "end": v(-124.13, -86.81) * mm});
            skLineSegment(sketch, "E94.right", {"start": v(-22.53, -74.11) * mm, "end": v(-22.53, -86.81) * mm});
            skSolve(sketch);
        }
        {
            var Q0;
            Q0 = qSketchRegion(id + "F24", true);
            extrude(context, id + "F25", {"entities" : qUnion([Q0]), "depth" : 1517.65 * mm});
        }
        {
            var Q0;
            Q0=qCreatedBy(makeId("Right.planeOp"),FACE);
            var sketch = newSketch(context, id + "F26", { "sketchPlane" : qUnion([Q0])});
            skLineSegment(sketch, "E95.bottom", {"start": v(467.52, -7.43) * mm, "end": v(484.98, -7.43) * mm});
            skLineSegment(sketch, "E95.top", {"start": v(467.52, -128.58) * mm, "end": v(484.98, -128.58) * mm});
            skLineSegment(sketch, "E95.left", {"start": v(467.52, -7.43) * mm, "end": v(467.52, -128.58) * mm});
            skLineSegment(sketch, "E95.right", {"start": v(484.98, -7.43) * mm, "end": v(484.98, -128.58) * mm});
            skSolve(sketch);
        }
        {
            var Q0;
            Q0 = qSketchRegion(id + "F26", true);
            extrude(context, id + "F27", {"entities" : qUnion([Q0]), "depth" : 755.65 * mm});
        }
        {
            var Q0;
            Q0=qCreatedBy(makeId("Right.planeOp"),FACE);
            var sketch = newSketch(context, id + "F28", { "sketchPlane" : qUnion([Q0])});
            skLineSegment(sketch, "E96.bottom", {"start": v(589.14, -127.51) * mm, "end": v(601.84, -127.51) * mm});
            skLineSegment(sketch, "E96.top", {"start": v(589.14, -172.47) * mm, "end": v(601.84, -172.47) * mm});
            skLineSegment(sketch, "E96.left", {"start": v(589.14, -127.51) * mm, "end": v(589.14, -172.47) * mm});
            skLineSegment(sketch, "E97", {"start": v(601.84, -133.86) * mm, "end": v(595.5, -133.86) * mm});
            skLineSegment(sketch, "E98", {"start": v(595.5, -133.86) * mm, "end": v(595.5, -166.12) * mm});
            skLineSegment(sketch, "E99", {"start": v(595.5, -166.12) * mm, "end": v(601.84, -166.12) * mm});
            skLineSegment(sketch, "E100", {"start": v(601.84, -133.86) * mm, "end": v(601.84, -127.51) * mm});
            skLineSegment(sketch, "E101", {"start": v(601.84, -166.12) * mm, "end": v(601.84, -172.47) * mm});
            skSolve(sketch);
        }
        {
            var Q0;
            Q0 = qSketchRegion(id + "F28", true);
            extrude(context, id + "F29", {"entities" : qUnion([Q0]), "depth" : 609.6 * mm});
        }
        {
            var Q0;
            Q0=qCreatedBy(makeId("Right.planeOp"),FACE);
            var sketch = newSketch(context, id + "F30", { "sketchPlane" : qUnion([Q0])});
            skLineSegment(sketch, "E102.bottom", {"start": v(610.16, -134.32) * mm, "end": v(616.5, -134.32) * mm});
            skLineSegment(sketch, "E102.top", {"start": v(610.16, -166.58) * mm, "end": v(616.5, -166.58) * mm});
            skLineSegment(sketch, "E102.left", {"start": v(610.16, -134.32) * mm, "end": v(610.16, -166.58) * mm});
            skLineSegment(sketch, "E102.right", {"start": v(616.5, -134.32) * mm, "end": v(616.5, -166.58) * mm});
            skSolve(sketch);
        }
        {
            var Q0;
            Q0 = qSketchRegion(id + "F30", true);
            extrude(context, id + "F31", {"entities" : qUnion([Q0]), "depth" : 609.6 * mm});
        }
        {
            var Q0;
            Q0=makeQuery(id+"F15.opExtrude","SWEPT_FACE",FACE,{"disambiguationData":[OSD([sQuery(id+"F14.wireOp",EDGE,"E76")])]});
            var sketch = newSketch(context, id + "F32", { "sketchPlane" : qUnion([Q0])});
            skCircle(sketch, "E103", {"center": v(44.45, 297.3) * mm, "radius": 7.94 * mm});
            skCircle(sketch, "E104.1.0.0", {"center": v(1022.35, 297.3) * mm, "radius": 7.94 * mm});
            skCircle(sketch, "E104.2.0.0", {"center": v(2000.25, 297.3) * mm, "radius": 7.94 * mm});
            skLineSegment(sketch, "E104.direction1", {"start": v(44.45, 297.3) * mm, "end": v(1022.35, 297.3) * mm, "construction": true});
            skSolve(sketch);
        }
        {
            var Q0;
            Q0=sQuery(id+"F32.wireOp",VERTEX,"E103.center");
            var Q1;
            Q1=sQuery(id+"F32.wireOp",VERTEX,"E104.1.0.0.center");
            var Q2;
            Q2=sQuery(id+"F32.wireOp",VERTEX,"E104.2.0.0.center");
            var Q3;
            Q3=makeQuery(id+"F15.opExtrude","SWEPT_BODY",BODY,{"disambiguationData":[OSD([sQuery(id+"F14.wireOp",EDGE,"E73"),sQuery(id+"F14.wireOp",EDGE,"E74"),sQuery(id+"F14.wireOp",EDGE,"E75"),sQuery(id+"F14.wireOp",EDGE,"E76"),sQuery(id+"F14.wireOp",EDGE,"E77"),sQuery(id+"F14.wireOp",EDGE,"E78")])]});
            hole(context, id + "F33", {"style" : HoleStyle.C_SINK, "endStyle" : HoleEndStyle.BLIND, "holeDiameter" : 9.52 * mm, "cSinkDiameter" : 12.7 * mm, "cSinkAngle" : 90 * degree, "holeDepth" : 38.1 * mm, "isTappedThrough" : true, "tappedDepth" : 12.7 * mm, "tapClearance" : 3, "locations" : qUnion([Q0, Q1, Q2]), "scope" : qUnion([Q3])});
        }
        {
            var Q0;
            Q0=makeQuery(id+"F17.opExtrude","SWEPT_FACE",FACE,{"disambiguationData":[OSD([sQuery(id+"F16.wireOp",EDGE,"E82")])]});
            var sketch = newSketch(context, id + "F34", { "sketchPlane" : qUnion([Q0])});
            skCircle(sketch, "E105", {"center": v(44.45, 132.3) * mm, "radius": 6.35 * mm});
            skCircle(sketch, "E106.1.0.0", {"center": v(717.55, 132.3) * mm, "radius": 6.35 * mm});
            skLineSegment(sketch, "E106.direction1", {"start": v(44.45, 132.3) * mm, "end": v(717.55, 132.3) * mm, "construction": true});
            skSolve(sketch);
        }
        {
            var Q0;
            Q0=sQuery(id+"F34.wireOp",VERTEX,"E106.1.0.0.center");
            var Q1;
            Q1=sQuery(id+"F34.wireOp",VERTEX,"E106.direction1.start");
            var Q2;
            Q2=makeQuery(id+"F17.opExtrude","SWEPT_BODY",BODY,{"disambiguationData":[OSD([sQuery(id+"F16.wireOp",EDGE,"E79"),sQuery(id+"F16.wireOp",EDGE,"E80"),sQuery(id+"F16.wireOp",EDGE,"E81"),sQuery(id+"F16.wireOp",EDGE,"E82"),sQuery(id+"F16.wireOp",EDGE,"E83"),sQuery(id+"F16.wireOp",EDGE,"E84")])]});
            hole(context, id + "F35", {"style" : HoleStyle.C_SINK, "endStyle" : HoleEndStyle.THROUGH, "holeDiameter" : 9.52 * mm, "cSinkDiameter" : 12.7 * mm, "cSinkAngle" : 90 * degree, "isTappedThrough" : true, "tappedDepth" : 12.7 * mm, "tapClearance" : 3, "locations" : qUnion([Q0, Q1]), "scope" : qUnion([Q2])});
        }
        {
            var Q0;
            Q0=qCreatedBy(makeId("Top.planeOp"),FACE);
            var sketch = newSketch(context, id + "F36", { "sketchPlane" : qUnion([Q0])});
            skLineSegment(sketch, "E107.bottom", {"start": v(378.44, -450.22) * mm, "end": v(1181.71, -450.22) * mm});
            skLineSegment(sketch, "E107.top", {"start": v(378.44, -1180.47) * mm, "end": v(1181.71, -1180.47) * mm});
            skLineSegment(sketch, "E107.left", {"start": v(378.44, -450.22) * mm, "end": v(378.44, -1180.47) * mm});
            skLineSegment(sketch, "E107.right", {"start": v(1181.71, -450.22) * mm, "end": v(1181.71, -1180.47) * mm});
            skSolve(sketch);
        }
        {
            var Q0;
            Q0 = qSketchRegion(id + "F36", true);
            extrude(context, id + "F37", {"entities" : qUnion([Q0]), "depth" : 6.35 * mm});
        }
        {
            var Q0;
            Q0=qCreatedBy(makeId("Top.planeOp"),FACE);
            var sketch = newSketch(context, id + "F38", { "sketchPlane" : qUnion([Q0])});
            skLineSegment(sketch, "E108.bottom", {"start": v(1912.44, -386.11) * mm, "end": v(3944.44, -386.11) * mm});
            skLineSegment(sketch, "E108.top", {"start": v(1912.44, -1910.11) * mm, "end": v(3944.44, -1910.11) * mm});
            skLineSegment(sketch, "E108.left", {"start": v(1912.44, -386.11) * mm, "end": v(1912.44, -1910.11) * mm});
            skLineSegment(sketch, "E108.right", {"start": v(3944.44, -386.11) * mm, "end": v(3944.44, -1910.11) * mm});
            skSolve(sketch);
        }
        {
            var Q0;
            Q0 = qSketchRegion(id + "F38", true);
            extrude(context, id + "F39", {"entities" : qUnion([Q0]), "depth" : 304.8 * mm});
        }
        {
            var Q0;
            Q0=makeQuery(id+"F39.opExtrude","CAP_EDGE",EDGE,{"disambiguationData":[OSD([sQuery(id+"F38.wireOp",EDGE,"E108.top")])],"isStart":false});
            var Q1;
            Q1=makeQuery(id+"F39.opExtrude","SWEPT_EDGE",EDGE,{"disambiguationData":[OSD([sQuery(id+"F38.wireOp",EDGE,"E108.top"),sQuery(id+"F38.wireOp",EDGE,"E108.right")])]});
            var Q2;
            Q2=makeQuery(id+"F39.opExtrude","CAP_EDGE",EDGE,{"disambiguationData":[OSD([sQuery(id+"F38.wireOp",EDGE,"E108.right")])],"isStart":false});
            var Q3;
            Q3=makeQuery(id+"F39.opExtrude","SWEPT_EDGE",EDGE,{"disambiguationData":[OSD([sQuery(id+"F38.wireOp",EDGE,"E108.bottom"),sQuery(id+"F38.wireOp",EDGE,"E108.right")])]});
            var Q4;
            Q4=makeQuery(id+"F39.opExtrude","CAP_EDGE",EDGE,{"disambiguationData":[OSD([sQuery(id+"F38.wireOp",EDGE,"E108.bottom")])],"isStart":false});
            var Q5;
            Q5=makeQuery(id+"F39.opExtrude","CAP_EDGE",EDGE,{"disambiguationData":[OSD([sQuery(id+"F38.wireOp",EDGE,"E108.left")])],"isStart":false});
            var Q6;
            Q6=makeQuery(id+"F39.opExtrude","SWEPT_EDGE",EDGE,{"disambiguationData":[OSD([sQuery(id+"F38.wireOp",EDGE,"E108.top"),sQuery(id+"F38.wireOp",EDGE,"E108.left")])]});
            var Q7;
            Q7=makeQuery(id+"F39.opExtrude","SWEPT_EDGE",EDGE,{"disambiguationData":[OSD([sQuery(id+"F38.wireOp",EDGE,"E108.bottom"),sQuery(id+"F38.wireOp",EDGE,"E108.left")])]});
            fillet(context, id + "F40", {"entities" : qUnion([Q0, Q1, Q2, Q3, Q4, Q5, Q6, Q7]), "radius" : 76.2 * mm, "tangentPropagation" : true, "allowEdgeOverflow" : false});
        }
        {
            var Q0;
            Q0=makeQuery(id+"F39.opExtrude","CAP_FACE",FACE,{"disambiguationData":[OSD([sQuery(id+"F38.wireOp",EDGE,"E108.bottom"),sQuery(id+"F38.wireOp",EDGE,"E108.top"),sQuery(id+"F38.wireOp",EDGE,"E108.left"),sQuery(id+"F38.wireOp",EDGE,"E108.right")])],"isStart":false});
            var sketch = newSketch(context, id + "F41", { "sketchPlane" : qUnion([Q0])});
            skCircle(sketch, "E109", {"center": v(2115.64, -1757.71) * mm, "radius": 12.7 * mm});
            skCircle(sketch, "E110.0.1.0", {"center": v(2115.64, -1554.51) * mm, "radius": 12.7 * mm});
            skCircle(sketch, "E110.0.2.0", {"center": v(2115.64, -1351.31) * mm, "radius": 12.7 * mm});
            skCircle(sketch, "E110.0.3.0", {"center": v(2115.64, -1148.11) * mm, "radius": 12.7 * mm});
            skCircle(sketch, "E110.0.4.0", {"center": v(2115.64, -944.91) * mm, "radius": 12.7 * mm});
            skCircle(sketch, "E110.0.5.0", {"center": v(2115.64, -741.71) * mm, "radius": 12.7 * mm});
            skCircle(sketch, "E110.0.6.0", {"center": v(2115.64, -538.51) * mm, "radius": 12.7 * mm});
            skCircle(sketch, "E110.1.0.0", {"center": v(2318.84, -1757.71) * mm, "radius": 12.7 * mm});
            skCircle(sketch, "E110.1.1.0", {"center": v(2318.84, -1554.51) * mm, "radius": 12.7 * mm});
            skCircle(sketch, "E110.1.2.0", {"center": v(2318.84, -1351.31) * mm, "radius": 12.7 * mm});
            skCircle(sketch, "E110.1.3.0", {"center": v(2318.84, -1148.11) * mm, "radius": 12.7 * mm});
            skCircle(sketch, "E110.1.4.0", {"center": v(2318.84, -944.91) * mm, "radius": 12.7 * mm});
            skCircle(sketch, "E110.1.5.0", {"center": v(2318.84, -741.71) * mm, "radius": 12.7 * mm});
            skCircle(sketch, "E110.1.6.0", {"center": v(2318.84, -538.51) * mm, "radius": 12.7 * mm});
            skCircle(sketch, "E110.2.0.0", {"center": v(2522.04, -1757.71) * mm, "radius": 12.7 * mm});
            skCircle(sketch, "E110.2.1.0", {"center": v(2522.04, -1554.51) * mm, "radius": 12.7 * mm});
            skCircle(sketch, "E110.2.2.0", {"center": v(2522.04, -1351.31) * mm, "radius": 12.7 * mm});
            skCircle(sketch, "E110.2.3.0", {"center": v(2522.04, -1148.11) * mm, "radius": 12.7 * mm});
            skCircle(sketch, "E110.2.4.0", {"center": v(2522.04, -944.91) * mm, "radius": 12.7 * mm});
            skCircle(sketch, "E110.2.5.0", {"center": v(2522.04, -741.71) * mm, "radius": 12.7 * mm});
            skCircle(sketch, "E110.2.6.0", {"center": v(2522.04, -538.51) * mm, "radius": 12.7 * mm});
            skCircle(sketch, "E110.3.0.0", {"center": v(2725.24, -1757.71) * mm, "radius": 12.7 * mm});
            skCircle(sketch, "E110.3.1.0", {"center": v(2725.24, -1554.51) * mm, "radius": 12.7 * mm});
            skCircle(sketch, "E110.3.2.0", {"center": v(2725.24, -1351.31) * mm, "radius": 12.7 * mm});
            skCircle(sketch, "E110.3.3.0", {"center": v(2725.24, -1148.11) * mm, "radius": 12.7 * mm});
            skCircle(sketch, "E110.3.4.0", {"center": v(2725.24, -944.91) * mm, "radius": 12.7 * mm});
            skCircle(sketch, "E110.3.5.0", {"center": v(2725.24, -741.71) * mm, "radius": 12.7 * mm});
            skCircle(sketch, "E110.3.6.0", {"center": v(2725.24, -538.51) * mm, "radius": 12.7 * mm});
            skCircle(sketch, "E110.4.0.0", {"center": v(2928.44, -1757.71) * mm, "radius": 12.7 * mm});
            skCircle(sketch, "E110.4.1.0", {"center": v(2928.44, -1554.51) * mm, "radius": 12.7 * mm});
            skCircle(sketch, "E110.4.2.0", {"center": v(2928.44, -1351.31) * mm, "radius": 12.7 * mm});
            skCircle(sketch, "E110.4.3.0", {"center": v(2928.44, -1148.11) * mm, "radius": 12.7 * mm});
            skCircle(sketch, "E110.4.4.0", {"center": v(2928.44, -944.91) * mm, "radius": 12.7 * mm});
            skCircle(sketch, "E110.4.5.0", {"center": v(2928.44, -741.71) * mm, "radius": 12.7 * mm});
            skCircle(sketch, "E110.4.6.0", {"center": v(2928.44, -538.51) * mm, "radius": 12.7 * mm});
            skCircle(sketch, "E110.5.0.0", {"center": v(3131.64, -1757.71) * mm, "radius": 12.7 * mm});
            skCircle(sketch, "E110.5.1.0", {"center": v(3131.64, -1554.51) * mm, "radius": 12.7 * mm});
            skCircle(sketch, "E110.5.2.0", {"center": v(3131.64, -1351.31) * mm, "radius": 12.7 * mm});
            skCircle(sketch, "E110.5.3.0", {"center": v(3131.64, -1148.11) * mm, "radius": 12.7 * mm});
            skCircle(sketch, "E110.5.4.0", {"center": v(3131.64, -944.91) * mm, "radius": 12.7 * mm});
            skCircle(sketch, "E110.5.5.0", {"center": v(3131.64, -741.71) * mm, "radius": 12.7 * mm});
            skCircle(sketch, "E110.5.6.0", {"center": v(3131.64, -538.51) * mm, "radius": 12.7 * mm});
            skCircle(sketch, "E110.6.0.0", {"center": v(3334.84, -1757.71) * mm, "radius": 12.7 * mm});
            skCircle(sketch, "E110.6.1.0", {"center": v(3334.84, -1554.51) * mm, "radius": 12.7 * mm});
            skCircle(sketch, "E110.6.2.0", {"center": v(3334.84, -1351.31) * mm, "radius": 12.7 * mm});
            skCircle(sketch, "E110.6.3.0", {"center": v(3334.84, -1148.11) * mm, "radius": 12.7 * mm});
            skCircle(sketch, "E110.6.4.0", {"center": v(3334.84, -944.91) * mm, "radius": 12.7 * mm});
            skCircle(sketch, "E110.6.5.0", {"center": v(3334.84, -741.71) * mm, "radius": 12.7 * mm});
            skCircle(sketch, "E110.6.6.0", {"center": v(3334.84, -538.51) * mm, "radius": 12.7 * mm});
            skCircle(sketch, "E110.7.0.0", {"center": v(3538.04, -1757.71) * mm, "radius": 12.7 * mm});
            skCircle(sketch, "E110.7.1.0", {"center": v(3538.04, -1554.51) * mm, "radius": 12.7 * mm});
            skCircle(sketch, "E110.7.2.0", {"center": v(3538.04, -1351.31) * mm, "radius": 12.7 * mm});
            skCircle(sketch, "E110.7.3.0", {"center": v(3538.04, -1148.11) * mm, "radius": 12.7 * mm});
            skCircle(sketch, "E110.7.4.0", {"center": v(3538.04, -944.91) * mm, "radius": 12.7 * mm});
            skCircle(sketch, "E110.7.5.0", {"center": v(3538.04, -741.71) * mm, "radius": 12.7 * mm});
            skCircle(sketch, "E110.7.6.0", {"center": v(3538.04, -538.51) * mm, "radius": 12.7 * mm});
            skCircle(sketch, "E110.8.0.0", {"center": v(3741.24, -1757.71) * mm, "radius": 12.7 * mm});
            skCircle(sketch, "E110.8.1.0", {"center": v(3741.24, -1554.51) * mm, "radius": 12.7 * mm});
            skCircle(sketch, "E110.8.2.0", {"center": v(3741.24, -1351.31) * mm, "radius": 12.7 * mm});
            skCircle(sketch, "E110.8.3.0", {"center": v(3741.24, -1148.11) * mm, "radius": 12.7 * mm});
            skCircle(sketch, "E110.8.4.0", {"center": v(3741.24, -944.91) * mm, "radius": 12.7 * mm});
            skCircle(sketch, "E110.8.5.0", {"center": v(3741.24, -741.71) * mm, "radius": 12.7 * mm});
            skCircle(sketch, "E110.8.6.0", {"center": v(3741.24, -538.51) * mm, "radius": 12.7 * mm});
            skLineSegment(sketch, "E110.direction1", {"start": v(2115.64, -1706.91) * mm, "end": v(2318.84, -1706.91) * mm, "construction": true});
            skLineSegment(sketch, "E110.direction2", {"start": v(2115.64, -1706.91) * mm, "end": v(2115.64, -1503.71) * mm, "construction": true});
            skSolve(sketch);
        }
        {
            var Q0;
            Q0=makeQuery(id+"F41.imprint","IMPRINT",FACE,{"disambiguationData":[TD([[makeQuery(id+"F41.imprint","IMPRINT",EDGE,{"derivedFrom":sQuery(id+"F41.wireOp",EDGE,"E109")}),1.0]])]});
            var Q1;
            Q1=makeQuery(id+"F41.imprint","IMPRINT",FACE,{"disambiguationData":[TD([[makeQuery(id+"F41.imprint","IMPRINT",EDGE,{"derivedFrom":sQuery(id+"F41.wireOp",EDGE,"E110.1.0.0")}),1.0]])]});
            var Q2;
            Q2=makeQuery(id+"F41.imprint","IMPRINT",FACE,{"disambiguationData":[TD([[makeQuery(id+"F41.imprint","IMPRINT",EDGE,{"derivedFrom":sQuery(id+"F41.wireOp",EDGE,"E110.5.3.0")}),1.0]])]});
            var Q3;
            Q3=makeQuery(id+"F41.imprint","IMPRINT",FACE,{"disambiguationData":[TD([[makeQuery(id+"F41.imprint","IMPRINT",EDGE,{"derivedFrom":sQuery(id+"F41.wireOp",EDGE,"E110.7.5.0")}),1.0]])]});
            var Q4;
            Q4=makeQuery(id+"F41.imprint","IMPRINT",FACE,{"disambiguationData":[TD([[makeQuery(id+"F41.imprint","IMPRINT",EDGE,{"derivedFrom":sQuery(id+"F41.wireOp",EDGE,"E110.7.6.0")}),1.0]])]});
            var Q5;
            Q5=makeQuery(id+"F41.imprint","IMPRINT",FACE,{"disambiguationData":[TD([[makeQuery(id+"F41.imprint","IMPRINT",EDGE,{"derivedFrom":sQuery(id+"F41.wireOp",EDGE,"E110.6.6.0")}),1.0]])]});
            var Q6;
            Q6=makeQuery(id+"F41.imprint","IMPRINT",FACE,{"disambiguationData":[TD([[makeQuery(id+"F41.imprint","IMPRINT",EDGE,{"derivedFrom":sQuery(id+"F41.wireOp",EDGE,"E110.7.4.0")}),1.0]])]});
            var Q7;
            Q7=makeQuery(id+"F41.imprint","IMPRINT",FACE,{"disambiguationData":[TD([[makeQuery(id+"F41.imprint","IMPRINT",EDGE,{"derivedFrom":sQuery(id+"F41.wireOp",EDGE,"E110.0.3.0")}),1.0]])]});
            var Q8;
            Q8=makeQuery(id+"F41.imprint","IMPRINT",FACE,{"disambiguationData":[TD([[makeQuery(id+"F41.imprint","IMPRINT",EDGE,{"derivedFrom":sQuery(id+"F41.wireOp",EDGE,"E110.1.6.0")}),1.0]])]});
            var Q9;
            Q9=makeQuery(id+"F41.imprint","IMPRINT",FACE,{"disambiguationData":[TD([[makeQuery(id+"F41.imprint","IMPRINT",EDGE,{"derivedFrom":sQuery(id+"F41.wireOp",EDGE,"E110.0.6.0")}),1.0]])]});
            var Q10;
            Q10=makeQuery(id+"F41.imprint","IMPRINT",FACE,{"disambiguationData":[TD([[makeQuery(id+"F41.imprint","IMPRINT",EDGE,{"derivedFrom":sQuery(id+"F41.wireOp",EDGE,"E110.0.4.0")}),1.0]])]});
            var Q11;
            Q11=makeQuery(id+"F41.imprint","IMPRINT",FACE,{"disambiguationData":[TD([[makeQuery(id+"F41.imprint","IMPRINT",EDGE,{"derivedFrom":sQuery(id+"F41.wireOp",EDGE,"E110.0.5.0")}),1.0]])]});
            var Q12;
            Q12=makeQuery(id+"F41.imprint","IMPRINT",FACE,{"disambiguationData":[TD([[makeQuery(id+"F41.imprint","IMPRINT",EDGE,{"derivedFrom":sQuery(id+"F41.wireOp",EDGE,"E110.2.6.0")}),1.0]])]});
            var Q13;
            Q13=makeQuery(id+"F41.imprint","IMPRINT",FACE,{"disambiguationData":[TD([[makeQuery(id+"F41.imprint","IMPRINT",EDGE,{"derivedFrom":sQuery(id+"F41.wireOp",EDGE,"E110.7.3.0")}),1.0]])]});
            var Q14;
            Q14=makeQuery(id+"F41.imprint","IMPRINT",FACE,{"disambiguationData":[TD([[makeQuery(id+"F41.imprint","IMPRINT",EDGE,{"derivedFrom":sQuery(id+"F41.wireOp",EDGE,"E110.3.6.0")}),1.0]])]});
            var Q15;
            Q15=makeQuery(id+"F41.imprint","IMPRINT",FACE,{"disambiguationData":[TD([[makeQuery(id+"F41.imprint","IMPRINT",EDGE,{"derivedFrom":sQuery(id+"F41.wireOp",EDGE,"E110.3.3.0")}),1.0]])]});
            var Q16;
            Q16=makeQuery(id+"F41.imprint","IMPRINT",FACE,{"disambiguationData":[TD([[makeQuery(id+"F41.imprint","IMPRINT",EDGE,{"derivedFrom":sQuery(id+"F41.wireOp",EDGE,"E110.2.3.0")}),1.0]])]});
            var Q17;
            Q17=makeQuery(id+"F41.imprint","IMPRINT",FACE,{"disambiguationData":[TD([[makeQuery(id+"F41.imprint","IMPRINT",EDGE,{"derivedFrom":sQuery(id+"F41.wireOp",EDGE,"E110.5.6.0")}),1.0]])]});
            var Q18;
            Q18=makeQuery(id+"F41.imprint","IMPRINT",FACE,{"disambiguationData":[TD([[makeQuery(id+"F41.imprint","IMPRINT",EDGE,{"derivedFrom":sQuery(id+"F41.wireOp",EDGE,"E110.4.3.0")}),1.0]])]});
            var Q19;
            Q19=makeQuery(id+"F41.imprint","IMPRINT",FACE,{"disambiguationData":[TD([[makeQuery(id+"F41.imprint","IMPRINT",EDGE,{"derivedFrom":sQuery(id+"F41.wireOp",EDGE,"E110.4.6.0")}),1.0]])]});
            var Q20;
            Q20=makeQuery(id+"F41.imprint","IMPRINT",FACE,{"disambiguationData":[TD([[makeQuery(id+"F41.imprint","IMPRINT",EDGE,{"derivedFrom":sQuery(id+"F41.wireOp",EDGE,"E110.5.4.0")}),1.0]])]});
            var Q21;
            Q21=makeQuery(id+"F41.imprint","IMPRINT",FACE,{"disambiguationData":[TD([[makeQuery(id+"F41.imprint","IMPRINT",EDGE,{"derivedFrom":sQuery(id+"F41.wireOp",EDGE,"E110.4.4.0")}),1.0]])]});
            var Q22;
            Q22=makeQuery(id+"F41.imprint","IMPRINT",FACE,{"disambiguationData":[TD([[makeQuery(id+"F41.imprint","IMPRINT",EDGE,{"derivedFrom":sQuery(id+"F41.wireOp",EDGE,"E110.1.5.0")}),1.0]])]});
            var Q23;
            Q23=makeQuery(id+"F41.imprint","IMPRINT",FACE,{"disambiguationData":[TD([[makeQuery(id+"F41.imprint","IMPRINT",EDGE,{"derivedFrom":sQuery(id+"F41.wireOp",EDGE,"E110.1.3.0")}),1.0]])]});
            var Q24;
            Q24=makeQuery(id+"F41.imprint","IMPRINT",FACE,{"disambiguationData":[TD([[makeQuery(id+"F41.imprint","IMPRINT",EDGE,{"derivedFrom":sQuery(id+"F41.wireOp",EDGE,"E110.1.4.0")}),1.0]])]});
            var Q25;
            Q25=makeQuery(id+"F41.imprint","IMPRINT",FACE,{"disambiguationData":[TD([[makeQuery(id+"F41.imprint","IMPRINT",EDGE,{"derivedFrom":sQuery(id+"F41.wireOp",EDGE,"E110.6.4.0")}),1.0]])]});
            var Q26;
            Q26=makeQuery(id+"F41.imprint","IMPRINT",FACE,{"disambiguationData":[TD([[makeQuery(id+"F41.imprint","IMPRINT",EDGE,{"derivedFrom":sQuery(id+"F41.wireOp",EDGE,"E110.3.5.0")}),1.0]])]});
            var Q27;
            Q27=makeQuery(id+"F41.imprint","IMPRINT",FACE,{"disambiguationData":[TD([[makeQuery(id+"F41.imprint","IMPRINT",EDGE,{"derivedFrom":sQuery(id+"F41.wireOp",EDGE,"E110.2.5.0")}),1.0]])]});
            var Q28;
            Q28=makeQuery(id+"F41.imprint","IMPRINT",FACE,{"disambiguationData":[TD([[makeQuery(id+"F41.imprint","IMPRINT",EDGE,{"derivedFrom":sQuery(id+"F41.wireOp",EDGE,"E110.6.3.0")}),1.0]])]});
            var Q29;
            Q29=makeQuery(id+"F41.imprint","IMPRINT",FACE,{"disambiguationData":[TD([[makeQuery(id+"F41.imprint","IMPRINT",EDGE,{"derivedFrom":sQuery(id+"F41.wireOp",EDGE,"E110.5.5.0")}),1.0]])]});
            var Q30;
            Q30=makeQuery(id+"F41.imprint","IMPRINT",FACE,{"disambiguationData":[TD([[makeQuery(id+"F41.imprint","IMPRINT",EDGE,{"derivedFrom":sQuery(id+"F41.wireOp",EDGE,"E110.4.5.0")}),1.0]])]});
            var Q31;
            Q31=makeQuery(id+"F41.imprint","IMPRINT",FACE,{"disambiguationData":[TD([[makeQuery(id+"F41.imprint","IMPRINT",EDGE,{"derivedFrom":sQuery(id+"F41.wireOp",EDGE,"E110.3.4.0")}),1.0]])]});
            var Q32;
            Q32=makeQuery(id+"F41.imprint","IMPRINT",FACE,{"disambiguationData":[TD([[makeQuery(id+"F41.imprint","IMPRINT",EDGE,{"derivedFrom":sQuery(id+"F41.wireOp",EDGE,"E110.6.5.0")}),1.0]])]});
            var Q33;
            Q33=makeQuery(id+"F41.imprint","IMPRINT",FACE,{"disambiguationData":[TD([[makeQuery(id+"F41.imprint","IMPRINT",EDGE,{"derivedFrom":sQuery(id+"F41.wireOp",EDGE,"E110.2.4.0")}),1.0]])]});
            var Q34;
            Q34=makeQuery(id+"F41.imprint","IMPRINT",FACE,{"disambiguationData":[TD([[makeQuery(id+"F41.imprint","IMPRINT",EDGE,{"derivedFrom":sQuery(id+"F41.wireOp",EDGE,"E110.3.1.0")}),1.0]])]});
            var Q35;
            Q35=makeQuery(id+"F41.imprint","IMPRINT",FACE,{"disambiguationData":[TD([[makeQuery(id+"F41.imprint","IMPRINT",EDGE,{"derivedFrom":sQuery(id+"F41.wireOp",EDGE,"E110.3.2.0")}),1.0]])]});
            var Q36;
            Q36=makeQuery(id+"F41.imprint","IMPRINT",FACE,{"disambiguationData":[TD([[makeQuery(id+"F41.imprint","IMPRINT",EDGE,{"derivedFrom":sQuery(id+"F41.wireOp",EDGE,"E110.2.2.0")}),1.0]])]});
            var Q37;
            Q37=makeQuery(id+"F41.imprint","IMPRINT",FACE,{"disambiguationData":[TD([[makeQuery(id+"F41.imprint","IMPRINT",EDGE,{"derivedFrom":sQuery(id+"F41.wireOp",EDGE,"E110.3.0.0")}),1.0]])]});
            var Q38;
            Q38=makeQuery(id+"F41.imprint","IMPRINT",FACE,{"disambiguationData":[TD([[makeQuery(id+"F41.imprint","IMPRINT",EDGE,{"derivedFrom":sQuery(id+"F41.wireOp",EDGE,"E110.5.2.0")}),1.0]])]});
            var Q39;
            Q39=makeQuery(id+"F41.imprint","IMPRINT",FACE,{"disambiguationData":[TD([[makeQuery(id+"F41.imprint","IMPRINT",EDGE,{"derivedFrom":sQuery(id+"F41.wireOp",EDGE,"E110.4.2.0")}),1.0]])]});
            var Q40;
            Q40=makeQuery(id+"F41.imprint","IMPRINT",FACE,{"disambiguationData":[TD([[makeQuery(id+"F41.imprint","IMPRINT",EDGE,{"derivedFrom":sQuery(id+"F41.wireOp",EDGE,"E110.8.6.0")}),1.0]])]});
            var Q41;
            Q41=makeQuery(id+"F41.imprint","IMPRINT",FACE,{"disambiguationData":[TD([[makeQuery(id+"F41.imprint","IMPRINT",EDGE,{"derivedFrom":sQuery(id+"F41.wireOp",EDGE,"E110.4.0.0")}),1.0]])]});
            var Q42;
            Q42=makeQuery(id+"F41.imprint","IMPRINT",FACE,{"disambiguationData":[TD([[makeQuery(id+"F41.imprint","IMPRINT",EDGE,{"derivedFrom":sQuery(id+"F41.wireOp",EDGE,"E110.6.2.0")}),1.0]])]});
            var Q43;
            Q43=makeQuery(id+"F41.imprint","IMPRINT",FACE,{"disambiguationData":[TD([[makeQuery(id+"F41.imprint","IMPRINT",EDGE,{"derivedFrom":sQuery(id+"F41.wireOp",EDGE,"E110.8.4.0")}),1.0]])]});
            var Q44;
            Q44=makeQuery(id+"F41.imprint","IMPRINT",FACE,{"disambiguationData":[TD([[makeQuery(id+"F41.imprint","IMPRINT",EDGE,{"derivedFrom":sQuery(id+"F41.wireOp",EDGE,"E110.0.2.0")}),1.0]])]});
            var Q45;
            Q45=makeQuery(id+"F41.imprint","IMPRINT",FACE,{"disambiguationData":[TD([[makeQuery(id+"F41.imprint","IMPRINT",EDGE,{"derivedFrom":sQuery(id+"F41.wireOp",EDGE,"E110.0.1.0")}),1.0]])]});
            var Q46;
            Q46=makeQuery(id+"F41.imprint","IMPRINT",FACE,{"disambiguationData":[TD([[makeQuery(id+"F41.imprint","IMPRINT",EDGE,{"derivedFrom":sQuery(id+"F41.wireOp",EDGE,"E110.2.0.0")}),1.0]])]});
            var Q47;
            Q47=makeQuery(id+"F41.imprint","IMPRINT",FACE,{"disambiguationData":[TD([[makeQuery(id+"F41.imprint","IMPRINT",EDGE,{"derivedFrom":sQuery(id+"F41.wireOp",EDGE,"E110.1.1.0")}),1.0]])]});
            var Q48;
            Q48=makeQuery(id+"F41.imprint","IMPRINT",FACE,{"disambiguationData":[TD([[makeQuery(id+"F41.imprint","IMPRINT",EDGE,{"derivedFrom":sQuery(id+"F41.wireOp",EDGE,"E110.1.2.0")}),1.0]])]});
            var Q49;
            Q49=makeQuery(id+"F41.imprint","IMPRINT",FACE,{"disambiguationData":[TD([[makeQuery(id+"F41.imprint","IMPRINT",EDGE,{"derivedFrom":sQuery(id+"F41.wireOp",EDGE,"E110.2.1.0")}),1.0]])]});
            var Q50;
            Q50=makeQuery(id+"F41.imprint","IMPRINT",FACE,{"disambiguationData":[TD([[makeQuery(id+"F41.imprint","IMPRINT",EDGE,{"derivedFrom":sQuery(id+"F41.wireOp",EDGE,"E110.6.0.0")}),1.0]])]});
            var Q51;
            Q51=makeQuery(id+"F41.imprint","IMPRINT",FACE,{"disambiguationData":[TD([[makeQuery(id+"F41.imprint","IMPRINT",EDGE,{"derivedFrom":sQuery(id+"F41.wireOp",EDGE,"E110.8.2.0")}),1.0]])]});
            var Q52;
            Q52=makeQuery(id+"F41.imprint","IMPRINT",FACE,{"disambiguationData":[TD([[makeQuery(id+"F41.imprint","IMPRINT",EDGE,{"derivedFrom":sQuery(id+"F41.wireOp",EDGE,"E110.5.0.0")}),1.0]])]});
            var Q53;
            Q53=makeQuery(id+"F41.imprint","IMPRINT",FACE,{"disambiguationData":[TD([[makeQuery(id+"F41.imprint","IMPRINT",EDGE,{"derivedFrom":sQuery(id+"F41.wireOp",EDGE,"E110.7.2.0")}),1.0]])]});
            var Q54;
            Q54=makeQuery(id+"F41.imprint","IMPRINT",FACE,{"disambiguationData":[TD([[makeQuery(id+"F41.imprint","IMPRINT",EDGE,{"derivedFrom":sQuery(id+"F41.wireOp",EDGE,"E110.6.1.0")}),1.0]])]});
            var Q55;
            Q55=makeQuery(id+"F41.imprint","IMPRINT",FACE,{"disambiguationData":[TD([[makeQuery(id+"F41.imprint","IMPRINT",EDGE,{"derivedFrom":sQuery(id+"F41.wireOp",EDGE,"E110.8.3.0")}),1.0]])]});
            var Q56;
            Q56=makeQuery(id+"F41.imprint","IMPRINT",FACE,{"disambiguationData":[TD([[makeQuery(id+"F41.imprint","IMPRINT",EDGE,{"derivedFrom":sQuery(id+"F41.wireOp",EDGE,"E110.5.1.0")}),1.0]])]});
            var Q57;
            Q57=makeQuery(id+"F41.imprint","IMPRINT",FACE,{"disambiguationData":[TD([[makeQuery(id+"F41.imprint","IMPRINT",EDGE,{"derivedFrom":sQuery(id+"F41.wireOp",EDGE,"E110.4.1.0")}),1.0]])]});
            var Q58;
            Q58=makeQuery(id+"F41.imprint","IMPRINT",FACE,{"disambiguationData":[TD([[makeQuery(id+"F41.imprint","IMPRINT",EDGE,{"derivedFrom":sQuery(id+"F41.wireOp",EDGE,"E110.8.5.0")}),1.0]])]});
            var Q59;
            Q59=makeQuery(id+"F41.imprint","IMPRINT",FACE,{"disambiguationData":[TD([[makeQuery(id+"F41.imprint","IMPRINT",EDGE,{"derivedFrom":sQuery(id+"F41.wireOp",EDGE,"E110.8.0.0")}),1.0]])]});
            var Q60;
            Q60=makeQuery(id+"F41.imprint","IMPRINT",FACE,{"disambiguationData":[TD([[makeQuery(id+"F41.imprint","IMPRINT",EDGE,{"derivedFrom":sQuery(id+"F41.wireOp",EDGE,"E110.7.0.0")}),1.0]])]});
            var Q61;
            Q61=makeQuery(id+"F41.imprint","IMPRINT",FACE,{"disambiguationData":[TD([[makeQuery(id+"F41.imprint","IMPRINT",EDGE,{"derivedFrom":sQuery(id+"F41.wireOp",EDGE,"E110.8.1.0")}),1.0]])]});
            var Q62;
            Q62=makeQuery(id+"F41.imprint","IMPRINT",FACE,{"disambiguationData":[TD([[makeQuery(id+"F41.imprint","IMPRINT",EDGE,{"derivedFrom":sQuery(id+"F41.wireOp",EDGE,"E110.7.1.0")}),1.0]])]});
            extrude(context, id + "F42", {"entities" : qUnion([Q0, Q1, Q2, Q3, Q4, Q5, Q6, Q7, Q8, Q9, Q10, Q11, Q12, Q13, Q14, Q15, Q16, Q17, Q18, Q19, Q20, Q21, Q22, Q23, Q24, Q25, Q26, Q27, Q28, Q29, Q30, Q31, Q32, Q33, Q34, Q35, Q36, Q37, Q38, Q39, Q40, Q41, Q42, Q43, Q44, Q45, Q46, Q47, Q48, Q49, Q50, Q51, Q52, Q53, Q54, Q55, Q56, Q57, Q58, Q59, Q60, Q61, Q62]), "operationType" : NewBodyOperationType.REMOVE, "oppositeDirection" : true, "depth" : 19.05 * mm});
        }
        {
            var Q0;
            Q0=makeQuery(id+"F42.boolean.opBoolean","COPY",EDGE,{"derivedFrom":makeQuery(id+"F42.opExtrude","CAP_EDGE",EDGE,{"disambiguationData":[OSD([sQuery(id+"F41.wireOp",EDGE,"E110.0.2.0")])],"isStart":false})});
            var Q1;
            Q1=makeQuery(id+"F42.boolean.opBoolean","COPY",EDGE,{"derivedFrom":makeQuery(id+"F42.opExtrude","CAP_EDGE",EDGE,{"disambiguationData":[OSD([sQuery(id+"F41.wireOp",EDGE,"E110.0.1.0")])],"isStart":false})});
            var Q2;
            Q2=makeQuery(id+"F42.boolean.opBoolean","COPY",EDGE,{"derivedFrom":makeQuery(id+"F42.opExtrude","CAP_EDGE",EDGE,{"disambiguationData":[OSD([sQuery(id+"F41.wireOp",EDGE,"E109")])],"isStart":false})});
            var Q3;
            Q3=makeQuery(id+"F42.boolean.opBoolean","COPY",EDGE,{"derivedFrom":makeQuery(id+"F42.opExtrude","CAP_EDGE",EDGE,{"disambiguationData":[OSD([sQuery(id+"F41.wireOp",EDGE,"E110.0.3.0")])],"isStart":false})});
            var Q4;
            Q4=makeQuery(id+"F42.boolean.opBoolean","COPY",EDGE,{"derivedFrom":makeQuery(id+"F42.opExtrude","CAP_EDGE",EDGE,{"disambiguationData":[OSD([sQuery(id+"F41.wireOp",EDGE,"E110.0.4.0")])],"isStart":false})});
            var Q5;
            Q5=makeQuery(id+"F42.boolean.opBoolean","COPY",EDGE,{"derivedFrom":makeQuery(id+"F42.opExtrude","CAP_EDGE",EDGE,{"disambiguationData":[OSD([sQuery(id+"F41.wireOp",EDGE,"E110.0.5.0")])],"isStart":false})});
            var Q6;
            Q6=makeQuery(id+"F42.boolean.opBoolean","COPY",EDGE,{"derivedFrom":makeQuery(id+"F42.opExtrude","CAP_EDGE",EDGE,{"disambiguationData":[OSD([sQuery(id+"F41.wireOp",EDGE,"E110.0.6.0")])],"isStart":false})});
            var Q7;
            Q7=makeQuery(id+"F42.boolean.opBoolean","COPY",EDGE,{"derivedFrom":makeQuery(id+"F42.opExtrude","CAP_EDGE",EDGE,{"disambiguationData":[OSD([sQuery(id+"F41.wireOp",EDGE,"E110.1.6.0")])],"isStart":false})});
            var Q8;
            Q8=makeQuery(id+"F42.boolean.opBoolean","COPY",EDGE,{"derivedFrom":makeQuery(id+"F42.opExtrude","CAP_EDGE",EDGE,{"disambiguationData":[OSD([sQuery(id+"F41.wireOp",EDGE,"E110.1.5.0")])],"isStart":false})});
            var Q9;
            Q9=makeQuery(id+"F42.boolean.opBoolean","COPY",EDGE,{"derivedFrom":makeQuery(id+"F42.opExtrude","CAP_EDGE",EDGE,{"disambiguationData":[OSD([sQuery(id+"F41.wireOp",EDGE,"E110.1.4.0")])],"isStart":false})});
            var Q10;
            Q10=makeQuery(id+"F42.boolean.opBoolean","COPY",EDGE,{"derivedFrom":makeQuery(id+"F42.opExtrude","CAP_EDGE",EDGE,{"disambiguationData":[OSD([sQuery(id+"F41.wireOp",EDGE,"E110.1.3.0")])],"isStart":false})});
            var Q11;
            Q11=makeQuery(id+"F42.boolean.opBoolean","COPY",EDGE,{"derivedFrom":makeQuery(id+"F42.opExtrude","CAP_EDGE",EDGE,{"disambiguationData":[OSD([sQuery(id+"F41.wireOp",EDGE,"E110.2.4.0")])],"isStart":false})});
            var Q12;
            Q12=makeQuery(id+"F42.boolean.opBoolean","COPY",EDGE,{"derivedFrom":makeQuery(id+"F42.opExtrude","CAP_EDGE",EDGE,{"disambiguationData":[OSD([sQuery(id+"F41.wireOp",EDGE,"E110.2.5.0")])],"isStart":false})});
            var Q13;
            Q13=makeQuery(id+"F42.boolean.opBoolean","COPY",EDGE,{"derivedFrom":makeQuery(id+"F42.opExtrude","CAP_EDGE",EDGE,{"disambiguationData":[OSD([sQuery(id+"F41.wireOp",EDGE,"E110.1.2.0")])],"isStart":false})});
            var Q14;
            Q14=makeQuery(id+"F42.boolean.opBoolean","COPY",EDGE,{"derivedFrom":makeQuery(id+"F42.opExtrude","CAP_EDGE",EDGE,{"disambiguationData":[OSD([sQuery(id+"F41.wireOp",EDGE,"E110.1.1.0")])],"isStart":false})});
            var Q15;
            Q15=makeQuery(id+"F42.boolean.opBoolean","COPY",EDGE,{"derivedFrom":makeQuery(id+"F42.opExtrude","CAP_EDGE",EDGE,{"disambiguationData":[OSD([sQuery(id+"F41.wireOp",EDGE,"E110.1.0.0")])],"isStart":false})});
            var Q16;
            Q16=makeQuery(id+"F42.boolean.opBoolean","COPY",EDGE,{"derivedFrom":makeQuery(id+"F42.opExtrude","CAP_EDGE",EDGE,{"disambiguationData":[OSD([sQuery(id+"F41.wireOp",EDGE,"E110.2.0.0")])],"isStart":false})});
            var Q17;
            Q17=makeQuery(id+"F42.boolean.opBoolean","COPY",EDGE,{"derivedFrom":makeQuery(id+"F42.opExtrude","CAP_EDGE",EDGE,{"disambiguationData":[OSD([sQuery(id+"F41.wireOp",EDGE,"E110.2.1.0")])],"isStart":false})});
            var Q18;
            Q18=makeQuery(id+"F42.boolean.opBoolean","COPY",EDGE,{"derivedFrom":makeQuery(id+"F42.opExtrude","CAP_EDGE",EDGE,{"disambiguationData":[OSD([sQuery(id+"F41.wireOp",EDGE,"E110.2.2.0")])],"isStart":false})});
            var Q19;
            Q19=makeQuery(id+"F42.boolean.opBoolean","COPY",EDGE,{"derivedFrom":makeQuery(id+"F42.opExtrude","CAP_EDGE",EDGE,{"disambiguationData":[OSD([sQuery(id+"F41.wireOp",EDGE,"E110.2.3.0")])],"isStart":false})});
            var Q20;
            Q20=makeQuery(id+"F42.boolean.opBoolean","COPY",EDGE,{"derivedFrom":makeQuery(id+"F42.opExtrude","CAP_EDGE",EDGE,{"disambiguationData":[OSD([sQuery(id+"F41.wireOp",EDGE,"E110.2.6.0")])],"isStart":false})});
            var Q21;
            Q21=makeQuery(id+"F42.boolean.opBoolean","COPY",EDGE,{"derivedFrom":makeQuery(id+"F42.opExtrude","CAP_EDGE",EDGE,{"disambiguationData":[OSD([sQuery(id+"F41.wireOp",EDGE,"E110.3.6.0")])],"isStart":false})});
            var Q22;
            Q22=makeQuery(id+"F42.boolean.opBoolean","COPY",EDGE,{"derivedFrom":makeQuery(id+"F42.opExtrude","CAP_EDGE",EDGE,{"disambiguationData":[OSD([sQuery(id+"F41.wireOp",EDGE,"E110.3.5.0")])],"isStart":false})});
            var Q23;
            Q23=makeQuery(id+"F42.boolean.opBoolean","COPY",EDGE,{"derivedFrom":makeQuery(id+"F42.opExtrude","CAP_EDGE",EDGE,{"disambiguationData":[OSD([sQuery(id+"F41.wireOp",EDGE,"E110.3.4.0")])],"isStart":false})});
            var Q24;
            Q24=makeQuery(id+"F42.boolean.opBoolean","COPY",EDGE,{"derivedFrom":makeQuery(id+"F42.opExtrude","CAP_EDGE",EDGE,{"disambiguationData":[OSD([sQuery(id+"F41.wireOp",EDGE,"E110.4.6.0")])],"isStart":false})});
            var Q25;
            Q25=makeQuery(id+"F42.boolean.opBoolean","COPY",EDGE,{"derivedFrom":makeQuery(id+"F42.opExtrude","CAP_EDGE",EDGE,{"disambiguationData":[OSD([sQuery(id+"F41.wireOp",EDGE,"E110.4.5.0")])],"isStart":false})});
            var Q26;
            Q26=makeQuery(id+"F42.boolean.opBoolean","COPY",EDGE,{"derivedFrom":makeQuery(id+"F42.opExtrude","CAP_EDGE",EDGE,{"disambiguationData":[OSD([sQuery(id+"F41.wireOp",EDGE,"E110.4.4.0")])],"isStart":false})});
            var Q27;
            Q27=makeQuery(id+"F42.boolean.opBoolean","COPY",EDGE,{"derivedFrom":makeQuery(id+"F42.opExtrude","CAP_EDGE",EDGE,{"disambiguationData":[OSD([sQuery(id+"F41.wireOp",EDGE,"E110.3.3.0")])],"isStart":false})});
            var Q28;
            Q28=makeQuery(id+"F42.boolean.opBoolean","COPY",EDGE,{"derivedFrom":makeQuery(id+"F42.opExtrude","CAP_EDGE",EDGE,{"disambiguationData":[OSD([sQuery(id+"F41.wireOp",EDGE,"E110.3.2.0")])],"isStart":false})});
            var Q29;
            Q29=makeQuery(id+"F42.boolean.opBoolean","COPY",EDGE,{"derivedFrom":makeQuery(id+"F42.opExtrude","CAP_EDGE",EDGE,{"disambiguationData":[OSD([sQuery(id+"F41.wireOp",EDGE,"E110.3.1.0")])],"isStart":false})});
            var Q30;
            Q30=makeQuery(id+"F42.boolean.opBoolean","COPY",EDGE,{"derivedFrom":makeQuery(id+"F42.opExtrude","CAP_EDGE",EDGE,{"disambiguationData":[OSD([sQuery(id+"F41.wireOp",EDGE,"E110.3.0.0")])],"isStart":false})});
            var Q31;
            Q31=makeQuery(id+"F42.boolean.opBoolean","COPY",EDGE,{"derivedFrom":makeQuery(id+"F42.opExtrude","CAP_EDGE",EDGE,{"disambiguationData":[OSD([sQuery(id+"F41.wireOp",EDGE,"E110.4.0.0")])],"isStart":false})});
            var Q32;
            Q32=makeQuery(id+"F42.boolean.opBoolean","COPY",EDGE,{"derivedFrom":makeQuery(id+"F42.opExtrude","CAP_EDGE",EDGE,{"disambiguationData":[OSD([sQuery(id+"F41.wireOp",EDGE,"E110.4.1.0")])],"isStart":false})});
            var Q33;
            Q33=makeQuery(id+"F42.boolean.opBoolean","COPY",EDGE,{"derivedFrom":makeQuery(id+"F42.opExtrude","CAP_EDGE",EDGE,{"disambiguationData":[OSD([sQuery(id+"F41.wireOp",EDGE,"E110.4.2.0")])],"isStart":false})});
            var Q34;
            Q34=makeQuery(id+"F42.boolean.opBoolean","COPY",EDGE,{"derivedFrom":makeQuery(id+"F42.opExtrude","CAP_EDGE",EDGE,{"disambiguationData":[OSD([sQuery(id+"F41.wireOp",EDGE,"E110.4.3.0")])],"isStart":false})});
            var Q35;
            Q35=makeQuery(id+"F42.boolean.opBoolean","COPY",EDGE,{"derivedFrom":makeQuery(id+"F42.opExtrude","CAP_EDGE",EDGE,{"disambiguationData":[OSD([sQuery(id+"F41.wireOp",EDGE,"E110.5.0.0")])],"isStart":false})});
            var Q36;
            Q36=makeQuery(id+"F42.boolean.opBoolean","COPY",EDGE,{"derivedFrom":makeQuery(id+"F42.opExtrude","CAP_EDGE",EDGE,{"disambiguationData":[OSD([sQuery(id+"F41.wireOp",EDGE,"E110.5.1.0")])],"isStart":false})});
            var Q37;
            Q37=makeQuery(id+"F42.boolean.opBoolean","COPY",EDGE,{"derivedFrom":makeQuery(id+"F42.opExtrude","CAP_EDGE",EDGE,{"disambiguationData":[OSD([sQuery(id+"F41.wireOp",EDGE,"E110.5.2.0")])],"isStart":false})});
            var Q38;
            Q38=makeQuery(id+"F42.boolean.opBoolean","COPY",EDGE,{"derivedFrom":makeQuery(id+"F42.opExtrude","CAP_EDGE",EDGE,{"disambiguationData":[OSD([sQuery(id+"F41.wireOp",EDGE,"E110.5.3.0")])],"isStart":false})});
            var Q39;
            Q39=makeQuery(id+"F42.boolean.opBoolean","COPY",EDGE,{"derivedFrom":makeQuery(id+"F42.opExtrude","CAP_EDGE",EDGE,{"disambiguationData":[OSD([sQuery(id+"F41.wireOp",EDGE,"E110.5.4.0")])],"isStart":false})});
            var Q40;
            Q40=makeQuery(id+"F42.boolean.opBoolean","COPY",EDGE,{"derivedFrom":makeQuery(id+"F42.opExtrude","CAP_EDGE",EDGE,{"disambiguationData":[OSD([sQuery(id+"F41.wireOp",EDGE,"E110.5.5.0")])],"isStart":false})});
            var Q41;
            Q41=makeQuery(id+"F42.boolean.opBoolean","COPY",EDGE,{"derivedFrom":makeQuery(id+"F42.opExtrude","CAP_EDGE",EDGE,{"disambiguationData":[OSD([sQuery(id+"F41.wireOp",EDGE,"E110.6.1.0")])],"isStart":false})});
            var Q42;
            Q42=makeQuery(id+"F42.boolean.opBoolean","COPY",EDGE,{"derivedFrom":makeQuery(id+"F42.opExtrude","CAP_EDGE",EDGE,{"disambiguationData":[OSD([sQuery(id+"F41.wireOp",EDGE,"E110.6.2.0")])],"isStart":false})});
            var Q43;
            Q43=makeQuery(id+"F42.boolean.opBoolean","COPY",EDGE,{"derivedFrom":makeQuery(id+"F42.opExtrude","CAP_EDGE",EDGE,{"disambiguationData":[OSD([sQuery(id+"F41.wireOp",EDGE,"E110.6.3.0")])],"isStart":false})});
            var Q44;
            Q44=makeQuery(id+"F42.boolean.opBoolean","COPY",EDGE,{"derivedFrom":makeQuery(id+"F42.opExtrude","CAP_EDGE",EDGE,{"disambiguationData":[OSD([sQuery(id+"F41.wireOp",EDGE,"E110.6.4.0")])],"isStart":false})});
            var Q45;
            Q45=makeQuery(id+"F42.boolean.opBoolean","COPY",EDGE,{"derivedFrom":makeQuery(id+"F42.opExtrude","CAP_EDGE",EDGE,{"disambiguationData":[OSD([sQuery(id+"F41.wireOp",EDGE,"E110.7.1.0")])],"isStart":false})});
            var Q46;
            Q46=makeQuery(id+"F42.boolean.opBoolean","COPY",EDGE,{"derivedFrom":makeQuery(id+"F42.opExtrude","CAP_EDGE",EDGE,{"disambiguationData":[OSD([sQuery(id+"F41.wireOp",EDGE,"E110.7.2.0")])],"isStart":false})});
            var Q47;
            Q47=makeQuery(id+"F42.boolean.opBoolean","COPY",EDGE,{"derivedFrom":makeQuery(id+"F42.opExtrude","CAP_EDGE",EDGE,{"disambiguationData":[OSD([sQuery(id+"F41.wireOp",EDGE,"E110.7.3.0")])],"isStart":false})});
            var Q48;
            Q48=makeQuery(id+"F42.boolean.opBoolean","COPY",EDGE,{"derivedFrom":makeQuery(id+"F42.opExtrude","CAP_EDGE",EDGE,{"disambiguationData":[OSD([sQuery(id+"F41.wireOp",EDGE,"E110.8.2.0")])],"isStart":false})});
            var Q49;
            Q49=makeQuery(id+"F42.boolean.opBoolean","COPY",EDGE,{"derivedFrom":makeQuery(id+"F42.opExtrude","CAP_EDGE",EDGE,{"disambiguationData":[OSD([sQuery(id+"F41.wireOp",EDGE,"E110.8.3.0")])],"isStart":false})});
            var Q50;
            Q50=makeQuery(id+"F42.boolean.opBoolean","COPY",EDGE,{"derivedFrom":makeQuery(id+"F42.opExtrude","CAP_EDGE",EDGE,{"disambiguationData":[OSD([sQuery(id+"F41.wireOp",EDGE,"E110.7.4.0")])],"isStart":false})});
            var Q51;
            Q51=makeQuery(id+"F42.boolean.opBoolean","COPY",EDGE,{"derivedFrom":makeQuery(id+"F42.opExtrude","CAP_EDGE",EDGE,{"disambiguationData":[OSD([sQuery(id+"F41.wireOp",EDGE,"E110.7.5.0")])],"isStart":false})});
            var Q52;
            Q52=makeQuery(id+"F42.boolean.opBoolean","COPY",EDGE,{"derivedFrom":makeQuery(id+"F42.opExtrude","CAP_EDGE",EDGE,{"disambiguationData":[OSD([sQuery(id+"F41.wireOp",EDGE,"E110.5.6.0")])],"isStart":false})});
            var Q53;
            Q53=makeQuery(id+"F42.boolean.opBoolean","COPY",EDGE,{"derivedFrom":makeQuery(id+"F42.opExtrude","CAP_EDGE",EDGE,{"disambiguationData":[OSD([sQuery(id+"F41.wireOp",EDGE,"E110.6.5.0")])],"isStart":false})});
            var Q54;
            Q54=makeQuery(id+"F42.boolean.opBoolean","COPY",EDGE,{"derivedFrom":makeQuery(id+"F42.opExtrude","CAP_EDGE",EDGE,{"disambiguationData":[OSD([sQuery(id+"F41.wireOp",EDGE,"E110.6.6.0")])],"isStart":false})});
            var Q55;
            Q55=makeQuery(id+"F42.boolean.opBoolean","COPY",EDGE,{"derivedFrom":makeQuery(id+"F42.opExtrude","CAP_EDGE",EDGE,{"disambiguationData":[OSD([sQuery(id+"F41.wireOp",EDGE,"E110.7.6.0")])],"isStart":false})});
            var Q56;
            Q56=makeQuery(id+"F42.boolean.opBoolean","COPY",EDGE,{"derivedFrom":makeQuery(id+"F42.opExtrude","CAP_EDGE",EDGE,{"disambiguationData":[OSD([sQuery(id+"F41.wireOp",EDGE,"E110.8.6.0")])],"isStart":false})});
            var Q57;
            Q57=makeQuery(id+"F42.boolean.opBoolean","COPY",EDGE,{"derivedFrom":makeQuery(id+"F42.opExtrude","CAP_EDGE",EDGE,{"disambiguationData":[OSD([sQuery(id+"F41.wireOp",EDGE,"E110.8.5.0")])],"isStart":false})});
            var Q58;
            Q58=makeQuery(id+"F42.boolean.opBoolean","COPY",EDGE,{"derivedFrom":makeQuery(id+"F42.opExtrude","CAP_EDGE",EDGE,{"disambiguationData":[OSD([sQuery(id+"F41.wireOp",EDGE,"E110.8.4.0")])],"isStart":false})});
            var Q59;
            Q59=makeQuery(id+"F42.boolean.opBoolean","COPY",EDGE,{"derivedFrom":makeQuery(id+"F42.opExtrude","CAP_EDGE",EDGE,{"disambiguationData":[OSD([sQuery(id+"F41.wireOp",EDGE,"E110.6.0.0")])],"isStart":false})});
            var Q60;
            Q60=makeQuery(id+"F42.boolean.opBoolean","COPY",EDGE,{"derivedFrom":makeQuery(id+"F42.opExtrude","CAP_EDGE",EDGE,{"disambiguationData":[OSD([sQuery(id+"F41.wireOp",EDGE,"E110.7.0.0")])],"isStart":false})});
            var Q61;
            Q61=makeQuery(id+"F42.boolean.opBoolean","COPY",EDGE,{"derivedFrom":makeQuery(id+"F42.opExtrude","CAP_EDGE",EDGE,{"disambiguationData":[OSD([sQuery(id+"F41.wireOp",EDGE,"E110.8.0.0")])],"isStart":false})});
            var Q62;
            Q62=makeQuery(id+"F42.boolean.opBoolean","COPY",EDGE,{"derivedFrom":makeQuery(id+"F42.opExtrude","CAP_EDGE",EDGE,{"disambiguationData":[OSD([sQuery(id+"F41.wireOp",EDGE,"E110.8.1.0")])],"isStart":false})});
            chamfer(context, id + "F43", {"entities" : qUnion([Q0, Q1, Q2, Q3, Q4, Q5, Q6, Q7, Q8, Q9, Q10, Q11, Q12, Q13, Q14, Q15, Q16, Q17, Q18, Q19, Q20, Q21, Q22, Q23, Q24, Q25, Q26, Q27, Q28, Q29, Q30, Q31, Q32, Q33, Q34, Q35, Q36, Q37, Q38, Q39, Q40, Q41, Q42, Q43, Q44, Q45, Q46, Q47, Q48, Q49, Q50, Q51, Q52, Q53, Q54, Q55, Q56, Q57, Q58, Q59, Q60, Q61, Q62]), "chamferType" : ChamferType.TWO_OFFSETS, "width1" : 12.7 * mm, "oppositeDirection" : false, "width2" : 19.05 * mm});
        }
        {
            var Q0;
            Q0=makeQuery(id+"F43.opChamfer","BLEND_EDGE",EDGE,{"blendedFrom":[makeQuery(id+"F42.boolean.opBoolean","COPY",EDGE,{"derivedFrom":makeQuery(id+"F42.opExtrude","CAP_EDGE",EDGE,{"disambiguationData":[OSD([sQuery(id+"F41.wireOp",EDGE,"E110.8.0.0")])],"isStart":false})}),makeQuery(id+"F39.opExtrude","CAP_FACE",FACE,{"disambiguationData":[OSD([sQuery(id+"F38.wireOp",EDGE,"E108.bottom"),sQuery(id+"F38.wireOp",EDGE,"E108.top"),sQuery(id+"F38.wireOp",EDGE,"E108.left"),sQuery(id+"F38.wireOp",EDGE,"E108.right")])],"isStart":false})],"blendedInto":[makeQuery(id+"F39.opExtrude","CAP_FACE",FACE,{"disambiguationData":[OSD([sQuery(id+"F38.wireOp",EDGE,"E108.bottom"),sQuery(id+"F38.wireOp",EDGE,"E108.top"),sQuery(id+"F38.wireOp",EDGE,"E108.left"),sQuery(id+"F38.wireOp",EDGE,"E108.right")])],"isStart":false})]});
            var Q1;
            Q1=makeQuery(id+"F43.opChamfer","BLEND_EDGE",EDGE,{"blendedFrom":[makeQuery(id+"F42.boolean.opBoolean","COPY",EDGE,{"derivedFrom":makeQuery(id+"F42.opExtrude","CAP_EDGE",EDGE,{"disambiguationData":[OSD([sQuery(id+"F41.wireOp",EDGE,"E110.8.1.0")])],"isStart":false})}),makeQuery(id+"F39.opExtrude","CAP_FACE",FACE,{"disambiguationData":[OSD([sQuery(id+"F38.wireOp",EDGE,"E108.bottom"),sQuery(id+"F38.wireOp",EDGE,"E108.top"),sQuery(id+"F38.wireOp",EDGE,"E108.left"),sQuery(id+"F38.wireOp",EDGE,"E108.right")])],"isStart":false})],"blendedInto":[makeQuery(id+"F39.opExtrude","CAP_FACE",FACE,{"disambiguationData":[OSD([sQuery(id+"F38.wireOp",EDGE,"E108.bottom"),sQuery(id+"F38.wireOp",EDGE,"E108.top"),sQuery(id+"F38.wireOp",EDGE,"E108.left"),sQuery(id+"F38.wireOp",EDGE,"E108.right")])],"isStart":false})]});
            var Q2;
            Q2=makeQuery(id+"F43.opChamfer","BLEND_EDGE",EDGE,{"blendedFrom":[makeQuery(id+"F42.boolean.opBoolean","COPY",EDGE,{"derivedFrom":makeQuery(id+"F42.opExtrude","CAP_EDGE",EDGE,{"disambiguationData":[OSD([sQuery(id+"F41.wireOp",EDGE,"E110.8.2.0")])],"isStart":false})}),makeQuery(id+"F39.opExtrude","CAP_FACE",FACE,{"disambiguationData":[OSD([sQuery(id+"F38.wireOp",EDGE,"E108.bottom"),sQuery(id+"F38.wireOp",EDGE,"E108.top"),sQuery(id+"F38.wireOp",EDGE,"E108.left"),sQuery(id+"F38.wireOp",EDGE,"E108.right")])],"isStart":false})],"blendedInto":[makeQuery(id+"F39.opExtrude","CAP_FACE",FACE,{"disambiguationData":[OSD([sQuery(id+"F38.wireOp",EDGE,"E108.bottom"),sQuery(id+"F38.wireOp",EDGE,"E108.top"),sQuery(id+"F38.wireOp",EDGE,"E108.left"),sQuery(id+"F38.wireOp",EDGE,"E108.right")])],"isStart":false})]});
            var Q3;
            Q3=makeQuery(id+"F43.opChamfer","BLEND_EDGE",EDGE,{"blendedFrom":[makeQuery(id+"F42.boolean.opBoolean","COPY",EDGE,{"derivedFrom":makeQuery(id+"F42.opExtrude","CAP_EDGE",EDGE,{"disambiguationData":[OSD([sQuery(id+"F41.wireOp",EDGE,"E110.7.1.0")])],"isStart":false})}),makeQuery(id+"F39.opExtrude","CAP_FACE",FACE,{"disambiguationData":[OSD([sQuery(id+"F38.wireOp",EDGE,"E108.bottom"),sQuery(id+"F38.wireOp",EDGE,"E108.top"),sQuery(id+"F38.wireOp",EDGE,"E108.left"),sQuery(id+"F38.wireOp",EDGE,"E108.right")])],"isStart":false})],"blendedInto":[makeQuery(id+"F39.opExtrude","CAP_FACE",FACE,{"disambiguationData":[OSD([sQuery(id+"F38.wireOp",EDGE,"E108.bottom"),sQuery(id+"F38.wireOp",EDGE,"E108.top"),sQuery(id+"F38.wireOp",EDGE,"E108.left"),sQuery(id+"F38.wireOp",EDGE,"E108.right")])],"isStart":false})]});
            var Q4;
            Q4=makeQuery(id+"F43.opChamfer","BLEND_EDGE",EDGE,{"blendedFrom":[makeQuery(id+"F42.boolean.opBoolean","COPY",EDGE,{"derivedFrom":makeQuery(id+"F42.opExtrude","CAP_EDGE",EDGE,{"disambiguationData":[OSD([sQuery(id+"F41.wireOp",EDGE,"E110.7.0.0")])],"isStart":false})}),makeQuery(id+"F39.opExtrude","CAP_FACE",FACE,{"disambiguationData":[OSD([sQuery(id+"F38.wireOp",EDGE,"E108.bottom"),sQuery(id+"F38.wireOp",EDGE,"E108.top"),sQuery(id+"F38.wireOp",EDGE,"E108.left"),sQuery(id+"F38.wireOp",EDGE,"E108.right")])],"isStart":false})],"blendedInto":[makeQuery(id+"F39.opExtrude","CAP_FACE",FACE,{"disambiguationData":[OSD([sQuery(id+"F38.wireOp",EDGE,"E108.bottom"),sQuery(id+"F38.wireOp",EDGE,"E108.top"),sQuery(id+"F38.wireOp",EDGE,"E108.left"),sQuery(id+"F38.wireOp",EDGE,"E108.right")])],"isStart":false})]});
            var Q5;
            Q5=makeQuery(id+"F43.opChamfer","BLEND_EDGE",EDGE,{"blendedFrom":[makeQuery(id+"F42.boolean.opBoolean","COPY",EDGE,{"derivedFrom":makeQuery(id+"F42.opExtrude","CAP_EDGE",EDGE,{"disambiguationData":[OSD([sQuery(id+"F41.wireOp",EDGE,"E110.8.3.0")])],"isStart":false})}),makeQuery(id+"F39.opExtrude","CAP_FACE",FACE,{"disambiguationData":[OSD([sQuery(id+"F38.wireOp",EDGE,"E108.bottom"),sQuery(id+"F38.wireOp",EDGE,"E108.top"),sQuery(id+"F38.wireOp",EDGE,"E108.left"),sQuery(id+"F38.wireOp",EDGE,"E108.right")])],"isStart":false})],"blendedInto":[makeQuery(id+"F39.opExtrude","CAP_FACE",FACE,{"disambiguationData":[OSD([sQuery(id+"F38.wireOp",EDGE,"E108.bottom"),sQuery(id+"F38.wireOp",EDGE,"E108.top"),sQuery(id+"F38.wireOp",EDGE,"E108.left"),sQuery(id+"F38.wireOp",EDGE,"E108.right")])],"isStart":false})]});
            var Q6;
            Q6=makeQuery(id+"F43.opChamfer","BLEND_EDGE",EDGE,{"blendedFrom":[makeQuery(id+"F42.boolean.opBoolean","COPY",EDGE,{"derivedFrom":makeQuery(id+"F42.opExtrude","CAP_EDGE",EDGE,{"disambiguationData":[OSD([sQuery(id+"F41.wireOp",EDGE,"E110.8.4.0")])],"isStart":false})}),makeQuery(id+"F39.opExtrude","CAP_FACE",FACE,{"disambiguationData":[OSD([sQuery(id+"F38.wireOp",EDGE,"E108.bottom"),sQuery(id+"F38.wireOp",EDGE,"E108.top"),sQuery(id+"F38.wireOp",EDGE,"E108.left"),sQuery(id+"F38.wireOp",EDGE,"E108.right")])],"isStart":false})],"blendedInto":[makeQuery(id+"F39.opExtrude","CAP_FACE",FACE,{"disambiguationData":[OSD([sQuery(id+"F38.wireOp",EDGE,"E108.bottom"),sQuery(id+"F38.wireOp",EDGE,"E108.top"),sQuery(id+"F38.wireOp",EDGE,"E108.left"),sQuery(id+"F38.wireOp",EDGE,"E108.right")])],"isStart":false})]});
            var Q7;
            Q7=makeQuery(id+"F43.opChamfer","BLEND_EDGE",EDGE,{"blendedFrom":[makeQuery(id+"F42.boolean.opBoolean","COPY",EDGE,{"derivedFrom":makeQuery(id+"F42.opExtrude","CAP_EDGE",EDGE,{"disambiguationData":[OSD([sQuery(id+"F41.wireOp",EDGE,"E110.8.5.0")])],"isStart":false})}),makeQuery(id+"F39.opExtrude","CAP_FACE",FACE,{"disambiguationData":[OSD([sQuery(id+"F38.wireOp",EDGE,"E108.bottom"),sQuery(id+"F38.wireOp",EDGE,"E108.top"),sQuery(id+"F38.wireOp",EDGE,"E108.left"),sQuery(id+"F38.wireOp",EDGE,"E108.right")])],"isStart":false})],"blendedInto":[makeQuery(id+"F39.opExtrude","CAP_FACE",FACE,{"disambiguationData":[OSD([sQuery(id+"F38.wireOp",EDGE,"E108.bottom"),sQuery(id+"F38.wireOp",EDGE,"E108.top"),sQuery(id+"F38.wireOp",EDGE,"E108.left"),sQuery(id+"F38.wireOp",EDGE,"E108.right")])],"isStart":false})]});
            var Q8;
            Q8=makeQuery(id+"F43.opChamfer","BLEND_EDGE",EDGE,{"blendedFrom":[makeQuery(id+"F42.boolean.opBoolean","COPY",EDGE,{"derivedFrom":makeQuery(id+"F42.opExtrude","CAP_EDGE",EDGE,{"disambiguationData":[OSD([sQuery(id+"F41.wireOp",EDGE,"E110.8.6.0")])],"isStart":false})}),makeQuery(id+"F39.opExtrude","CAP_FACE",FACE,{"disambiguationData":[OSD([sQuery(id+"F38.wireOp",EDGE,"E108.bottom"),sQuery(id+"F38.wireOp",EDGE,"E108.top"),sQuery(id+"F38.wireOp",EDGE,"E108.left"),sQuery(id+"F38.wireOp",EDGE,"E108.right")])],"isStart":false})],"blendedInto":[makeQuery(id+"F39.opExtrude","CAP_FACE",FACE,{"disambiguationData":[OSD([sQuery(id+"F38.wireOp",EDGE,"E108.bottom"),sQuery(id+"F38.wireOp",EDGE,"E108.top"),sQuery(id+"F38.wireOp",EDGE,"E108.left"),sQuery(id+"F38.wireOp",EDGE,"E108.right")])],"isStart":false})]});
            var Q9;
            Q9=makeQuery(id+"F43.opChamfer","BLEND_EDGE",EDGE,{"blendedFrom":[makeQuery(id+"F42.boolean.opBoolean","COPY",EDGE,{"derivedFrom":makeQuery(id+"F42.opExtrude","CAP_EDGE",EDGE,{"disambiguationData":[OSD([sQuery(id+"F41.wireOp",EDGE,"E110.7.5.0")])],"isStart":false})}),makeQuery(id+"F39.opExtrude","CAP_FACE",FACE,{"disambiguationData":[OSD([sQuery(id+"F38.wireOp",EDGE,"E108.bottom"),sQuery(id+"F38.wireOp",EDGE,"E108.top"),sQuery(id+"F38.wireOp",EDGE,"E108.left"),sQuery(id+"F38.wireOp",EDGE,"E108.right")])],"isStart":false})],"blendedInto":[makeQuery(id+"F39.opExtrude","CAP_FACE",FACE,{"disambiguationData":[OSD([sQuery(id+"F38.wireOp",EDGE,"E108.bottom"),sQuery(id+"F38.wireOp",EDGE,"E108.top"),sQuery(id+"F38.wireOp",EDGE,"E108.left"),sQuery(id+"F38.wireOp",EDGE,"E108.right")])],"isStart":false})]});
            var Q10;
            Q10=makeQuery(id+"F43.opChamfer","BLEND_EDGE",EDGE,{"blendedFrom":[makeQuery(id+"F42.boolean.opBoolean","COPY",EDGE,{"derivedFrom":makeQuery(id+"F42.opExtrude","CAP_EDGE",EDGE,{"disambiguationData":[OSD([sQuery(id+"F41.wireOp",EDGE,"E110.7.4.0")])],"isStart":false})}),makeQuery(id+"F39.opExtrude","CAP_FACE",FACE,{"disambiguationData":[OSD([sQuery(id+"F38.wireOp",EDGE,"E108.bottom"),sQuery(id+"F38.wireOp",EDGE,"E108.top"),sQuery(id+"F38.wireOp",EDGE,"E108.left"),sQuery(id+"F38.wireOp",EDGE,"E108.right")])],"isStart":false})],"blendedInto":[makeQuery(id+"F39.opExtrude","CAP_FACE",FACE,{"disambiguationData":[OSD([sQuery(id+"F38.wireOp",EDGE,"E108.bottom"),sQuery(id+"F38.wireOp",EDGE,"E108.top"),sQuery(id+"F38.wireOp",EDGE,"E108.left"),sQuery(id+"F38.wireOp",EDGE,"E108.right")])],"isStart":false})]});
            var Q11;
            Q11=makeQuery(id+"F43.opChamfer","BLEND_EDGE",EDGE,{"blendedFrom":[makeQuery(id+"F42.boolean.opBoolean","COPY",EDGE,{"derivedFrom":makeQuery(id+"F42.opExtrude","CAP_EDGE",EDGE,{"disambiguationData":[OSD([sQuery(id+"F41.wireOp",EDGE,"E110.7.3.0")])],"isStart":false})}),makeQuery(id+"F39.opExtrude","CAP_FACE",FACE,{"disambiguationData":[OSD([sQuery(id+"F38.wireOp",EDGE,"E108.bottom"),sQuery(id+"F38.wireOp",EDGE,"E108.top"),sQuery(id+"F38.wireOp",EDGE,"E108.left"),sQuery(id+"F38.wireOp",EDGE,"E108.right")])],"isStart":false})],"blendedInto":[makeQuery(id+"F39.opExtrude","CAP_FACE",FACE,{"disambiguationData":[OSD([sQuery(id+"F38.wireOp",EDGE,"E108.bottom"),sQuery(id+"F38.wireOp",EDGE,"E108.top"),sQuery(id+"F38.wireOp",EDGE,"E108.left"),sQuery(id+"F38.wireOp",EDGE,"E108.right")])],"isStart":false})]});
            var Q12;
            Q12=makeQuery(id+"F43.opChamfer","BLEND_EDGE",EDGE,{"blendedFrom":[makeQuery(id+"F42.boolean.opBoolean","COPY",EDGE,{"derivedFrom":makeQuery(id+"F42.opExtrude","CAP_EDGE",EDGE,{"disambiguationData":[OSD([sQuery(id+"F41.wireOp",EDGE,"E110.7.2.0")])],"isStart":false})}),makeQuery(id+"F39.opExtrude","CAP_FACE",FACE,{"disambiguationData":[OSD([sQuery(id+"F38.wireOp",EDGE,"E108.bottom"),sQuery(id+"F38.wireOp",EDGE,"E108.top"),sQuery(id+"F38.wireOp",EDGE,"E108.left"),sQuery(id+"F38.wireOp",EDGE,"E108.right")])],"isStart":false})],"blendedInto":[makeQuery(id+"F39.opExtrude","CAP_FACE",FACE,{"disambiguationData":[OSD([sQuery(id+"F38.wireOp",EDGE,"E108.bottom"),sQuery(id+"F38.wireOp",EDGE,"E108.top"),sQuery(id+"F38.wireOp",EDGE,"E108.left"),sQuery(id+"F38.wireOp",EDGE,"E108.right")])],"isStart":false})]});
            var Q13;
            Q13=makeQuery(id+"F43.opChamfer","BLEND_EDGE",EDGE,{"blendedFrom":[makeQuery(id+"F42.boolean.opBoolean","COPY",EDGE,{"derivedFrom":makeQuery(id+"F42.opExtrude","CAP_EDGE",EDGE,{"disambiguationData":[OSD([sQuery(id+"F41.wireOp",EDGE,"E110.6.0.0")])],"isStart":false})}),makeQuery(id+"F39.opExtrude","CAP_FACE",FACE,{"disambiguationData":[OSD([sQuery(id+"F38.wireOp",EDGE,"E108.bottom"),sQuery(id+"F38.wireOp",EDGE,"E108.top"),sQuery(id+"F38.wireOp",EDGE,"E108.left"),sQuery(id+"F38.wireOp",EDGE,"E108.right")])],"isStart":false})],"blendedInto":[makeQuery(id+"F39.opExtrude","CAP_FACE",FACE,{"disambiguationData":[OSD([sQuery(id+"F38.wireOp",EDGE,"E108.bottom"),sQuery(id+"F38.wireOp",EDGE,"E108.top"),sQuery(id+"F38.wireOp",EDGE,"E108.left"),sQuery(id+"F38.wireOp",EDGE,"E108.right")])],"isStart":false})]});
            var Q14;
            Q14=makeQuery(id+"F43.opChamfer","BLEND_EDGE",EDGE,{"blendedFrom":[makeQuery(id+"F42.boolean.opBoolean","COPY",EDGE,{"derivedFrom":makeQuery(id+"F42.opExtrude","CAP_EDGE",EDGE,{"disambiguationData":[OSD([sQuery(id+"F41.wireOp",EDGE,"E110.6.1.0")])],"isStart":false})}),makeQuery(id+"F39.opExtrude","CAP_FACE",FACE,{"disambiguationData":[OSD([sQuery(id+"F38.wireOp",EDGE,"E108.bottom"),sQuery(id+"F38.wireOp",EDGE,"E108.top"),sQuery(id+"F38.wireOp",EDGE,"E108.left"),sQuery(id+"F38.wireOp",EDGE,"E108.right")])],"isStart":false})],"blendedInto":[makeQuery(id+"F39.opExtrude","CAP_FACE",FACE,{"disambiguationData":[OSD([sQuery(id+"F38.wireOp",EDGE,"E108.bottom"),sQuery(id+"F38.wireOp",EDGE,"E108.top"),sQuery(id+"F38.wireOp",EDGE,"E108.left"),sQuery(id+"F38.wireOp",EDGE,"E108.right")])],"isStart":false})]});
            var Q15;
            Q15=makeQuery(id+"F43.opChamfer","BLEND_EDGE",EDGE,{"blendedFrom":[makeQuery(id+"F42.boolean.opBoolean","COPY",EDGE,{"derivedFrom":makeQuery(id+"F42.opExtrude","CAP_EDGE",EDGE,{"disambiguationData":[OSD([sQuery(id+"F41.wireOp",EDGE,"E110.6.2.0")])],"isStart":false})}),makeQuery(id+"F39.opExtrude","CAP_FACE",FACE,{"disambiguationData":[OSD([sQuery(id+"F38.wireOp",EDGE,"E108.bottom"),sQuery(id+"F38.wireOp",EDGE,"E108.top"),sQuery(id+"F38.wireOp",EDGE,"E108.left"),sQuery(id+"F38.wireOp",EDGE,"E108.right")])],"isStart":false})],"blendedInto":[makeQuery(id+"F39.opExtrude","CAP_FACE",FACE,{"disambiguationData":[OSD([sQuery(id+"F38.wireOp",EDGE,"E108.bottom"),sQuery(id+"F38.wireOp",EDGE,"E108.top"),sQuery(id+"F38.wireOp",EDGE,"E108.left"),sQuery(id+"F38.wireOp",EDGE,"E108.right")])],"isStart":false})]});
            var Q16;
            Q16=makeQuery(id+"F43.opChamfer","BLEND_EDGE",EDGE,{"blendedFrom":[makeQuery(id+"F42.boolean.opBoolean","COPY",EDGE,{"derivedFrom":makeQuery(id+"F42.opExtrude","CAP_EDGE",EDGE,{"disambiguationData":[OSD([sQuery(id+"F41.wireOp",EDGE,"E110.6.3.0")])],"isStart":false})}),makeQuery(id+"F39.opExtrude","CAP_FACE",FACE,{"disambiguationData":[OSD([sQuery(id+"F38.wireOp",EDGE,"E108.bottom"),sQuery(id+"F38.wireOp",EDGE,"E108.top"),sQuery(id+"F38.wireOp",EDGE,"E108.left"),sQuery(id+"F38.wireOp",EDGE,"E108.right")])],"isStart":false})],"blendedInto":[makeQuery(id+"F39.opExtrude","CAP_FACE",FACE,{"disambiguationData":[OSD([sQuery(id+"F38.wireOp",EDGE,"E108.bottom"),sQuery(id+"F38.wireOp",EDGE,"E108.top"),sQuery(id+"F38.wireOp",EDGE,"E108.left"),sQuery(id+"F38.wireOp",EDGE,"E108.right")])],"isStart":false})]});
            var Q17;
            Q17=makeQuery(id+"F43.opChamfer","BLEND_EDGE",EDGE,{"blendedFrom":[makeQuery(id+"F42.boolean.opBoolean","COPY",EDGE,{"derivedFrom":makeQuery(id+"F42.opExtrude","CAP_EDGE",EDGE,{"disambiguationData":[OSD([sQuery(id+"F41.wireOp",EDGE,"E110.6.4.0")])],"isStart":false})}),makeQuery(id+"F39.opExtrude","CAP_FACE",FACE,{"disambiguationData":[OSD([sQuery(id+"F38.wireOp",EDGE,"E108.bottom"),sQuery(id+"F38.wireOp",EDGE,"E108.top"),sQuery(id+"F38.wireOp",EDGE,"E108.left"),sQuery(id+"F38.wireOp",EDGE,"E108.right")])],"isStart":false})],"blendedInto":[makeQuery(id+"F39.opExtrude","CAP_FACE",FACE,{"disambiguationData":[OSD([sQuery(id+"F38.wireOp",EDGE,"E108.bottom"),sQuery(id+"F38.wireOp",EDGE,"E108.top"),sQuery(id+"F38.wireOp",EDGE,"E108.left"),sQuery(id+"F38.wireOp",EDGE,"E108.right")])],"isStart":false})]});
            var Q18;
            Q18=makeQuery(id+"F43.opChamfer","BLEND_EDGE",EDGE,{"blendedFrom":[makeQuery(id+"F42.boolean.opBoolean","COPY",EDGE,{"derivedFrom":makeQuery(id+"F42.opExtrude","CAP_EDGE",EDGE,{"disambiguationData":[OSD([sQuery(id+"F41.wireOp",EDGE,"E110.6.5.0")])],"isStart":false})}),makeQuery(id+"F39.opExtrude","CAP_FACE",FACE,{"disambiguationData":[OSD([sQuery(id+"F38.wireOp",EDGE,"E108.bottom"),sQuery(id+"F38.wireOp",EDGE,"E108.top"),sQuery(id+"F38.wireOp",EDGE,"E108.left"),sQuery(id+"F38.wireOp",EDGE,"E108.right")])],"isStart":false})],"blendedInto":[makeQuery(id+"F39.opExtrude","CAP_FACE",FACE,{"disambiguationData":[OSD([sQuery(id+"F38.wireOp",EDGE,"E108.bottom"),sQuery(id+"F38.wireOp",EDGE,"E108.top"),sQuery(id+"F38.wireOp",EDGE,"E108.left"),sQuery(id+"F38.wireOp",EDGE,"E108.right")])],"isStart":false})]});
            var Q19;
            Q19=makeQuery(id+"F43.opChamfer","BLEND_EDGE",EDGE,{"blendedFrom":[makeQuery(id+"F42.boolean.opBoolean","COPY",EDGE,{"derivedFrom":makeQuery(id+"F42.opExtrude","CAP_EDGE",EDGE,{"disambiguationData":[OSD([sQuery(id+"F41.wireOp",EDGE,"E110.7.6.0")])],"isStart":false})}),makeQuery(id+"F39.opExtrude","CAP_FACE",FACE,{"disambiguationData":[OSD([sQuery(id+"F38.wireOp",EDGE,"E108.bottom"),sQuery(id+"F38.wireOp",EDGE,"E108.top"),sQuery(id+"F38.wireOp",EDGE,"E108.left"),sQuery(id+"F38.wireOp",EDGE,"E108.right")])],"isStart":false})],"blendedInto":[makeQuery(id+"F39.opExtrude","CAP_FACE",FACE,{"disambiguationData":[OSD([sQuery(id+"F38.wireOp",EDGE,"E108.bottom"),sQuery(id+"F38.wireOp",EDGE,"E108.top"),sQuery(id+"F38.wireOp",EDGE,"E108.left"),sQuery(id+"F38.wireOp",EDGE,"E108.right")])],"isStart":false})]});
            var Q20;
            Q20=makeQuery(id+"F43.opChamfer","BLEND_EDGE",EDGE,{"blendedFrom":[makeQuery(id+"F42.boolean.opBoolean","COPY",EDGE,{"derivedFrom":makeQuery(id+"F42.opExtrude","CAP_EDGE",EDGE,{"disambiguationData":[OSD([sQuery(id+"F41.wireOp",EDGE,"E110.6.6.0")])],"isStart":false})}),makeQuery(id+"F39.opExtrude","CAP_FACE",FACE,{"disambiguationData":[OSD([sQuery(id+"F38.wireOp",EDGE,"E108.bottom"),sQuery(id+"F38.wireOp",EDGE,"E108.top"),sQuery(id+"F38.wireOp",EDGE,"E108.left"),sQuery(id+"F38.wireOp",EDGE,"E108.right")])],"isStart":false})],"blendedInto":[makeQuery(id+"F39.opExtrude","CAP_FACE",FACE,{"disambiguationData":[OSD([sQuery(id+"F38.wireOp",EDGE,"E108.bottom"),sQuery(id+"F38.wireOp",EDGE,"E108.top"),sQuery(id+"F38.wireOp",EDGE,"E108.left"),sQuery(id+"F38.wireOp",EDGE,"E108.right")])],"isStart":false})]});
            var Q21;
            Q21=makeQuery(id+"F43.opChamfer","BLEND_EDGE",EDGE,{"blendedFrom":[makeQuery(id+"F42.boolean.opBoolean","COPY",EDGE,{"derivedFrom":makeQuery(id+"F42.opExtrude","CAP_EDGE",EDGE,{"disambiguationData":[OSD([sQuery(id+"F41.wireOp",EDGE,"E110.5.6.0")])],"isStart":false})}),makeQuery(id+"F39.opExtrude","CAP_FACE",FACE,{"disambiguationData":[OSD([sQuery(id+"F38.wireOp",EDGE,"E108.bottom"),sQuery(id+"F38.wireOp",EDGE,"E108.top"),sQuery(id+"F38.wireOp",EDGE,"E108.left"),sQuery(id+"F38.wireOp",EDGE,"E108.right")])],"isStart":false})],"blendedInto":[makeQuery(id+"F39.opExtrude","CAP_FACE",FACE,{"disambiguationData":[OSD([sQuery(id+"F38.wireOp",EDGE,"E108.bottom"),sQuery(id+"F38.wireOp",EDGE,"E108.top"),sQuery(id+"F38.wireOp",EDGE,"E108.left"),sQuery(id+"F38.wireOp",EDGE,"E108.right")])],"isStart":false})]});
            var Q22;
            Q22=makeQuery(id+"F43.opChamfer","BLEND_EDGE",EDGE,{"blendedFrom":[makeQuery(id+"F42.boolean.opBoolean","COPY",EDGE,{"derivedFrom":makeQuery(id+"F42.opExtrude","CAP_EDGE",EDGE,{"disambiguationData":[OSD([sQuery(id+"F41.wireOp",EDGE,"E110.4.6.0")])],"isStart":false})}),makeQuery(id+"F39.opExtrude","CAP_FACE",FACE,{"disambiguationData":[OSD([sQuery(id+"F38.wireOp",EDGE,"E108.bottom"),sQuery(id+"F38.wireOp",EDGE,"E108.top"),sQuery(id+"F38.wireOp",EDGE,"E108.left"),sQuery(id+"F38.wireOp",EDGE,"E108.right")])],"isStart":false})],"blendedInto":[makeQuery(id+"F39.opExtrude","CAP_FACE",FACE,{"disambiguationData":[OSD([sQuery(id+"F38.wireOp",EDGE,"E108.bottom"),sQuery(id+"F38.wireOp",EDGE,"E108.top"),sQuery(id+"F38.wireOp",EDGE,"E108.left"),sQuery(id+"F38.wireOp",EDGE,"E108.right")])],"isStart":false})]});
            var Q23;
            Q23=makeQuery(id+"F43.opChamfer","BLEND_EDGE",EDGE,{"blendedFrom":[makeQuery(id+"F42.boolean.opBoolean","COPY",EDGE,{"derivedFrom":makeQuery(id+"F42.opExtrude","CAP_EDGE",EDGE,{"disambiguationData":[OSD([sQuery(id+"F41.wireOp",EDGE,"E110.3.6.0")])],"isStart":false})}),makeQuery(id+"F39.opExtrude","CAP_FACE",FACE,{"disambiguationData":[OSD([sQuery(id+"F38.wireOp",EDGE,"E108.bottom"),sQuery(id+"F38.wireOp",EDGE,"E108.top"),sQuery(id+"F38.wireOp",EDGE,"E108.left"),sQuery(id+"F38.wireOp",EDGE,"E108.right")])],"isStart":false})],"blendedInto":[makeQuery(id+"F39.opExtrude","CAP_FACE",FACE,{"disambiguationData":[OSD([sQuery(id+"F38.wireOp",EDGE,"E108.bottom"),sQuery(id+"F38.wireOp",EDGE,"E108.top"),sQuery(id+"F38.wireOp",EDGE,"E108.left"),sQuery(id+"F38.wireOp",EDGE,"E108.right")])],"isStart":false})]});
            var Q24;
            Q24=makeQuery(id+"F43.opChamfer","BLEND_EDGE",EDGE,{"blendedFrom":[makeQuery(id+"F42.boolean.opBoolean","COPY",EDGE,{"derivedFrom":makeQuery(id+"F42.opExtrude","CAP_EDGE",EDGE,{"disambiguationData":[OSD([sQuery(id+"F41.wireOp",EDGE,"E110.2.6.0")])],"isStart":false})}),makeQuery(id+"F39.opExtrude","CAP_FACE",FACE,{"disambiguationData":[OSD([sQuery(id+"F38.wireOp",EDGE,"E108.bottom"),sQuery(id+"F38.wireOp",EDGE,"E108.top"),sQuery(id+"F38.wireOp",EDGE,"E108.left"),sQuery(id+"F38.wireOp",EDGE,"E108.right")])],"isStart":false})],"blendedInto":[makeQuery(id+"F39.opExtrude","CAP_FACE",FACE,{"disambiguationData":[OSD([sQuery(id+"F38.wireOp",EDGE,"E108.bottom"),sQuery(id+"F38.wireOp",EDGE,"E108.top"),sQuery(id+"F38.wireOp",EDGE,"E108.left"),sQuery(id+"F38.wireOp",EDGE,"E108.right")])],"isStart":false})]});
            var Q25;
            Q25=makeQuery(id+"F43.opChamfer","BLEND_EDGE",EDGE,{"blendedFrom":[makeQuery(id+"F42.boolean.opBoolean","COPY",EDGE,{"derivedFrom":makeQuery(id+"F42.opExtrude","CAP_EDGE",EDGE,{"disambiguationData":[OSD([sQuery(id+"F41.wireOp",EDGE,"E110.2.5.0")])],"isStart":false})}),makeQuery(id+"F39.opExtrude","CAP_FACE",FACE,{"disambiguationData":[OSD([sQuery(id+"F38.wireOp",EDGE,"E108.bottom"),sQuery(id+"F38.wireOp",EDGE,"E108.top"),sQuery(id+"F38.wireOp",EDGE,"E108.left"),sQuery(id+"F38.wireOp",EDGE,"E108.right")])],"isStart":false})],"blendedInto":[makeQuery(id+"F39.opExtrude","CAP_FACE",FACE,{"disambiguationData":[OSD([sQuery(id+"F38.wireOp",EDGE,"E108.bottom"),sQuery(id+"F38.wireOp",EDGE,"E108.top"),sQuery(id+"F38.wireOp",EDGE,"E108.left"),sQuery(id+"F38.wireOp",EDGE,"E108.right")])],"isStart":false})]});
            var Q26;
            Q26=makeQuery(id+"F43.opChamfer","BLEND_EDGE",EDGE,{"blendedFrom":[makeQuery(id+"F42.boolean.opBoolean","COPY",EDGE,{"derivedFrom":makeQuery(id+"F42.opExtrude","CAP_EDGE",EDGE,{"disambiguationData":[OSD([sQuery(id+"F41.wireOp",EDGE,"E110.3.5.0")])],"isStart":false})}),makeQuery(id+"F39.opExtrude","CAP_FACE",FACE,{"disambiguationData":[OSD([sQuery(id+"F38.wireOp",EDGE,"E108.bottom"),sQuery(id+"F38.wireOp",EDGE,"E108.top"),sQuery(id+"F38.wireOp",EDGE,"E108.left"),sQuery(id+"F38.wireOp",EDGE,"E108.right")])],"isStart":false})],"blendedInto":[makeQuery(id+"F39.opExtrude","CAP_FACE",FACE,{"disambiguationData":[OSD([sQuery(id+"F38.wireOp",EDGE,"E108.bottom"),sQuery(id+"F38.wireOp",EDGE,"E108.top"),sQuery(id+"F38.wireOp",EDGE,"E108.left"),sQuery(id+"F38.wireOp",EDGE,"E108.right")])],"isStart":false})]});
            var Q27;
            Q27=makeQuery(id+"F43.opChamfer","BLEND_EDGE",EDGE,{"blendedFrom":[makeQuery(id+"F42.boolean.opBoolean","COPY",EDGE,{"derivedFrom":makeQuery(id+"F42.opExtrude","CAP_EDGE",EDGE,{"disambiguationData":[OSD([sQuery(id+"F41.wireOp",EDGE,"E110.4.5.0")])],"isStart":false})}),makeQuery(id+"F39.opExtrude","CAP_FACE",FACE,{"disambiguationData":[OSD([sQuery(id+"F38.wireOp",EDGE,"E108.bottom"),sQuery(id+"F38.wireOp",EDGE,"E108.top"),sQuery(id+"F38.wireOp",EDGE,"E108.left"),sQuery(id+"F38.wireOp",EDGE,"E108.right")])],"isStart":false})],"blendedInto":[makeQuery(id+"F39.opExtrude","CAP_FACE",FACE,{"disambiguationData":[OSD([sQuery(id+"F38.wireOp",EDGE,"E108.bottom"),sQuery(id+"F38.wireOp",EDGE,"E108.top"),sQuery(id+"F38.wireOp",EDGE,"E108.left"),sQuery(id+"F38.wireOp",EDGE,"E108.right")])],"isStart":false})]});
            var Q28;
            Q28=makeQuery(id+"F43.opChamfer","BLEND_EDGE",EDGE,{"blendedFrom":[makeQuery(id+"F42.boolean.opBoolean","COPY",EDGE,{"derivedFrom":makeQuery(id+"F42.opExtrude","CAP_EDGE",EDGE,{"disambiguationData":[OSD([sQuery(id+"F41.wireOp",EDGE,"E110.5.5.0")])],"isStart":false})}),makeQuery(id+"F39.opExtrude","CAP_FACE",FACE,{"disambiguationData":[OSD([sQuery(id+"F38.wireOp",EDGE,"E108.bottom"),sQuery(id+"F38.wireOp",EDGE,"E108.top"),sQuery(id+"F38.wireOp",EDGE,"E108.left"),sQuery(id+"F38.wireOp",EDGE,"E108.right")])],"isStart":false})],"blendedInto":[makeQuery(id+"F39.opExtrude","CAP_FACE",FACE,{"disambiguationData":[OSD([sQuery(id+"F38.wireOp",EDGE,"E108.bottom"),sQuery(id+"F38.wireOp",EDGE,"E108.top"),sQuery(id+"F38.wireOp",EDGE,"E108.left"),sQuery(id+"F38.wireOp",EDGE,"E108.right")])],"isStart":false})]});
            var Q29;
            Q29=makeQuery(id+"F43.opChamfer","BLEND_EDGE",EDGE,{"blendedFrom":[makeQuery(id+"F42.boolean.opBoolean","COPY",EDGE,{"derivedFrom":makeQuery(id+"F42.opExtrude","CAP_EDGE",EDGE,{"disambiguationData":[OSD([sQuery(id+"F41.wireOp",EDGE,"E110.5.4.0")])],"isStart":false})}),makeQuery(id+"F39.opExtrude","CAP_FACE",FACE,{"disambiguationData":[OSD([sQuery(id+"F38.wireOp",EDGE,"E108.bottom"),sQuery(id+"F38.wireOp",EDGE,"E108.top"),sQuery(id+"F38.wireOp",EDGE,"E108.left"),sQuery(id+"F38.wireOp",EDGE,"E108.right")])],"isStart":false})],"blendedInto":[makeQuery(id+"F39.opExtrude","CAP_FACE",FACE,{"disambiguationData":[OSD([sQuery(id+"F38.wireOp",EDGE,"E108.bottom"),sQuery(id+"F38.wireOp",EDGE,"E108.top"),sQuery(id+"F38.wireOp",EDGE,"E108.left"),sQuery(id+"F38.wireOp",EDGE,"E108.right")])],"isStart":false})]});
            var Q30;
            Q30=makeQuery(id+"F43.opChamfer","BLEND_EDGE",EDGE,{"blendedFrom":[makeQuery(id+"F42.boolean.opBoolean","COPY",EDGE,{"derivedFrom":makeQuery(id+"F42.opExtrude","CAP_EDGE",EDGE,{"disambiguationData":[OSD([sQuery(id+"F41.wireOp",EDGE,"E110.4.4.0")])],"isStart":false})}),makeQuery(id+"F39.opExtrude","CAP_FACE",FACE,{"disambiguationData":[OSD([sQuery(id+"F38.wireOp",EDGE,"E108.bottom"),sQuery(id+"F38.wireOp",EDGE,"E108.top"),sQuery(id+"F38.wireOp",EDGE,"E108.left"),sQuery(id+"F38.wireOp",EDGE,"E108.right")])],"isStart":false})],"blendedInto":[makeQuery(id+"F39.opExtrude","CAP_FACE",FACE,{"disambiguationData":[OSD([sQuery(id+"F38.wireOp",EDGE,"E108.bottom"),sQuery(id+"F38.wireOp",EDGE,"E108.top"),sQuery(id+"F38.wireOp",EDGE,"E108.left"),sQuery(id+"F38.wireOp",EDGE,"E108.right")])],"isStart":false})]});
            var Q31;
            Q31=makeQuery(id+"F43.opChamfer","BLEND_EDGE",EDGE,{"blendedFrom":[makeQuery(id+"F42.boolean.opBoolean","COPY",EDGE,{"derivedFrom":makeQuery(id+"F42.opExtrude","CAP_EDGE",EDGE,{"disambiguationData":[OSD([sQuery(id+"F41.wireOp",EDGE,"E110.3.4.0")])],"isStart":false})}),makeQuery(id+"F39.opExtrude","CAP_FACE",FACE,{"disambiguationData":[OSD([sQuery(id+"F38.wireOp",EDGE,"E108.bottom"),sQuery(id+"F38.wireOp",EDGE,"E108.top"),sQuery(id+"F38.wireOp",EDGE,"E108.left"),sQuery(id+"F38.wireOp",EDGE,"E108.right")])],"isStart":false})],"blendedInto":[makeQuery(id+"F39.opExtrude","CAP_FACE",FACE,{"disambiguationData":[OSD([sQuery(id+"F38.wireOp",EDGE,"E108.bottom"),sQuery(id+"F38.wireOp",EDGE,"E108.top"),sQuery(id+"F38.wireOp",EDGE,"E108.left"),sQuery(id+"F38.wireOp",EDGE,"E108.right")])],"isStart":false})]});
            var Q32;
            Q32=makeQuery(id+"F43.opChamfer","BLEND_EDGE",EDGE,{"blendedFrom":[makeQuery(id+"F42.boolean.opBoolean","COPY",EDGE,{"derivedFrom":makeQuery(id+"F42.opExtrude","CAP_EDGE",EDGE,{"disambiguationData":[OSD([sQuery(id+"F41.wireOp",EDGE,"E110.2.4.0")])],"isStart":false})}),makeQuery(id+"F39.opExtrude","CAP_FACE",FACE,{"disambiguationData":[OSD([sQuery(id+"F38.wireOp",EDGE,"E108.bottom"),sQuery(id+"F38.wireOp",EDGE,"E108.top"),sQuery(id+"F38.wireOp",EDGE,"E108.left"),sQuery(id+"F38.wireOp",EDGE,"E108.right")])],"isStart":false})],"blendedInto":[makeQuery(id+"F39.opExtrude","CAP_FACE",FACE,{"disambiguationData":[OSD([sQuery(id+"F38.wireOp",EDGE,"E108.bottom"),sQuery(id+"F38.wireOp",EDGE,"E108.top"),sQuery(id+"F38.wireOp",EDGE,"E108.left"),sQuery(id+"F38.wireOp",EDGE,"E108.right")])],"isStart":false})]});
            var Q33;
            Q33=makeQuery(id+"F43.opChamfer","BLEND_EDGE",EDGE,{"blendedFrom":[makeQuery(id+"F42.boolean.opBoolean","COPY",EDGE,{"derivedFrom":makeQuery(id+"F42.opExtrude","CAP_EDGE",EDGE,{"disambiguationData":[OSD([sQuery(id+"F41.wireOp",EDGE,"E110.2.3.0")])],"isStart":false})}),makeQuery(id+"F39.opExtrude","CAP_FACE",FACE,{"disambiguationData":[OSD([sQuery(id+"F38.wireOp",EDGE,"E108.bottom"),sQuery(id+"F38.wireOp",EDGE,"E108.top"),sQuery(id+"F38.wireOp",EDGE,"E108.left"),sQuery(id+"F38.wireOp",EDGE,"E108.right")])],"isStart":false})],"blendedInto":[makeQuery(id+"F39.opExtrude","CAP_FACE",FACE,{"disambiguationData":[OSD([sQuery(id+"F38.wireOp",EDGE,"E108.bottom"),sQuery(id+"F38.wireOp",EDGE,"E108.top"),sQuery(id+"F38.wireOp",EDGE,"E108.left"),sQuery(id+"F38.wireOp",EDGE,"E108.right")])],"isStart":false})]});
            var Q34;
            Q34=makeQuery(id+"F43.opChamfer","BLEND_EDGE",EDGE,{"blendedFrom":[makeQuery(id+"F42.boolean.opBoolean","COPY",EDGE,{"derivedFrom":makeQuery(id+"F42.opExtrude","CAP_EDGE",EDGE,{"disambiguationData":[OSD([sQuery(id+"F41.wireOp",EDGE,"E110.3.3.0")])],"isStart":false})}),makeQuery(id+"F39.opExtrude","CAP_FACE",FACE,{"disambiguationData":[OSD([sQuery(id+"F38.wireOp",EDGE,"E108.bottom"),sQuery(id+"F38.wireOp",EDGE,"E108.top"),sQuery(id+"F38.wireOp",EDGE,"E108.left"),sQuery(id+"F38.wireOp",EDGE,"E108.right")])],"isStart":false})],"blendedInto":[makeQuery(id+"F39.opExtrude","CAP_FACE",FACE,{"disambiguationData":[OSD([sQuery(id+"F38.wireOp",EDGE,"E108.bottom"),sQuery(id+"F38.wireOp",EDGE,"E108.top"),sQuery(id+"F38.wireOp",EDGE,"E108.left"),sQuery(id+"F38.wireOp",EDGE,"E108.right")])],"isStart":false})]});
            var Q35;
            Q35=makeQuery(id+"F43.opChamfer","BLEND_EDGE",EDGE,{"blendedFrom":[makeQuery(id+"F42.boolean.opBoolean","COPY",EDGE,{"derivedFrom":makeQuery(id+"F42.opExtrude","CAP_EDGE",EDGE,{"disambiguationData":[OSD([sQuery(id+"F41.wireOp",EDGE,"E110.4.3.0")])],"isStart":false})}),makeQuery(id+"F39.opExtrude","CAP_FACE",FACE,{"disambiguationData":[OSD([sQuery(id+"F38.wireOp",EDGE,"E108.bottom"),sQuery(id+"F38.wireOp",EDGE,"E108.top"),sQuery(id+"F38.wireOp",EDGE,"E108.left"),sQuery(id+"F38.wireOp",EDGE,"E108.right")])],"isStart":false})],"blendedInto":[makeQuery(id+"F39.opExtrude","CAP_FACE",FACE,{"disambiguationData":[OSD([sQuery(id+"F38.wireOp",EDGE,"E108.bottom"),sQuery(id+"F38.wireOp",EDGE,"E108.top"),sQuery(id+"F38.wireOp",EDGE,"E108.left"),sQuery(id+"F38.wireOp",EDGE,"E108.right")])],"isStart":false})]});
            var Q36;
            Q36=makeQuery(id+"F43.opChamfer","BLEND_EDGE",EDGE,{"blendedFrom":[makeQuery(id+"F42.boolean.opBoolean","COPY",EDGE,{"derivedFrom":makeQuery(id+"F42.opExtrude","CAP_EDGE",EDGE,{"disambiguationData":[OSD([sQuery(id+"F41.wireOp",EDGE,"E110.5.3.0")])],"isStart":false})}),makeQuery(id+"F39.opExtrude","CAP_FACE",FACE,{"disambiguationData":[OSD([sQuery(id+"F38.wireOp",EDGE,"E108.bottom"),sQuery(id+"F38.wireOp",EDGE,"E108.top"),sQuery(id+"F38.wireOp",EDGE,"E108.left"),sQuery(id+"F38.wireOp",EDGE,"E108.right")])],"isStart":false})],"blendedInto":[makeQuery(id+"F39.opExtrude","CAP_FACE",FACE,{"disambiguationData":[OSD([sQuery(id+"F38.wireOp",EDGE,"E108.bottom"),sQuery(id+"F38.wireOp",EDGE,"E108.top"),sQuery(id+"F38.wireOp",EDGE,"E108.left"),sQuery(id+"F38.wireOp",EDGE,"E108.right")])],"isStart":false})]});
            var Q37;
            Q37=makeQuery(id+"F43.opChamfer","BLEND_EDGE",EDGE,{"blendedFrom":[makeQuery(id+"F42.boolean.opBoolean","COPY",EDGE,{"derivedFrom":makeQuery(id+"F42.opExtrude","CAP_EDGE",EDGE,{"disambiguationData":[OSD([sQuery(id+"F41.wireOp",EDGE,"E110.5.2.0")])],"isStart":false})}),makeQuery(id+"F39.opExtrude","CAP_FACE",FACE,{"disambiguationData":[OSD([sQuery(id+"F38.wireOp",EDGE,"E108.bottom"),sQuery(id+"F38.wireOp",EDGE,"E108.top"),sQuery(id+"F38.wireOp",EDGE,"E108.left"),sQuery(id+"F38.wireOp",EDGE,"E108.right")])],"isStart":false})],"blendedInto":[makeQuery(id+"F39.opExtrude","CAP_FACE",FACE,{"disambiguationData":[OSD([sQuery(id+"F38.wireOp",EDGE,"E108.bottom"),sQuery(id+"F38.wireOp",EDGE,"E108.top"),sQuery(id+"F38.wireOp",EDGE,"E108.left"),sQuery(id+"F38.wireOp",EDGE,"E108.right")])],"isStart":false})]});
            var Q38;
            Q38=makeQuery(id+"F43.opChamfer","BLEND_EDGE",EDGE,{"blendedFrom":[makeQuery(id+"F42.boolean.opBoolean","COPY",EDGE,{"derivedFrom":makeQuery(id+"F42.opExtrude","CAP_EDGE",EDGE,{"disambiguationData":[OSD([sQuery(id+"F41.wireOp",EDGE,"E110.5.1.0")])],"isStart":false})}),makeQuery(id+"F39.opExtrude","CAP_FACE",FACE,{"disambiguationData":[OSD([sQuery(id+"F38.wireOp",EDGE,"E108.bottom"),sQuery(id+"F38.wireOp",EDGE,"E108.top"),sQuery(id+"F38.wireOp",EDGE,"E108.left"),sQuery(id+"F38.wireOp",EDGE,"E108.right")])],"isStart":false})],"blendedInto":[makeQuery(id+"F39.opExtrude","CAP_FACE",FACE,{"disambiguationData":[OSD([sQuery(id+"F38.wireOp",EDGE,"E108.bottom"),sQuery(id+"F38.wireOp",EDGE,"E108.top"),sQuery(id+"F38.wireOp",EDGE,"E108.left"),sQuery(id+"F38.wireOp",EDGE,"E108.right")])],"isStart":false})]});
            var Q39;
            Q39=makeQuery(id+"F43.opChamfer","BLEND_EDGE",EDGE,{"blendedFrom":[makeQuery(id+"F42.boolean.opBoolean","COPY",EDGE,{"derivedFrom":makeQuery(id+"F42.opExtrude","CAP_EDGE",EDGE,{"disambiguationData":[OSD([sQuery(id+"F41.wireOp",EDGE,"E110.5.0.0")])],"isStart":false})}),makeQuery(id+"F39.opExtrude","CAP_FACE",FACE,{"disambiguationData":[OSD([sQuery(id+"F38.wireOp",EDGE,"E108.bottom"),sQuery(id+"F38.wireOp",EDGE,"E108.top"),sQuery(id+"F38.wireOp",EDGE,"E108.left"),sQuery(id+"F38.wireOp",EDGE,"E108.right")])],"isStart":false})],"blendedInto":[makeQuery(id+"F39.opExtrude","CAP_FACE",FACE,{"disambiguationData":[OSD([sQuery(id+"F38.wireOp",EDGE,"E108.bottom"),sQuery(id+"F38.wireOp",EDGE,"E108.top"),sQuery(id+"F38.wireOp",EDGE,"E108.left"),sQuery(id+"F38.wireOp",EDGE,"E108.right")])],"isStart":false})]});
            var Q40;
            Q40=makeQuery(id+"F43.opChamfer","BLEND_EDGE",EDGE,{"blendedFrom":[makeQuery(id+"F42.boolean.opBoolean","COPY",EDGE,{"derivedFrom":makeQuery(id+"F42.opExtrude","CAP_EDGE",EDGE,{"disambiguationData":[OSD([sQuery(id+"F41.wireOp",EDGE,"E110.4.0.0")])],"isStart":false})}),makeQuery(id+"F39.opExtrude","CAP_FACE",FACE,{"disambiguationData":[OSD([sQuery(id+"F38.wireOp",EDGE,"E108.bottom"),sQuery(id+"F38.wireOp",EDGE,"E108.top"),sQuery(id+"F38.wireOp",EDGE,"E108.left"),sQuery(id+"F38.wireOp",EDGE,"E108.right")])],"isStart":false})],"blendedInto":[makeQuery(id+"F39.opExtrude","CAP_FACE",FACE,{"disambiguationData":[OSD([sQuery(id+"F38.wireOp",EDGE,"E108.bottom"),sQuery(id+"F38.wireOp",EDGE,"E108.top"),sQuery(id+"F38.wireOp",EDGE,"E108.left"),sQuery(id+"F38.wireOp",EDGE,"E108.right")])],"isStart":false})]});
            var Q41;
            Q41=makeQuery(id+"F43.opChamfer","BLEND_EDGE",EDGE,{"blendedFrom":[makeQuery(id+"F42.boolean.opBoolean","COPY",EDGE,{"derivedFrom":makeQuery(id+"F42.opExtrude","CAP_EDGE",EDGE,{"disambiguationData":[OSD([sQuery(id+"F41.wireOp",EDGE,"E110.4.1.0")])],"isStart":false})}),makeQuery(id+"F39.opExtrude","CAP_FACE",FACE,{"disambiguationData":[OSD([sQuery(id+"F38.wireOp",EDGE,"E108.bottom"),sQuery(id+"F38.wireOp",EDGE,"E108.top"),sQuery(id+"F38.wireOp",EDGE,"E108.left"),sQuery(id+"F38.wireOp",EDGE,"E108.right")])],"isStart":false})],"blendedInto":[makeQuery(id+"F39.opExtrude","CAP_FACE",FACE,{"disambiguationData":[OSD([sQuery(id+"F38.wireOp",EDGE,"E108.bottom"),sQuery(id+"F38.wireOp",EDGE,"E108.top"),sQuery(id+"F38.wireOp",EDGE,"E108.left"),sQuery(id+"F38.wireOp",EDGE,"E108.right")])],"isStart":false})]});
            var Q42;
            Q42=makeQuery(id+"F43.opChamfer","BLEND_EDGE",EDGE,{"blendedFrom":[makeQuery(id+"F42.boolean.opBoolean","COPY",EDGE,{"derivedFrom":makeQuery(id+"F42.opExtrude","CAP_EDGE",EDGE,{"disambiguationData":[OSD([sQuery(id+"F41.wireOp",EDGE,"E110.4.2.0")])],"isStart":false})}),makeQuery(id+"F39.opExtrude","CAP_FACE",FACE,{"disambiguationData":[OSD([sQuery(id+"F38.wireOp",EDGE,"E108.bottom"),sQuery(id+"F38.wireOp",EDGE,"E108.top"),sQuery(id+"F38.wireOp",EDGE,"E108.left"),sQuery(id+"F38.wireOp",EDGE,"E108.right")])],"isStart":false})],"blendedInto":[makeQuery(id+"F39.opExtrude","CAP_FACE",FACE,{"disambiguationData":[OSD([sQuery(id+"F38.wireOp",EDGE,"E108.bottom"),sQuery(id+"F38.wireOp",EDGE,"E108.top"),sQuery(id+"F38.wireOp",EDGE,"E108.left"),sQuery(id+"F38.wireOp",EDGE,"E108.right")])],"isStart":false})]});
            var Q43;
            Q43=makeQuery(id+"F43.opChamfer","BLEND_EDGE",EDGE,{"blendedFrom":[makeQuery(id+"F42.boolean.opBoolean","COPY",EDGE,{"derivedFrom":makeQuery(id+"F42.opExtrude","CAP_EDGE",EDGE,{"disambiguationData":[OSD([sQuery(id+"F41.wireOp",EDGE,"E110.3.2.0")])],"isStart":false})}),makeQuery(id+"F39.opExtrude","CAP_FACE",FACE,{"disambiguationData":[OSD([sQuery(id+"F38.wireOp",EDGE,"E108.bottom"),sQuery(id+"F38.wireOp",EDGE,"E108.top"),sQuery(id+"F38.wireOp",EDGE,"E108.left"),sQuery(id+"F38.wireOp",EDGE,"E108.right")])],"isStart":false})],"blendedInto":[makeQuery(id+"F39.opExtrude","CAP_FACE",FACE,{"disambiguationData":[OSD([sQuery(id+"F38.wireOp",EDGE,"E108.bottom"),sQuery(id+"F38.wireOp",EDGE,"E108.top"),sQuery(id+"F38.wireOp",EDGE,"E108.left"),sQuery(id+"F38.wireOp",EDGE,"E108.right")])],"isStart":false})]});
            var Q44;
            Q44=makeQuery(id+"F43.opChamfer","BLEND_EDGE",EDGE,{"blendedFrom":[makeQuery(id+"F42.boolean.opBoolean","COPY",EDGE,{"derivedFrom":makeQuery(id+"F42.opExtrude","CAP_EDGE",EDGE,{"disambiguationData":[OSD([sQuery(id+"F41.wireOp",EDGE,"E110.3.1.0")])],"isStart":false})}),makeQuery(id+"F39.opExtrude","CAP_FACE",FACE,{"disambiguationData":[OSD([sQuery(id+"F38.wireOp",EDGE,"E108.bottom"),sQuery(id+"F38.wireOp",EDGE,"E108.top"),sQuery(id+"F38.wireOp",EDGE,"E108.left"),sQuery(id+"F38.wireOp",EDGE,"E108.right")])],"isStart":false})],"blendedInto":[makeQuery(id+"F39.opExtrude","CAP_FACE",FACE,{"disambiguationData":[OSD([sQuery(id+"F38.wireOp",EDGE,"E108.bottom"),sQuery(id+"F38.wireOp",EDGE,"E108.top"),sQuery(id+"F38.wireOp",EDGE,"E108.left"),sQuery(id+"F38.wireOp",EDGE,"E108.right")])],"isStart":false})]});
            var Q45;
            Q45=makeQuery(id+"F43.opChamfer","BLEND_EDGE",EDGE,{"blendedFrom":[makeQuery(id+"F42.boolean.opBoolean","COPY",EDGE,{"derivedFrom":makeQuery(id+"F42.opExtrude","CAP_EDGE",EDGE,{"disambiguationData":[OSD([sQuery(id+"F41.wireOp",EDGE,"E110.3.0.0")])],"isStart":false})}),makeQuery(id+"F39.opExtrude","CAP_FACE",FACE,{"disambiguationData":[OSD([sQuery(id+"F38.wireOp",EDGE,"E108.bottom"),sQuery(id+"F38.wireOp",EDGE,"E108.top"),sQuery(id+"F38.wireOp",EDGE,"E108.left"),sQuery(id+"F38.wireOp",EDGE,"E108.right")])],"isStart":false})],"blendedInto":[makeQuery(id+"F39.opExtrude","CAP_FACE",FACE,{"disambiguationData":[OSD([sQuery(id+"F38.wireOp",EDGE,"E108.bottom"),sQuery(id+"F38.wireOp",EDGE,"E108.top"),sQuery(id+"F38.wireOp",EDGE,"E108.left"),sQuery(id+"F38.wireOp",EDGE,"E108.right")])],"isStart":false})]});
            var Q46;
            Q46=makeQuery(id+"F43.opChamfer","BLEND_EDGE",EDGE,{"blendedFrom":[makeQuery(id+"F42.boolean.opBoolean","COPY",EDGE,{"derivedFrom":makeQuery(id+"F42.opExtrude","CAP_EDGE",EDGE,{"disambiguationData":[OSD([sQuery(id+"F41.wireOp",EDGE,"E110.2.0.0")])],"isStart":false})}),makeQuery(id+"F39.opExtrude","CAP_FACE",FACE,{"disambiguationData":[OSD([sQuery(id+"F38.wireOp",EDGE,"E108.bottom"),sQuery(id+"F38.wireOp",EDGE,"E108.top"),sQuery(id+"F38.wireOp",EDGE,"E108.left"),sQuery(id+"F38.wireOp",EDGE,"E108.right")])],"isStart":false})],"blendedInto":[makeQuery(id+"F39.opExtrude","CAP_FACE",FACE,{"disambiguationData":[OSD([sQuery(id+"F38.wireOp",EDGE,"E108.bottom"),sQuery(id+"F38.wireOp",EDGE,"E108.top"),sQuery(id+"F38.wireOp",EDGE,"E108.left"),sQuery(id+"F38.wireOp",EDGE,"E108.right")])],"isStart":false})]});
            var Q47;
            Q47=makeQuery(id+"F43.opChamfer","BLEND_EDGE",EDGE,{"blendedFrom":[makeQuery(id+"F42.boolean.opBoolean","COPY",EDGE,{"derivedFrom":makeQuery(id+"F42.opExtrude","CAP_EDGE",EDGE,{"disambiguationData":[OSD([sQuery(id+"F41.wireOp",EDGE,"E110.2.1.0")])],"isStart":false})}),makeQuery(id+"F39.opExtrude","CAP_FACE",FACE,{"disambiguationData":[OSD([sQuery(id+"F38.wireOp",EDGE,"E108.bottom"),sQuery(id+"F38.wireOp",EDGE,"E108.top"),sQuery(id+"F38.wireOp",EDGE,"E108.left"),sQuery(id+"F38.wireOp",EDGE,"E108.right")])],"isStart":false})],"blendedInto":[makeQuery(id+"F39.opExtrude","CAP_FACE",FACE,{"disambiguationData":[OSD([sQuery(id+"F38.wireOp",EDGE,"E108.bottom"),sQuery(id+"F38.wireOp",EDGE,"E108.top"),sQuery(id+"F38.wireOp",EDGE,"E108.left"),sQuery(id+"F38.wireOp",EDGE,"E108.right")])],"isStart":false})]});
            var Q48;
            Q48=makeQuery(id+"F43.opChamfer","BLEND_EDGE",EDGE,{"blendedFrom":[makeQuery(id+"F42.boolean.opBoolean","COPY",EDGE,{"derivedFrom":makeQuery(id+"F42.opExtrude","CAP_EDGE",EDGE,{"disambiguationData":[OSD([sQuery(id+"F41.wireOp",EDGE,"E110.2.2.0")])],"isStart":false})}),makeQuery(id+"F39.opExtrude","CAP_FACE",FACE,{"disambiguationData":[OSD([sQuery(id+"F38.wireOp",EDGE,"E108.bottom"),sQuery(id+"F38.wireOp",EDGE,"E108.top"),sQuery(id+"F38.wireOp",EDGE,"E108.left"),sQuery(id+"F38.wireOp",EDGE,"E108.right")])],"isStart":false})],"blendedInto":[makeQuery(id+"F39.opExtrude","CAP_FACE",FACE,{"disambiguationData":[OSD([sQuery(id+"F38.wireOp",EDGE,"E108.bottom"),sQuery(id+"F38.wireOp",EDGE,"E108.top"),sQuery(id+"F38.wireOp",EDGE,"E108.left"),sQuery(id+"F38.wireOp",EDGE,"E108.right")])],"isStart":false})]});
            var Q49;
            Q49=makeQuery(id+"F43.opChamfer","BLEND_EDGE",EDGE,{"blendedFrom":[makeQuery(id+"F42.boolean.opBoolean","COPY",EDGE,{"derivedFrom":makeQuery(id+"F42.opExtrude","CAP_EDGE",EDGE,{"disambiguationData":[OSD([sQuery(id+"F41.wireOp",EDGE,"E110.1.0.0")])],"isStart":false})}),makeQuery(id+"F39.opExtrude","CAP_FACE",FACE,{"disambiguationData":[OSD([sQuery(id+"F38.wireOp",EDGE,"E108.bottom"),sQuery(id+"F38.wireOp",EDGE,"E108.top"),sQuery(id+"F38.wireOp",EDGE,"E108.left"),sQuery(id+"F38.wireOp",EDGE,"E108.right")])],"isStart":false})],"blendedInto":[makeQuery(id+"F39.opExtrude","CAP_FACE",FACE,{"disambiguationData":[OSD([sQuery(id+"F38.wireOp",EDGE,"E108.bottom"),sQuery(id+"F38.wireOp",EDGE,"E108.top"),sQuery(id+"F38.wireOp",EDGE,"E108.left"),sQuery(id+"F38.wireOp",EDGE,"E108.right")])],"isStart":false})]});
            var Q50;
            Q50=makeQuery(id+"F43.opChamfer","BLEND_EDGE",EDGE,{"blendedFrom":[makeQuery(id+"F42.boolean.opBoolean","COPY",EDGE,{"derivedFrom":makeQuery(id+"F42.opExtrude","CAP_EDGE",EDGE,{"disambiguationData":[OSD([sQuery(id+"F41.wireOp",EDGE,"E109")])],"isStart":false})}),makeQuery(id+"F39.opExtrude","CAP_FACE",FACE,{"disambiguationData":[OSD([sQuery(id+"F38.wireOp",EDGE,"E108.bottom"),sQuery(id+"F38.wireOp",EDGE,"E108.top"),sQuery(id+"F38.wireOp",EDGE,"E108.left"),sQuery(id+"F38.wireOp",EDGE,"E108.right")])],"isStart":false})],"blendedInto":[makeQuery(id+"F39.opExtrude","CAP_FACE",FACE,{"disambiguationData":[OSD([sQuery(id+"F38.wireOp",EDGE,"E108.bottom"),sQuery(id+"F38.wireOp",EDGE,"E108.top"),sQuery(id+"F38.wireOp",EDGE,"E108.left"),sQuery(id+"F38.wireOp",EDGE,"E108.right")])],"isStart":false})]});
            var Q51;
            Q51=makeQuery(id+"F43.opChamfer","BLEND_EDGE",EDGE,{"blendedFrom":[makeQuery(id+"F42.boolean.opBoolean","COPY",EDGE,{"derivedFrom":makeQuery(id+"F42.opExtrude","CAP_EDGE",EDGE,{"disambiguationData":[OSD([sQuery(id+"F41.wireOp",EDGE,"E110.0.1.0")])],"isStart":false})}),makeQuery(id+"F39.opExtrude","CAP_FACE",FACE,{"disambiguationData":[OSD([sQuery(id+"F38.wireOp",EDGE,"E108.bottom"),sQuery(id+"F38.wireOp",EDGE,"E108.top"),sQuery(id+"F38.wireOp",EDGE,"E108.left"),sQuery(id+"F38.wireOp",EDGE,"E108.right")])],"isStart":false})],"blendedInto":[makeQuery(id+"F39.opExtrude","CAP_FACE",FACE,{"disambiguationData":[OSD([sQuery(id+"F38.wireOp",EDGE,"E108.bottom"),sQuery(id+"F38.wireOp",EDGE,"E108.top"),sQuery(id+"F38.wireOp",EDGE,"E108.left"),sQuery(id+"F38.wireOp",EDGE,"E108.right")])],"isStart":false})]});
            var Q52;
            Q52=makeQuery(id+"F43.opChamfer","BLEND_EDGE",EDGE,{"blendedFrom":[makeQuery(id+"F42.boolean.opBoolean","COPY",EDGE,{"derivedFrom":makeQuery(id+"F42.opExtrude","CAP_EDGE",EDGE,{"disambiguationData":[OSD([sQuery(id+"F41.wireOp",EDGE,"E110.1.1.0")])],"isStart":false})}),makeQuery(id+"F39.opExtrude","CAP_FACE",FACE,{"disambiguationData":[OSD([sQuery(id+"F38.wireOp",EDGE,"E108.bottom"),sQuery(id+"F38.wireOp",EDGE,"E108.top"),sQuery(id+"F38.wireOp",EDGE,"E108.left"),sQuery(id+"F38.wireOp",EDGE,"E108.right")])],"isStart":false})],"blendedInto":[makeQuery(id+"F39.opExtrude","CAP_FACE",FACE,{"disambiguationData":[OSD([sQuery(id+"F38.wireOp",EDGE,"E108.bottom"),sQuery(id+"F38.wireOp",EDGE,"E108.top"),sQuery(id+"F38.wireOp",EDGE,"E108.left"),sQuery(id+"F38.wireOp",EDGE,"E108.right")])],"isStart":false})]});
            var Q53;
            Q53=makeQuery(id+"F43.opChamfer","BLEND_EDGE",EDGE,{"blendedFrom":[makeQuery(id+"F42.boolean.opBoolean","COPY",EDGE,{"derivedFrom":makeQuery(id+"F42.opExtrude","CAP_EDGE",EDGE,{"disambiguationData":[OSD([sQuery(id+"F41.wireOp",EDGE,"E110.1.2.0")])],"isStart":false})}),makeQuery(id+"F39.opExtrude","CAP_FACE",FACE,{"disambiguationData":[OSD([sQuery(id+"F38.wireOp",EDGE,"E108.bottom"),sQuery(id+"F38.wireOp",EDGE,"E108.top"),sQuery(id+"F38.wireOp",EDGE,"E108.left"),sQuery(id+"F38.wireOp",EDGE,"E108.right")])],"isStart":false})],"blendedInto":[makeQuery(id+"F39.opExtrude","CAP_FACE",FACE,{"disambiguationData":[OSD([sQuery(id+"F38.wireOp",EDGE,"E108.bottom"),sQuery(id+"F38.wireOp",EDGE,"E108.top"),sQuery(id+"F38.wireOp",EDGE,"E108.left"),sQuery(id+"F38.wireOp",EDGE,"E108.right")])],"isStart":false})]});
            var Q54;
            Q54=makeQuery(id+"F43.opChamfer","BLEND_EDGE",EDGE,{"blendedFrom":[makeQuery(id+"F42.boolean.opBoolean","COPY",EDGE,{"derivedFrom":makeQuery(id+"F42.opExtrude","CAP_EDGE",EDGE,{"disambiguationData":[OSD([sQuery(id+"F41.wireOp",EDGE,"E110.0.2.0")])],"isStart":false})}),makeQuery(id+"F39.opExtrude","CAP_FACE",FACE,{"disambiguationData":[OSD([sQuery(id+"F38.wireOp",EDGE,"E108.bottom"),sQuery(id+"F38.wireOp",EDGE,"E108.top"),sQuery(id+"F38.wireOp",EDGE,"E108.left"),sQuery(id+"F38.wireOp",EDGE,"E108.right")])],"isStart":false})],"blendedInto":[makeQuery(id+"F39.opExtrude","CAP_FACE",FACE,{"disambiguationData":[OSD([sQuery(id+"F38.wireOp",EDGE,"E108.bottom"),sQuery(id+"F38.wireOp",EDGE,"E108.top"),sQuery(id+"F38.wireOp",EDGE,"E108.left"),sQuery(id+"F38.wireOp",EDGE,"E108.right")])],"isStart":false})]});
            var Q55;
            Q55=makeQuery(id+"F43.opChamfer","BLEND_EDGE",EDGE,{"blendedFrom":[makeQuery(id+"F42.boolean.opBoolean","COPY",EDGE,{"derivedFrom":makeQuery(id+"F42.opExtrude","CAP_EDGE",EDGE,{"disambiguationData":[OSD([sQuery(id+"F41.wireOp",EDGE,"E110.1.3.0")])],"isStart":false})}),makeQuery(id+"F39.opExtrude","CAP_FACE",FACE,{"disambiguationData":[OSD([sQuery(id+"F38.wireOp",EDGE,"E108.bottom"),sQuery(id+"F38.wireOp",EDGE,"E108.top"),sQuery(id+"F38.wireOp",EDGE,"E108.left"),sQuery(id+"F38.wireOp",EDGE,"E108.right")])],"isStart":false})],"blendedInto":[makeQuery(id+"F39.opExtrude","CAP_FACE",FACE,{"disambiguationData":[OSD([sQuery(id+"F38.wireOp",EDGE,"E108.bottom"),sQuery(id+"F38.wireOp",EDGE,"E108.top"),sQuery(id+"F38.wireOp",EDGE,"E108.left"),sQuery(id+"F38.wireOp",EDGE,"E108.right")])],"isStart":false})]});
            var Q56;
            Q56=makeQuery(id+"F43.opChamfer","BLEND_EDGE",EDGE,{"blendedFrom":[makeQuery(id+"F42.boolean.opBoolean","COPY",EDGE,{"derivedFrom":makeQuery(id+"F42.opExtrude","CAP_EDGE",EDGE,{"disambiguationData":[OSD([sQuery(id+"F41.wireOp",EDGE,"E110.0.3.0")])],"isStart":false})}),makeQuery(id+"F39.opExtrude","CAP_FACE",FACE,{"disambiguationData":[OSD([sQuery(id+"F38.wireOp",EDGE,"E108.bottom"),sQuery(id+"F38.wireOp",EDGE,"E108.top"),sQuery(id+"F38.wireOp",EDGE,"E108.left"),sQuery(id+"F38.wireOp",EDGE,"E108.right")])],"isStart":false})],"blendedInto":[makeQuery(id+"F39.opExtrude","CAP_FACE",FACE,{"disambiguationData":[OSD([sQuery(id+"F38.wireOp",EDGE,"E108.bottom"),sQuery(id+"F38.wireOp",EDGE,"E108.top"),sQuery(id+"F38.wireOp",EDGE,"E108.left"),sQuery(id+"F38.wireOp",EDGE,"E108.right")])],"isStart":false})]});
            var Q57;
            Q57=makeQuery(id+"F43.opChamfer","BLEND_EDGE",EDGE,{"blendedFrom":[makeQuery(id+"F42.boolean.opBoolean","COPY",EDGE,{"derivedFrom":makeQuery(id+"F42.opExtrude","CAP_EDGE",EDGE,{"disambiguationData":[OSD([sQuery(id+"F41.wireOp",EDGE,"E110.0.4.0")])],"isStart":false})}),makeQuery(id+"F39.opExtrude","CAP_FACE",FACE,{"disambiguationData":[OSD([sQuery(id+"F38.wireOp",EDGE,"E108.bottom"),sQuery(id+"F38.wireOp",EDGE,"E108.top"),sQuery(id+"F38.wireOp",EDGE,"E108.left"),sQuery(id+"F38.wireOp",EDGE,"E108.right")])],"isStart":false})],"blendedInto":[makeQuery(id+"F39.opExtrude","CAP_FACE",FACE,{"disambiguationData":[OSD([sQuery(id+"F38.wireOp",EDGE,"E108.bottom"),sQuery(id+"F38.wireOp",EDGE,"E108.top"),sQuery(id+"F38.wireOp",EDGE,"E108.left"),sQuery(id+"F38.wireOp",EDGE,"E108.right")])],"isStart":false})]});
            var Q58;
            Q58=makeQuery(id+"F43.opChamfer","BLEND_EDGE",EDGE,{"blendedFrom":[makeQuery(id+"F42.boolean.opBoolean","COPY",EDGE,{"derivedFrom":makeQuery(id+"F42.opExtrude","CAP_EDGE",EDGE,{"disambiguationData":[OSD([sQuery(id+"F41.wireOp",EDGE,"E110.0.5.0")])],"isStart":false})}),makeQuery(id+"F39.opExtrude","CAP_FACE",FACE,{"disambiguationData":[OSD([sQuery(id+"F38.wireOp",EDGE,"E108.bottom"),sQuery(id+"F38.wireOp",EDGE,"E108.top"),sQuery(id+"F38.wireOp",EDGE,"E108.left"),sQuery(id+"F38.wireOp",EDGE,"E108.right")])],"isStart":false})],"blendedInto":[makeQuery(id+"F39.opExtrude","CAP_FACE",FACE,{"disambiguationData":[OSD([sQuery(id+"F38.wireOp",EDGE,"E108.bottom"),sQuery(id+"F38.wireOp",EDGE,"E108.top"),sQuery(id+"F38.wireOp",EDGE,"E108.left"),sQuery(id+"F38.wireOp",EDGE,"E108.right")])],"isStart":false})]});
            var Q59;
            Q59=makeQuery(id+"F43.opChamfer","BLEND_EDGE",EDGE,{"blendedFrom":[makeQuery(id+"F42.boolean.opBoolean","COPY",EDGE,{"derivedFrom":makeQuery(id+"F42.opExtrude","CAP_EDGE",EDGE,{"disambiguationData":[OSD([sQuery(id+"F41.wireOp",EDGE,"E110.0.6.0")])],"isStart":false})}),makeQuery(id+"F39.opExtrude","CAP_FACE",FACE,{"disambiguationData":[OSD([sQuery(id+"F38.wireOp",EDGE,"E108.bottom"),sQuery(id+"F38.wireOp",EDGE,"E108.top"),sQuery(id+"F38.wireOp",EDGE,"E108.left"),sQuery(id+"F38.wireOp",EDGE,"E108.right")])],"isStart":false})],"blendedInto":[makeQuery(id+"F39.opExtrude","CAP_FACE",FACE,{"disambiguationData":[OSD([sQuery(id+"F38.wireOp",EDGE,"E108.bottom"),sQuery(id+"F38.wireOp",EDGE,"E108.top"),sQuery(id+"F38.wireOp",EDGE,"E108.left"),sQuery(id+"F38.wireOp",EDGE,"E108.right")])],"isStart":false})]});
            var Q60;
            Q60=makeQuery(id+"F43.opChamfer","BLEND_EDGE",EDGE,{"blendedFrom":[makeQuery(id+"F42.boolean.opBoolean","COPY",EDGE,{"derivedFrom":makeQuery(id+"F42.opExtrude","CAP_EDGE",EDGE,{"disambiguationData":[OSD([sQuery(id+"F41.wireOp",EDGE,"E110.1.6.0")])],"isStart":false})}),makeQuery(id+"F39.opExtrude","CAP_FACE",FACE,{"disambiguationData":[OSD([sQuery(id+"F38.wireOp",EDGE,"E108.bottom"),sQuery(id+"F38.wireOp",EDGE,"E108.top"),sQuery(id+"F38.wireOp",EDGE,"E108.left"),sQuery(id+"F38.wireOp",EDGE,"E108.right")])],"isStart":false})],"blendedInto":[makeQuery(id+"F39.opExtrude","CAP_FACE",FACE,{"disambiguationData":[OSD([sQuery(id+"F38.wireOp",EDGE,"E108.bottom"),sQuery(id+"F38.wireOp",EDGE,"E108.top"),sQuery(id+"F38.wireOp",EDGE,"E108.left"),sQuery(id+"F38.wireOp",EDGE,"E108.right")])],"isStart":false})]});
            var Q61;
            Q61=makeQuery(id+"F43.opChamfer","BLEND_EDGE",EDGE,{"blendedFrom":[makeQuery(id+"F42.boolean.opBoolean","COPY",EDGE,{"derivedFrom":makeQuery(id+"F42.opExtrude","CAP_EDGE",EDGE,{"disambiguationData":[OSD([sQuery(id+"F41.wireOp",EDGE,"E110.1.5.0")])],"isStart":false})}),makeQuery(id+"F39.opExtrude","CAP_FACE",FACE,{"disambiguationData":[OSD([sQuery(id+"F38.wireOp",EDGE,"E108.bottom"),sQuery(id+"F38.wireOp",EDGE,"E108.top"),sQuery(id+"F38.wireOp",EDGE,"E108.left"),sQuery(id+"F38.wireOp",EDGE,"E108.right")])],"isStart":false})],"blendedInto":[makeQuery(id+"F39.opExtrude","CAP_FACE",FACE,{"disambiguationData":[OSD([sQuery(id+"F38.wireOp",EDGE,"E108.bottom"),sQuery(id+"F38.wireOp",EDGE,"E108.top"),sQuery(id+"F38.wireOp",EDGE,"E108.left"),sQuery(id+"F38.wireOp",EDGE,"E108.right")])],"isStart":false})]});
            var Q62;
            Q62=makeQuery(id+"F43.opChamfer","BLEND_EDGE",EDGE,{"blendedFrom":[makeQuery(id+"F42.boolean.opBoolean","COPY",EDGE,{"derivedFrom":makeQuery(id+"F42.opExtrude","CAP_EDGE",EDGE,{"disambiguationData":[OSD([sQuery(id+"F41.wireOp",EDGE,"E110.1.4.0")])],"isStart":false})}),makeQuery(id+"F39.opExtrude","CAP_FACE",FACE,{"disambiguationData":[OSD([sQuery(id+"F38.wireOp",EDGE,"E108.bottom"),sQuery(id+"F38.wireOp",EDGE,"E108.top"),sQuery(id+"F38.wireOp",EDGE,"E108.left"),sQuery(id+"F38.wireOp",EDGE,"E108.right")])],"isStart":false})],"blendedInto":[makeQuery(id+"F39.opExtrude","CAP_FACE",FACE,{"disambiguationData":[OSD([sQuery(id+"F38.wireOp",EDGE,"E108.bottom"),sQuery(id+"F38.wireOp",EDGE,"E108.top"),sQuery(id+"F38.wireOp",EDGE,"E108.left"),sQuery(id+"F38.wireOp",EDGE,"E108.right")])],"isStart":false})]});
            fillet(context, id + "F44", {"entities" : qUnion([Q0, Q1, Q2, Q3, Q4, Q5, Q6, Q7, Q8, Q9, Q10, Q11, Q12, Q13, Q14, Q15, Q16, Q17, Q18, Q19, Q20, Q21, Q22, Q23, Q24, Q25, Q26, Q27, Q28, Q29, Q30, Q31, Q32, Q33, Q34, Q35, Q36, Q37, Q38, Q39, Q40, Q41, Q42, Q43, Q44, Q45, Q46, Q47, Q48, Q49, Q50, Q51, Q52, Q53, Q54, Q55, Q56, Q57, Q58, Q59, Q60, Q61, Q62]), "radius" : 5.08 * mm, "tangentPropagation" : true, "allowEdgeOverflow" : false});
        }
    });
